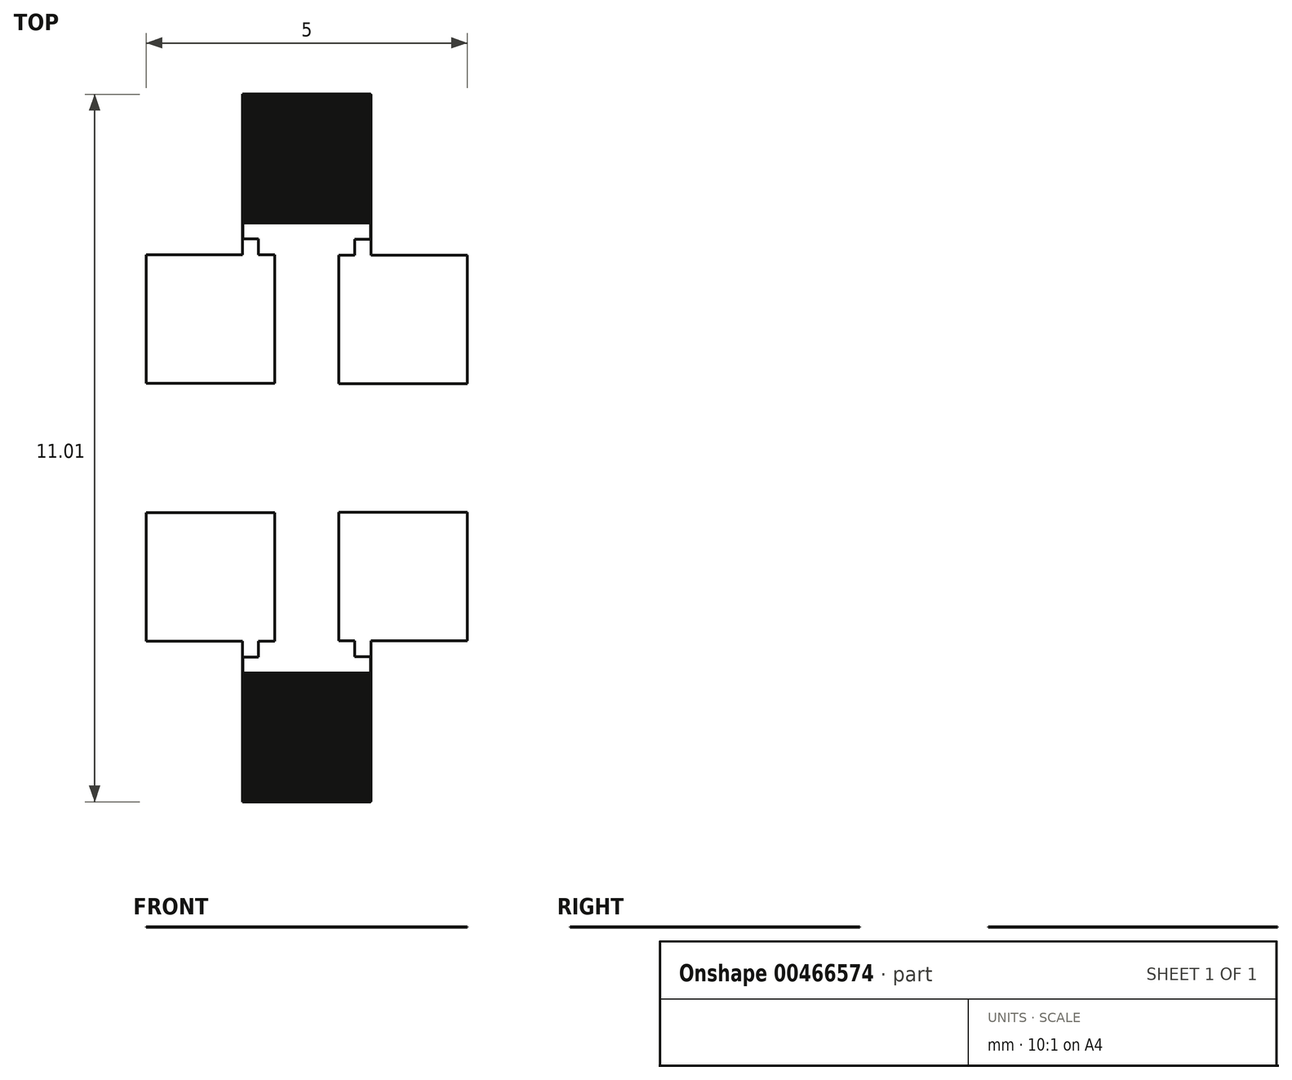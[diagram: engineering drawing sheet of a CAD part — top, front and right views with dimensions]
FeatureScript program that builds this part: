
annotation { "Feature Type Name" : "Feature", "Feature Type Description" : "" }
export const myFeature = defineFeature(function(context is Context, id is Id, definition is map)
    precondition{}
    {
        {
            var Q0;
            Q0=qCreatedBy(makeId("Top.planeOp"),FACE);
            var sketch = newSketch(context, id + "F0", { "sketchPlane" : qUnion([Q0])});
            skLineSegment(sketch, "E0.bottom", {"start": v(-1, 1) * mm, "end": v(1, 1) * mm, "construction": true});
            skLineSegment(sketch, "E0.top", {"start": v(-1, -1) * mm, "end": v(1, -1) * mm, "construction": true});
            skLineSegment(sketch, "E0.left", {"start": v(-1, 1) * mm, "end": v(-1, -1) * mm, "construction": true});
            skLineSegment(sketch, "E0.right", {"start": v(1, 1) * mm, "end": v(1, -1) * mm, "construction": true});
            skSolve(sketch);
        }
        {
            var Q0;
            Q0=qCreatedBy(makeId("Top.planeOp"),FACE);
            var sketch = newSketch(context, id + "F1", { "sketchPlane" : qUnion([Q0])});
            skPoint(sketch, "E1.0", {"position": v(-1, -1) * mm});
            skLineSegment(sketch, "E2", {"start": v(-1, -1) * mm, "end": v(1, -1) * mm});
            skLineSegment(sketch, "E3", {"start": v(1, -1) * mm, "end": v(1, -1) * mm});
            skLineSegment(sketch, "E4", {"start": v(1, -1) * mm, "end": v(-1, -1) * mm});
            skLineSegment(sketch, "E5", {"start": v(-1, -1) * mm, "end": v(-1, 1.5) * mm});
            skPoint(sketch, "E6.0", {"position": v(-1, 1) * mm});
            skLineSegment(sketch, "E7", {"start": v(-1, 1.5) * mm, "end": v(-2.5, 1.5) * mm});
            skLineSegment(sketch, "E8", {"start": v(-2.5, 1.5) * mm, "end": v(-2.5, 3.5) * mm});
            skLineSegment(sketch, "E9", {"start": v(-2.5, 3.5) * mm, "end": v(-0.5, 3.5) * mm});
            skLineSegment(sketch, "E10", {"start": v(-0.5, 3.5) * mm, "end": v(-0.5, 1.5) * mm});
            skLineSegment(sketch, "E11", {"start": v(-0.5, 1.5) * mm, "end": v(-0.75, 1.5) * mm});
            skLineSegment(sketch, "E12", {"start": v(-0.75, 1.5) * mm, "end": v(-0.75, 1.25) * mm});
            skLineSegment(sketch, "E13", {"start": v(-0.75, 1.25) * mm, "end": v(-1, 1.25) * mm});
            skLineSegment(sketch, "E14", {"start": v(-1, -1) * mm, "end": v(-1, -0.99) * mm});
            skLineSegment(sketch, "E15", {"start": v(-1, -0.99) * mm, "end": v(1, -0.99) * mm});
            skLineSegment(sketch, "E16.0", {"start": v(1, 1) * mm, "end": v(1, -1) * mm});
            skLineSegment(sketch, "E17", {"start": v(1, 1) * mm, "end": v(1, 1.5) * mm});
            skLineSegment(sketch, "E18", {"start": v(1, 1.5) * mm, "end": v(2.5, 1.5) * mm});
            skLineSegment(sketch, "E19", {"start": v(2.5, 1.5) * mm, "end": v(2.5, 3.5) * mm});
            skLineSegment(sketch, "E20", {"start": v(2.5, 3.5) * mm, "end": v(0.5, 3.5) * mm});
            skLineSegment(sketch, "E21", {"start": v(0.5, 3.5) * mm, "end": v(0.5, 1.5) * mm});
            skLineSegment(sketch, "E22", {"start": v(0.5, 1.5) * mm, "end": v(0.74, 1.5) * mm});
            skLineSegment(sketch, "E23", {"start": v(0.74, 1.5) * mm, "end": v(0.74, 1.26) * mm});
            skLineSegment(sketch, "E24", {"start": v(0.74, 1.26) * mm, "end": v(1, 1.26) * mm});
            skLineSegment(sketch, "E25", {"start": v(-2.5, 4.5) * mm, "end": v(2.5, 4.5) * mm, "construction": true});
            skLineSegment(sketch, "E26", {"start": v(1, -0.99) * mm, "end": v(1, -0.98) * mm});
            skLineSegment(sketch, "E27", {"start": v(1, -0.98) * mm, "end": v(-1, -0.98) * mm});
            skLineSegment(sketch, "E28.0.1.0", {"start": v(1, -0.97) * mm, "end": v(-1, -0.97) * mm});
            skLineSegment(sketch, "E28.0.1.1", {"start": v(1, -0.98) * mm, "end": v(1, -0.97) * mm});
            skLineSegment(sketch, "E28.0.1.2", {"start": v(-1, -0.98) * mm, "end": v(1, -0.98) * mm});
            skLineSegment(sketch, "E28.0.1.3", {"start": v(-1, -0.98) * mm, "end": v(-1, -0.98) * mm});
            skLineSegment(sketch, "E28.0.2.0", {"start": v(1, -0.96) * mm, "end": v(-1, -0.96) * mm});
            skLineSegment(sketch, "E28.0.2.1", {"start": v(1, -0.96) * mm, "end": v(1, -0.96) * mm});
            skLineSegment(sketch, "E28.0.2.2", {"start": v(-1, -0.96) * mm, "end": v(1, -0.96) * mm});
            skLineSegment(sketch, "E28.0.2.3", {"start": v(-1, -0.97) * mm, "end": v(-1, -0.96) * mm});
            skLineSegment(sketch, "E28.0.3.0", {"start": v(1, -0.95) * mm, "end": v(-1, -0.95) * mm});
            skLineSegment(sketch, "E28.0.3.1", {"start": v(1, -0.95) * mm, "end": v(1, -0.95) * mm});
            skLineSegment(sketch, "E28.0.3.2", {"start": v(-1, -0.95) * mm, "end": v(1, -0.95) * mm});
            skLineSegment(sketch, "E28.0.3.3", {"start": v(-1, -0.96) * mm, "end": v(-1, -0.95) * mm});
            skLineSegment(sketch, "E28.0.4.0", {"start": v(1, -0.94) * mm, "end": v(-1, -0.94) * mm});
            skLineSegment(sketch, "E28.0.4.1", {"start": v(1, -0.94) * mm, "end": v(1, -0.94) * mm});
            skLineSegment(sketch, "E28.0.4.2", {"start": v(-1, -0.94) * mm, "end": v(1, -0.94) * mm});
            skLineSegment(sketch, "E28.0.4.3", {"start": v(-1, -0.95) * mm, "end": v(-1, -0.94) * mm});
            skLineSegment(sketch, "E28.0.5.0", {"start": v(1, -0.92) * mm, "end": v(-1, -0.92) * mm});
            skLineSegment(sketch, "E28.0.5.1", {"start": v(1, -0.93) * mm, "end": v(1, -0.92) * mm});
            skLineSegment(sketch, "E28.0.5.2", {"start": v(-1, -0.93) * mm, "end": v(1, -0.93) * mm});
            skLineSegment(sketch, "E28.0.5.3", {"start": v(-1, -0.94) * mm, "end": v(-1, -0.93) * mm});
            skLineSegment(sketch, "E28.0.6.0", {"start": v(1, -0.91) * mm, "end": v(-1, -0.91) * mm});
            skLineSegment(sketch, "E28.0.6.1", {"start": v(1, -0.92) * mm, "end": v(1, -0.91) * mm});
            skLineSegment(sketch, "E28.0.6.2", {"start": v(-1, -0.92) * mm, "end": v(1, -0.92) * mm});
            skLineSegment(sketch, "E28.0.6.3", {"start": v(-1, -0.92) * mm, "end": v(-1, -0.92) * mm});
            skLineSegment(sketch, "E28.0.7.0", {"start": v(1, -0.9) * mm, "end": v(-1, -0.9) * mm});
            skLineSegment(sketch, "E28.0.7.1", {"start": v(1, -0.9) * mm, "end": v(1, -0.9) * mm});
            skLineSegment(sketch, "E28.0.7.2", {"start": v(-1, -0.9) * mm, "end": v(1, -0.9) * mm});
            skLineSegment(sketch, "E28.0.7.3", {"start": v(-1, -0.91) * mm, "end": v(-1, -0.9) * mm});
            skLineSegment(sketch, "E28.0.8.0", {"start": v(1, -0.89) * mm, "end": v(-1, -0.89) * mm});
            skLineSegment(sketch, "E28.0.8.1", {"start": v(1, -0.9) * mm, "end": v(1, -0.89) * mm});
            skLineSegment(sketch, "E28.0.8.2", {"start": v(-1, -0.9) * mm, "end": v(1, -0.9) * mm});
            skLineSegment(sketch, "E28.0.8.3", {"start": v(-1, -0.9) * mm, "end": v(-1, -0.9) * mm});
            skLineSegment(sketch, "E28.0.9.0", {"start": v(1, -0.88) * mm, "end": v(-1, -0.88) * mm});
            skLineSegment(sketch, "E28.0.9.1", {"start": v(1, -0.88) * mm, "end": v(1, -0.88) * mm});
            skLineSegment(sketch, "E28.0.9.2", {"start": v(-1, -0.88) * mm, "end": v(1, -0.88) * mm});
            skLineSegment(sketch, "E28.0.9.3", {"start": v(-1, -0.89) * mm, "end": v(-1, -0.88) * mm});
            skLineSegment(sketch, "E28.0.10.0", {"start": v(1, -0.86) * mm, "end": v(-1, -0.86) * mm});
            skLineSegment(sketch, "E28.0.10.1", {"start": v(1, -0.87) * mm, "end": v(1, -0.86) * mm});
            skLineSegment(sketch, "E28.0.10.2", {"start": v(-1, -0.87) * mm, "end": v(1, -0.87) * mm});
            skLineSegment(sketch, "E28.0.10.3", {"start": v(-1, -0.88) * mm, "end": v(-1, -0.87) * mm});
            skLineSegment(sketch, "E28.0.11.0", {"start": v(1, -0.85) * mm, "end": v(-1, -0.85) * mm});
            skLineSegment(sketch, "E28.0.11.1", {"start": v(1, -0.86) * mm, "end": v(1, -0.85) * mm});
            skLineSegment(sketch, "E28.0.11.2", {"start": v(-1, -0.86) * mm, "end": v(1, -0.86) * mm});
            skLineSegment(sketch, "E28.0.11.3", {"start": v(-1, -0.86) * mm, "end": v(-1, -0.86) * mm});
            skLineSegment(sketch, "E28.0.12.0", {"start": v(1, -0.84) * mm, "end": v(-1, -0.84) * mm});
            skLineSegment(sketch, "E28.0.12.1", {"start": v(1, -0.84) * mm, "end": v(1, -0.84) * mm});
            skLineSegment(sketch, "E28.0.12.2", {"start": v(-1, -0.84) * mm, "end": v(1, -0.84) * mm});
            skLineSegment(sketch, "E28.0.12.3", {"start": v(-1, -0.85) * mm, "end": v(-1, -0.84) * mm});
            skLineSegment(sketch, "E28.0.13.0", {"start": v(1, -0.83) * mm, "end": v(-1, -0.83) * mm});
            skLineSegment(sketch, "E28.0.13.1", {"start": v(1, -0.83) * mm, "end": v(1, -0.83) * mm});
            skLineSegment(sketch, "E28.0.13.2", {"start": v(-1, -0.83) * mm, "end": v(1, -0.83) * mm});
            skLineSegment(sketch, "E28.0.13.3", {"start": v(-1, -0.84) * mm, "end": v(-1, -0.83) * mm});
            skLineSegment(sketch, "E28.0.14.0", {"start": v(1, -0.82) * mm, "end": v(-1, -0.82) * mm});
            skLineSegment(sketch, "E28.0.14.1", {"start": v(1, -0.82) * mm, "end": v(1, -0.82) * mm});
            skLineSegment(sketch, "E28.0.14.2", {"start": v(-1, -0.82) * mm, "end": v(1, -0.82) * mm});
            skLineSegment(sketch, "E28.0.14.3", {"start": v(-1, -0.83) * mm, "end": v(-1, -0.82) * mm});
            skLineSegment(sketch, "E28.0.15.0", {"start": v(1, -0.8) * mm, "end": v(-1, -0.8) * mm});
            skLineSegment(sketch, "E28.0.15.1", {"start": v(1, -0.8) * mm, "end": v(1, -0.8) * mm});
            skLineSegment(sketch, "E28.0.15.2", {"start": v(-1, -0.8) * mm, "end": v(1, -0.8) * mm});
            skLineSegment(sketch, "E28.0.15.3", {"start": v(-1, -0.82) * mm, "end": v(-1, -0.8) * mm});
            skLineSegment(sketch, "E28.0.16.0", {"start": v(1, -0.8) * mm, "end": v(-1, -0.8) * mm});
            skLineSegment(sketch, "E28.0.16.1", {"start": v(1, -0.8) * mm, "end": v(1, -0.8) * mm});
            skLineSegment(sketch, "E28.0.16.2", {"start": v(-1, -0.8) * mm, "end": v(1, -0.8) * mm});
            skLineSegment(sketch, "E28.0.16.3", {"start": v(-1, -0.8) * mm, "end": v(-1, -0.8) * mm});
            skLineSegment(sketch, "E28.0.17.0", {"start": v(1, -0.78) * mm, "end": v(-1, -0.78) * mm});
            skLineSegment(sketch, "E28.0.17.1", {"start": v(1, -0.78) * mm, "end": v(1, -0.78) * mm});
            skLineSegment(sketch, "E28.0.17.2", {"start": v(-1, -0.78) * mm, "end": v(1, -0.78) * mm});
            skLineSegment(sketch, "E28.0.17.3", {"start": v(-1, -0.8) * mm, "end": v(-1, -0.78) * mm});
            skLineSegment(sketch, "E28.0.18.0", {"start": v(1, -0.77) * mm, "end": v(-1, -0.77) * mm});
            skLineSegment(sketch, "E28.0.18.1", {"start": v(1, -0.77) * mm, "end": v(1, -0.77) * mm});
            skLineSegment(sketch, "E28.0.18.2", {"start": v(-1, -0.77) * mm, "end": v(1, -0.77) * mm});
            skLineSegment(sketch, "E28.0.18.3", {"start": v(-1, -0.78) * mm, "end": v(-1, -0.77) * mm});
            skLineSegment(sketch, "E28.0.19.0", {"start": v(1, -0.76) * mm, "end": v(-1, -0.76) * mm});
            skLineSegment(sketch, "E28.0.19.1", {"start": v(1, -0.76) * mm, "end": v(1, -0.76) * mm});
            skLineSegment(sketch, "E28.0.19.2", {"start": v(-1, -0.76) * mm, "end": v(1, -0.76) * mm});
            skLineSegment(sketch, "E28.0.19.3", {"start": v(-1, -0.77) * mm, "end": v(-1, -0.76) * mm});
            skLineSegment(sketch, "E28.0.20.0", {"start": v(1, -0.74) * mm, "end": v(-1, -0.74) * mm});
            skLineSegment(sketch, "E28.0.20.1", {"start": v(1, -0.75) * mm, "end": v(1, -0.74) * mm});
            skLineSegment(sketch, "E28.0.20.2", {"start": v(-1, -0.75) * mm, "end": v(1, -0.75) * mm});
            skLineSegment(sketch, "E28.0.20.3", {"start": v(-1, -0.76) * mm, "end": v(-1, -0.75) * mm});
            skLineSegment(sketch, "E28.0.21.0", {"start": v(1, -0.73) * mm, "end": v(-1, -0.73) * mm});
            skLineSegment(sketch, "E28.0.21.1", {"start": v(1, -0.74) * mm, "end": v(1, -0.73) * mm});
            skLineSegment(sketch, "E28.0.21.2", {"start": v(-1, -0.74) * mm, "end": v(1, -0.74) * mm});
            skLineSegment(sketch, "E28.0.21.3", {"start": v(-1, -0.74) * mm, "end": v(-1, -0.74) * mm});
            skLineSegment(sketch, "E28.0.22.0", {"start": v(1, -0.72) * mm, "end": v(-1, -0.72) * mm});
            skLineSegment(sketch, "E28.0.22.1", {"start": v(1, -0.72) * mm, "end": v(1, -0.72) * mm});
            skLineSegment(sketch, "E28.0.22.2", {"start": v(-1, -0.72) * mm, "end": v(1, -0.72) * mm});
            skLineSegment(sketch, "E28.0.22.3", {"start": v(-1, -0.73) * mm, "end": v(-1, -0.72) * mm});
            skLineSegment(sketch, "E28.0.23.0", {"start": v(1, -0.7) * mm, "end": v(-1, -0.7) * mm});
            skLineSegment(sketch, "E28.0.23.1", {"start": v(1, -0.71) * mm, "end": v(1, -0.7) * mm});
            skLineSegment(sketch, "E28.0.23.2", {"start": v(-1, -0.71) * mm, "end": v(1, -0.71) * mm});
            skLineSegment(sketch, "E28.0.23.3", {"start": v(-1, -0.72) * mm, "end": v(-1, -0.71) * mm});
            skLineSegment(sketch, "E28.0.24.0", {"start": v(1, -0.7) * mm, "end": v(-1, -0.7) * mm});
            skLineSegment(sketch, "E28.0.24.1", {"start": v(1, -0.7) * mm, "end": v(1, -0.7) * mm});
            skLineSegment(sketch, "E28.0.24.2", {"start": v(-1, -0.7) * mm, "end": v(1, -0.7) * mm});
            skLineSegment(sketch, "E28.0.24.3", {"start": v(-1, -0.7) * mm, "end": v(-1, -0.7) * mm});
            skLineSegment(sketch, "E28.0.25.0", {"start": v(1, -0.68) * mm, "end": v(-1, -0.68) * mm});
            skLineSegment(sketch, "E28.0.25.1", {"start": v(1, -0.69) * mm, "end": v(1, -0.68) * mm});
            skLineSegment(sketch, "E28.0.25.2", {"start": v(-1, -0.69) * mm, "end": v(1, -0.69) * mm});
            skLineSegment(sketch, "E28.0.25.3", {"start": v(-1, -0.7) * mm, "end": v(-1, -0.69) * mm});
            skLineSegment(sketch, "E28.0.26.0", {"start": v(1, -0.67) * mm, "end": v(-1, -0.67) * mm});
            skLineSegment(sketch, "E28.0.26.1", {"start": v(1, -0.68) * mm, "end": v(1, -0.67) * mm});
            skLineSegment(sketch, "E28.0.26.2", {"start": v(-1, -0.68) * mm, "end": v(1, -0.68) * mm});
            skLineSegment(sketch, "E28.0.26.3", {"start": v(-1, -0.68) * mm, "end": v(-1, -0.68) * mm});
            skLineSegment(sketch, "E28.0.27.0", {"start": v(1, -0.66) * mm, "end": v(-1, -0.66) * mm});
            skLineSegment(sketch, "E28.0.27.1", {"start": v(1, -0.66) * mm, "end": v(1, -0.66) * mm});
            skLineSegment(sketch, "E28.0.27.2", {"start": v(-1, -0.66) * mm, "end": v(1, -0.66) * mm});
            skLineSegment(sketch, "E28.0.27.3", {"start": v(-1, -0.67) * mm, "end": v(-1, -0.66) * mm});
            skLineSegment(sketch, "E28.0.28.0", {"start": v(1, -0.65) * mm, "end": v(-1, -0.65) * mm});
            skLineSegment(sketch, "E28.0.28.1", {"start": v(1, -0.65) * mm, "end": v(1, -0.65) * mm});
            skLineSegment(sketch, "E28.0.28.2", {"start": v(-1, -0.65) * mm, "end": v(1, -0.65) * mm});
            skLineSegment(sketch, "E28.0.28.3", {"start": v(-1, -0.66) * mm, "end": v(-1, -0.65) * mm});
            skLineSegment(sketch, "E28.0.29.0", {"start": v(1, -0.64) * mm, "end": v(-1, -0.64) * mm});
            skLineSegment(sketch, "E28.0.29.1", {"start": v(1, -0.64) * mm, "end": v(1, -0.64) * mm});
            skLineSegment(sketch, "E28.0.29.2", {"start": v(-1, -0.64) * mm, "end": v(1, -0.64) * mm});
            skLineSegment(sketch, "E28.0.29.3", {"start": v(-1, -0.65) * mm, "end": v(-1, -0.64) * mm});
            skLineSegment(sketch, "E28.0.30.0", {"start": v(1, -0.62) * mm, "end": v(-1, -0.62) * mm});
            skLineSegment(sketch, "E28.0.30.1", {"start": v(1, -0.63) * mm, "end": v(1, -0.62) * mm});
            skLineSegment(sketch, "E28.0.30.2", {"start": v(-1, -0.63) * mm, "end": v(1, -0.63) * mm});
            skLineSegment(sketch, "E28.0.30.3", {"start": v(-1, -0.64) * mm, "end": v(-1, -0.63) * mm});
            skLineSegment(sketch, "E28.0.31.0", {"start": v(1, -0.61) * mm, "end": v(-1, -0.61) * mm});
            skLineSegment(sketch, "E28.0.31.1", {"start": v(1, -0.62) * mm, "end": v(1, -0.61) * mm});
            skLineSegment(sketch, "E28.0.31.2", {"start": v(-1, -0.62) * mm, "end": v(1, -0.62) * mm});
            skLineSegment(sketch, "E28.0.31.3", {"start": v(-1, -0.62) * mm, "end": v(-1, -0.62) * mm});
            skLineSegment(sketch, "E28.0.32.0", {"start": v(1, -0.6) * mm, "end": v(-1, -0.6) * mm});
            skLineSegment(sketch, "E28.0.32.1", {"start": v(1, -0.6) * mm, "end": v(1, -0.6) * mm});
            skLineSegment(sketch, "E28.0.32.2", {"start": v(-1, -0.6) * mm, "end": v(1, -0.6) * mm});
            skLineSegment(sketch, "E28.0.32.3", {"start": v(-1, -0.61) * mm, "end": v(-1, -0.6) * mm});
            skLineSegment(sketch, "E28.0.33.0", {"start": v(1, -0.59) * mm, "end": v(-1, -0.59) * mm});
            skLineSegment(sketch, "E28.0.33.1", {"start": v(1, -0.6) * mm, "end": v(1, -0.59) * mm});
            skLineSegment(sketch, "E28.0.33.2", {"start": v(-1, -0.6) * mm, "end": v(1, -0.6) * mm});
            skLineSegment(sketch, "E28.0.33.3", {"start": v(-1, -0.6) * mm, "end": v(-1, -0.6) * mm});
            skLineSegment(sketch, "E28.0.34.0", {"start": v(1, -0.58) * mm, "end": v(-1, -0.58) * mm});
            skLineSegment(sketch, "E28.0.34.1", {"start": v(1, -0.58) * mm, "end": v(1, -0.58) * mm});
            skLineSegment(sketch, "E28.0.34.2", {"start": v(-1, -0.58) * mm, "end": v(1, -0.58) * mm});
            skLineSegment(sketch, "E28.0.34.3", {"start": v(-1, -0.59) * mm, "end": v(-1, -0.58) * mm});
            skLineSegment(sketch, "E28.0.35.0", {"start": v(1, -0.56) * mm, "end": v(-1, -0.56) * mm});
            skLineSegment(sketch, "E28.0.35.1", {"start": v(1, -0.57) * mm, "end": v(1, -0.56) * mm});
            skLineSegment(sketch, "E28.0.35.2", {"start": v(-1, -0.57) * mm, "end": v(1, -0.57) * mm});
            skLineSegment(sketch, "E28.0.35.3", {"start": v(-1, -0.58) * mm, "end": v(-1, -0.57) * mm});
            skLineSegment(sketch, "E28.0.36.0", {"start": v(1, -0.55) * mm, "end": v(-1, -0.55) * mm});
            skLineSegment(sketch, "E28.0.36.1", {"start": v(1, -0.56) * mm, "end": v(1, -0.55) * mm});
            skLineSegment(sketch, "E28.0.36.2", {"start": v(-1, -0.56) * mm, "end": v(1, -0.56) * mm});
            skLineSegment(sketch, "E28.0.36.3", {"start": v(-1, -0.56) * mm, "end": v(-1, -0.56) * mm});
            skLineSegment(sketch, "E28.0.37.0", {"start": v(1, -0.54) * mm, "end": v(-1, -0.54) * mm});
            skLineSegment(sketch, "E28.0.37.1", {"start": v(1, -0.54) * mm, "end": v(1, -0.54) * mm});
            skLineSegment(sketch, "E28.0.37.2", {"start": v(-1, -0.54) * mm, "end": v(1, -0.54) * mm});
            skLineSegment(sketch, "E28.0.37.3", {"start": v(-1, -0.55) * mm, "end": v(-1, -0.54) * mm});
            skLineSegment(sketch, "E28.0.38.0", {"start": v(1, -0.53) * mm, "end": v(-1, -0.53) * mm});
            skLineSegment(sketch, "E28.0.38.1", {"start": v(1, -0.53) * mm, "end": v(1, -0.53) * mm});
            skLineSegment(sketch, "E28.0.38.2", {"start": v(-1, -0.53) * mm, "end": v(1, -0.53) * mm});
            skLineSegment(sketch, "E28.0.38.3", {"start": v(-1, -0.54) * mm, "end": v(-1, -0.53) * mm});
            skLineSegment(sketch, "E28.0.39.0", {"start": v(1, -0.52) * mm, "end": v(-1, -0.52) * mm});
            skLineSegment(sketch, "E28.0.39.1", {"start": v(1, -0.52) * mm, "end": v(1, -0.52) * mm});
            skLineSegment(sketch, "E28.0.39.2", {"start": v(-1, -0.52) * mm, "end": v(1, -0.52) * mm});
            skLineSegment(sketch, "E28.0.39.3", {"start": v(-1, -0.53) * mm, "end": v(-1, -0.52) * mm});
            skLineSegment(sketch, "E28.0.40.0", {"start": v(1, -0.5) * mm, "end": v(-1, -0.5) * mm});
            skLineSegment(sketch, "E28.0.40.1", {"start": v(1, -0.5) * mm, "end": v(1, -0.5) * mm});
            skLineSegment(sketch, "E28.0.40.2", {"start": v(-1, -0.5) * mm, "end": v(1, -0.5) * mm});
            skLineSegment(sketch, "E28.0.40.3", {"start": v(-1, -0.52) * mm, "end": v(-1, -0.5) * mm});
            skLineSegment(sketch, "E28.0.41.0", {"start": v(1, -0.5) * mm, "end": v(-1, -0.5) * mm});
            skLineSegment(sketch, "E28.0.41.1", {"start": v(1, -0.5) * mm, "end": v(1, -0.5) * mm});
            skLineSegment(sketch, "E28.0.41.2", {"start": v(-1, -0.5) * mm, "end": v(1, -0.5) * mm});
            skLineSegment(sketch, "E28.0.41.3", {"start": v(-1, -0.5) * mm, "end": v(-1, -0.5) * mm});
            skLineSegment(sketch, "E28.0.42.0", {"start": v(1, -0.48) * mm, "end": v(-1, -0.48) * mm});
            skLineSegment(sketch, "E28.0.42.1", {"start": v(1, -0.48) * mm, "end": v(1, -0.48) * mm});
            skLineSegment(sketch, "E28.0.42.2", {"start": v(-1, -0.48) * mm, "end": v(1, -0.48) * mm});
            skLineSegment(sketch, "E28.0.42.3", {"start": v(-1, -0.5) * mm, "end": v(-1, -0.48) * mm});
            skLineSegment(sketch, "E28.0.43.0", {"start": v(1, -0.47) * mm, "end": v(-1, -0.47) * mm});
            skLineSegment(sketch, "E28.0.43.1", {"start": v(1, -0.47) * mm, "end": v(1, -0.47) * mm});
            skLineSegment(sketch, "E28.0.43.2", {"start": v(-1, -0.47) * mm, "end": v(1, -0.47) * mm});
            skLineSegment(sketch, "E28.0.43.3", {"start": v(-1, -0.48) * mm, "end": v(-1, -0.47) * mm});
            skLineSegment(sketch, "E28.0.44.0", {"start": v(1, -0.46) * mm, "end": v(-1, -0.46) * mm});
            skLineSegment(sketch, "E28.0.44.1", {"start": v(1, -0.46) * mm, "end": v(1, -0.46) * mm});
            skLineSegment(sketch, "E28.0.44.2", {"start": v(-1, -0.46) * mm, "end": v(1, -0.46) * mm});
            skLineSegment(sketch, "E28.0.44.3", {"start": v(-1, -0.47) * mm, "end": v(-1, -0.46) * mm});
            skLineSegment(sketch, "E28.0.45.0", {"start": v(1, -0.44) * mm, "end": v(-1, -0.44) * mm});
            skLineSegment(sketch, "E28.0.45.1", {"start": v(1, -0.45) * mm, "end": v(1, -0.44) * mm});
            skLineSegment(sketch, "E28.0.45.2", {"start": v(-1, -0.45) * mm, "end": v(1, -0.45) * mm});
            skLineSegment(sketch, "E28.0.45.3", {"start": v(-1, -0.46) * mm, "end": v(-1, -0.45) * mm});
            skLineSegment(sketch, "E28.0.46.0", {"start": v(1, -0.43) * mm, "end": v(-1, -0.43) * mm});
            skLineSegment(sketch, "E28.0.46.1", {"start": v(1, -0.44) * mm, "end": v(1, -0.43) * mm});
            skLineSegment(sketch, "E28.0.46.2", {"start": v(-1, -0.44) * mm, "end": v(1, -0.44) * mm});
            skLineSegment(sketch, "E28.0.46.3", {"start": v(-1, -0.44) * mm, "end": v(-1, -0.44) * mm});
            skLineSegment(sketch, "E28.0.47.0", {"start": v(1, -0.42) * mm, "end": v(-1, -0.42) * mm});
            skLineSegment(sketch, "E28.0.47.1", {"start": v(1, -0.42) * mm, "end": v(1, -0.42) * mm});
            skLineSegment(sketch, "E28.0.47.2", {"start": v(-1, -0.42) * mm, "end": v(1, -0.42) * mm});
            skLineSegment(sketch, "E28.0.47.3", {"start": v(-1, -0.43) * mm, "end": v(-1, -0.42) * mm});
            skLineSegment(sketch, "E28.0.48.0", {"start": v(1, -0.4) * mm, "end": v(-1, -0.4) * mm});
            skLineSegment(sketch, "E28.0.48.1", {"start": v(1, -0.41) * mm, "end": v(1, -0.4) * mm});
            skLineSegment(sketch, "E28.0.48.2", {"start": v(-1, -0.41) * mm, "end": v(1, -0.41) * mm});
            skLineSegment(sketch, "E28.0.48.3", {"start": v(-1, -0.42) * mm, "end": v(-1, -0.41) * mm});
            skLineSegment(sketch, "E28.0.49.0", {"start": v(1, -0.4) * mm, "end": v(-1, -0.4) * mm});
            skLineSegment(sketch, "E28.0.49.1", {"start": v(1, -0.4) * mm, "end": v(1, -0.4) * mm});
            skLineSegment(sketch, "E28.0.49.2", {"start": v(-1, -0.4) * mm, "end": v(1, -0.4) * mm});
            skLineSegment(sketch, "E28.0.49.3", {"start": v(-1, -0.4) * mm, "end": v(-1, -0.4) * mm});
            skLineSegment(sketch, "E28.0.50.0", {"start": v(1, -0.38) * mm, "end": v(-1, -0.38) * mm});
            skLineSegment(sketch, "E28.0.50.1", {"start": v(1, -0.39) * mm, "end": v(1, -0.38) * mm});
            skLineSegment(sketch, "E28.0.50.2", {"start": v(-1, -0.39) * mm, "end": v(1, -0.39) * mm});
            skLineSegment(sketch, "E28.0.50.3", {"start": v(-1, -0.4) * mm, "end": v(-1, -0.39) * mm});
            skLineSegment(sketch, "E28.0.51.0", {"start": v(1, -0.37) * mm, "end": v(-1, -0.37) * mm});
            skLineSegment(sketch, "E28.0.51.1", {"start": v(1, -0.38) * mm, "end": v(1, -0.37) * mm});
            skLineSegment(sketch, "E28.0.51.2", {"start": v(-1, -0.38) * mm, "end": v(1, -0.38) * mm});
            skLineSegment(sketch, "E28.0.51.3", {"start": v(-1, -0.38) * mm, "end": v(-1, -0.38) * mm});
            skLineSegment(sketch, "E28.0.52.0", {"start": v(1, -0.36) * mm, "end": v(-1, -0.36) * mm});
            skLineSegment(sketch, "E28.0.52.1", {"start": v(1, -0.36) * mm, "end": v(1, -0.36) * mm});
            skLineSegment(sketch, "E28.0.52.2", {"start": v(-1, -0.36) * mm, "end": v(1, -0.36) * mm});
            skLineSegment(sketch, "E28.0.52.3", {"start": v(-1, -0.37) * mm, "end": v(-1, -0.36) * mm});
            skLineSegment(sketch, "E28.0.53.0", {"start": v(1, -0.35) * mm, "end": v(-1, -0.35) * mm});
            skLineSegment(sketch, "E28.0.53.1", {"start": v(1, -0.35) * mm, "end": v(1, -0.35) * mm});
            skLineSegment(sketch, "E28.0.53.2", {"start": v(-1, -0.35) * mm, "end": v(1, -0.35) * mm});
            skLineSegment(sketch, "E28.0.53.3", {"start": v(-1, -0.36) * mm, "end": v(-1, -0.35) * mm});
            skLineSegment(sketch, "E28.0.54.0", {"start": v(1, -0.34) * mm, "end": v(-1, -0.34) * mm});
            skLineSegment(sketch, "E28.0.54.1", {"start": v(1, -0.34) * mm, "end": v(1, -0.34) * mm});
            skLineSegment(sketch, "E28.0.54.2", {"start": v(-1, -0.34) * mm, "end": v(1, -0.34) * mm});
            skLineSegment(sketch, "E28.0.54.3", {"start": v(-1, -0.35) * mm, "end": v(-1, -0.34) * mm});
            skLineSegment(sketch, "E28.0.55.0", {"start": v(1, -0.32) * mm, "end": v(-1, -0.32) * mm});
            skLineSegment(sketch, "E28.0.55.1", {"start": v(1, -0.33) * mm, "end": v(1, -0.32) * mm});
            skLineSegment(sketch, "E28.0.55.2", {"start": v(-1, -0.33) * mm, "end": v(1, -0.33) * mm});
            skLineSegment(sketch, "E28.0.55.3", {"start": v(-1, -0.34) * mm, "end": v(-1, -0.33) * mm});
            skLineSegment(sketch, "E28.0.56.0", {"start": v(1, -0.31) * mm, "end": v(-1, -0.31) * mm});
            skLineSegment(sketch, "E28.0.56.1", {"start": v(1, -0.32) * mm, "end": v(1, -0.31) * mm});
            skLineSegment(sketch, "E28.0.56.2", {"start": v(-1, -0.32) * mm, "end": v(1, -0.32) * mm});
            skLineSegment(sketch, "E28.0.56.3", {"start": v(-1, -0.32) * mm, "end": v(-1, -0.32) * mm});
            skLineSegment(sketch, "E28.0.57.0", {"start": v(1, -0.3) * mm, "end": v(-1, -0.3) * mm});
            skLineSegment(sketch, "E28.0.57.1", {"start": v(1, -0.3) * mm, "end": v(1, -0.3) * mm});
            skLineSegment(sketch, "E28.0.57.2", {"start": v(-1, -0.3) * mm, "end": v(1, -0.3) * mm});
            skLineSegment(sketch, "E28.0.57.3", {"start": v(-1, -0.31) * mm, "end": v(-1, -0.3) * mm});
            skLineSegment(sketch, "E28.0.58.0", {"start": v(1, -0.29) * mm, "end": v(-1, -0.29) * mm});
            skLineSegment(sketch, "E28.0.58.1", {"start": v(1, -0.3) * mm, "end": v(1, -0.29) * mm});
            skLineSegment(sketch, "E28.0.58.2", {"start": v(-1, -0.3) * mm, "end": v(1, -0.3) * mm});
            skLineSegment(sketch, "E28.0.58.3", {"start": v(-1, -0.3) * mm, "end": v(-1, -0.3) * mm});
            skLineSegment(sketch, "E28.0.59.0", {"start": v(1, -0.28) * mm, "end": v(-1, -0.28) * mm});
            skLineSegment(sketch, "E28.0.59.1", {"start": v(1, -0.28) * mm, "end": v(1, -0.28) * mm});
            skLineSegment(sketch, "E28.0.59.2", {"start": v(-1, -0.28) * mm, "end": v(1, -0.28) * mm});
            skLineSegment(sketch, "E28.0.59.3", {"start": v(-1, -0.29) * mm, "end": v(-1, -0.28) * mm});
            skLineSegment(sketch, "E28.0.60.0", {"start": v(1, -0.26) * mm, "end": v(-1, -0.26) * mm});
            skLineSegment(sketch, "E28.0.60.1", {"start": v(1, -0.27) * mm, "end": v(1, -0.26) * mm});
            skLineSegment(sketch, "E28.0.60.2", {"start": v(-1, -0.27) * mm, "end": v(1, -0.27) * mm});
            skLineSegment(sketch, "E28.0.60.3", {"start": v(-1, -0.28) * mm, "end": v(-1, -0.27) * mm});
            skLineSegment(sketch, "E28.0.61.0", {"start": v(1, -0.25) * mm, "end": v(-1, -0.25) * mm});
            skLineSegment(sketch, "E28.0.61.1", {"start": v(1, -0.26) * mm, "end": v(1, -0.25) * mm});
            skLineSegment(sketch, "E28.0.61.2", {"start": v(-1, -0.26) * mm, "end": v(1, -0.26) * mm});
            skLineSegment(sketch, "E28.0.61.3", {"start": v(-1, -0.26) * mm, "end": v(-1, -0.26) * mm});
            skLineSegment(sketch, "E28.0.62.0", {"start": v(1, -0.24) * mm, "end": v(-1, -0.24) * mm});
            skLineSegment(sketch, "E28.0.62.1", {"start": v(1, -0.24) * mm, "end": v(1, -0.24) * mm});
            skLineSegment(sketch, "E28.0.62.2", {"start": v(-1, -0.24) * mm, "end": v(1, -0.24) * mm});
            skLineSegment(sketch, "E28.0.62.3", {"start": v(-1, -0.25) * mm, "end": v(-1, -0.24) * mm});
            skLineSegment(sketch, "E28.0.63.0", {"start": v(1, -0.23) * mm, "end": v(-1, -0.23) * mm});
            skLineSegment(sketch, "E28.0.63.1", {"start": v(1, -0.23) * mm, "end": v(1, -0.23) * mm});
            skLineSegment(sketch, "E28.0.63.2", {"start": v(-1, -0.23) * mm, "end": v(1, -0.23) * mm});
            skLineSegment(sketch, "E28.0.63.3", {"start": v(-1, -0.24) * mm, "end": v(-1, -0.23) * mm});
            skLineSegment(sketch, "E28.0.64.0", {"start": v(1, -0.22) * mm, "end": v(-1, -0.22) * mm});
            skLineSegment(sketch, "E28.0.64.1", {"start": v(1, -0.22) * mm, "end": v(1, -0.22) * mm});
            skLineSegment(sketch, "E28.0.64.2", {"start": v(-1, -0.22) * mm, "end": v(1, -0.22) * mm});
            skLineSegment(sketch, "E28.0.64.3", {"start": v(-1, -0.23) * mm, "end": v(-1, -0.22) * mm});
            skLineSegment(sketch, "E28.0.65.0", {"start": v(1, -0.2) * mm, "end": v(-1, -0.2) * mm});
            skLineSegment(sketch, "E28.0.65.1", {"start": v(1, -0.2) * mm, "end": v(1, -0.2) * mm});
            skLineSegment(sketch, "E28.0.65.2", {"start": v(-1, -0.2) * mm, "end": v(1, -0.2) * mm});
            skLineSegment(sketch, "E28.0.65.3", {"start": v(-1, -0.22) * mm, "end": v(-1, -0.2) * mm});
            skLineSegment(sketch, "E28.0.66.0", {"start": v(1, -0.2) * mm, "end": v(-1, -0.2) * mm});
            skLineSegment(sketch, "E28.0.66.1", {"start": v(1, -0.2) * mm, "end": v(1, -0.2) * mm});
            skLineSegment(sketch, "E28.0.66.2", {"start": v(-1, -0.2) * mm, "end": v(1, -0.2) * mm});
            skLineSegment(sketch, "E28.0.66.3", {"start": v(-1, -0.2) * mm, "end": v(-1, -0.2) * mm});
            skLineSegment(sketch, "E28.0.67.0", {"start": v(1, -0.18) * mm, "end": v(-1, -0.18) * mm});
            skLineSegment(sketch, "E28.0.67.1", {"start": v(1, -0.18) * mm, "end": v(1, -0.18) * mm});
            skLineSegment(sketch, "E28.0.67.2", {"start": v(-1, -0.18) * mm, "end": v(1, -0.18) * mm});
            skLineSegment(sketch, "E28.0.67.3", {"start": v(-1, -0.2) * mm, "end": v(-1, -0.18) * mm});
            skLineSegment(sketch, "E28.0.68.0", {"start": v(1, -0.17) * mm, "end": v(-1, -0.17) * mm});
            skLineSegment(sketch, "E28.0.68.1", {"start": v(1, -0.17) * mm, "end": v(1, -0.17) * mm});
            skLineSegment(sketch, "E28.0.68.2", {"start": v(-1, -0.17) * mm, "end": v(1, -0.17) * mm});
            skLineSegment(sketch, "E28.0.68.3", {"start": v(-1, -0.18) * mm, "end": v(-1, -0.17) * mm});
            skLineSegment(sketch, "E28.0.69.0", {"start": v(1, -0.16) * mm, "end": v(-1, -0.16) * mm});
            skLineSegment(sketch, "E28.0.69.1", {"start": v(1, -0.16) * mm, "end": v(1, -0.16) * mm});
            skLineSegment(sketch, "E28.0.69.2", {"start": v(-1, -0.16) * mm, "end": v(1, -0.16) * mm});
            skLineSegment(sketch, "E28.0.69.3", {"start": v(-1, -0.17) * mm, "end": v(-1, -0.16) * mm});
            skLineSegment(sketch, "E28.0.70.0", {"start": v(1, -0.14) * mm, "end": v(-1, -0.14) * mm});
            skLineSegment(sketch, "E28.0.70.1", {"start": v(1, -0.15) * mm, "end": v(1, -0.14) * mm});
            skLineSegment(sketch, "E28.0.70.2", {"start": v(-1, -0.15) * mm, "end": v(1, -0.15) * mm});
            skLineSegment(sketch, "E28.0.70.3", {"start": v(-1, -0.16) * mm, "end": v(-1, -0.15) * mm});
            skLineSegment(sketch, "E28.0.71.0", {"start": v(1, -0.13) * mm, "end": v(-1, -0.13) * mm});
            skLineSegment(sketch, "E28.0.71.1", {"start": v(1, -0.14) * mm, "end": v(1, -0.13) * mm});
            skLineSegment(sketch, "E28.0.71.2", {"start": v(-1, -0.14) * mm, "end": v(1, -0.14) * mm});
            skLineSegment(sketch, "E28.0.71.3", {"start": v(-1, -0.14) * mm, "end": v(-1, -0.14) * mm});
            skLineSegment(sketch, "E28.0.72.0", {"start": v(1, -0.12) * mm, "end": v(-1, -0.12) * mm});
            skLineSegment(sketch, "E28.0.72.1", {"start": v(1, -0.12) * mm, "end": v(1, -0.12) * mm});
            skLineSegment(sketch, "E28.0.72.2", {"start": v(-1, -0.12) * mm, "end": v(1, -0.12) * mm});
            skLineSegment(sketch, "E28.0.72.3", {"start": v(-1, -0.13) * mm, "end": v(-1, -0.12) * mm});
            skLineSegment(sketch, "E28.0.73.0", {"start": v(1, -0.1) * mm, "end": v(-1, -0.1) * mm});
            skLineSegment(sketch, "E28.0.73.1", {"start": v(1, -0.11) * mm, "end": v(1, -0.1) * mm});
            skLineSegment(sketch, "E28.0.73.2", {"start": v(-1, -0.11) * mm, "end": v(1, -0.11) * mm});
            skLineSegment(sketch, "E28.0.73.3", {"start": v(-1, -0.12) * mm, "end": v(-1, -0.11) * mm});
            skLineSegment(sketch, "E28.0.74.0", {"start": v(1, -0.1) * mm, "end": v(-1, -0.1) * mm});
            skLineSegment(sketch, "E28.0.74.1", {"start": v(1, -0.1) * mm, "end": v(1, -0.1) * mm});
            skLineSegment(sketch, "E28.0.74.2", {"start": v(-1, -0.1) * mm, "end": v(1, -0.1) * mm});
            skLineSegment(sketch, "E28.0.74.3", {"start": v(-1, -0.1) * mm, "end": v(-1, -0.1) * mm});
            skLineSegment(sketch, "E28.0.75.0", {"start": v(1, -0.08) * mm, "end": v(-1, -0.08) * mm});
            skLineSegment(sketch, "E28.0.75.1", {"start": v(1, -0.09) * mm, "end": v(1, -0.08) * mm});
            skLineSegment(sketch, "E28.0.75.2", {"start": v(-1, -0.09) * mm, "end": v(1, -0.09) * mm});
            skLineSegment(sketch, "E28.0.75.3", {"start": v(-1, -0.1) * mm, "end": v(-1, -0.09) * mm});
            skLineSegment(sketch, "E28.0.76.0", {"start": v(1, -0.07) * mm, "end": v(-1, -0.07) * mm});
            skLineSegment(sketch, "E28.0.76.1", {"start": v(1, -0.08) * mm, "end": v(1, -0.07) * mm});
            skLineSegment(sketch, "E28.0.76.2", {"start": v(-1, -0.08) * mm, "end": v(1, -0.08) * mm});
            skLineSegment(sketch, "E28.0.76.3", {"start": v(-1, -0.08) * mm, "end": v(-1, -0.08) * mm});
            skLineSegment(sketch, "E28.0.77.0", {"start": v(1, -0.06) * mm, "end": v(-1, -0.06) * mm});
            skLineSegment(sketch, "E28.0.77.1", {"start": v(1, -0.06) * mm, "end": v(1, -0.06) * mm});
            skLineSegment(sketch, "E28.0.77.2", {"start": v(-1, -0.06) * mm, "end": v(1, -0.06) * mm});
            skLineSegment(sketch, "E28.0.77.3", {"start": v(-1, -0.07) * mm, "end": v(-1, -0.06) * mm});
            skLineSegment(sketch, "E28.0.78.0", {"start": v(1, -0.05) * mm, "end": v(-1, -0.05) * mm});
            skLineSegment(sketch, "E28.0.78.1", {"start": v(1, -0.05) * mm, "end": v(1, -0.05) * mm});
            skLineSegment(sketch, "E28.0.78.2", {"start": v(-1, -0.05) * mm, "end": v(1, -0.05) * mm});
            skLineSegment(sketch, "E28.0.78.3", {"start": v(-1, -0.06) * mm, "end": v(-1, -0.05) * mm});
            skLineSegment(sketch, "E28.0.79.0", {"start": v(1, -0.04) * mm, "end": v(-1, -0.04) * mm});
            skLineSegment(sketch, "E28.0.79.1", {"start": v(1, -0.04) * mm, "end": v(1, -0.04) * mm});
            skLineSegment(sketch, "E28.0.79.2", {"start": v(-1, -0.04) * mm, "end": v(1, -0.04) * mm});
            skLineSegment(sketch, "E28.0.79.3", {"start": v(-1, -0.05) * mm, "end": v(-1, -0.04) * mm});
            skLineSegment(sketch, "E28.0.80.0", {"start": v(1, -0.02) * mm, "end": v(-1, -0.02) * mm});
            skLineSegment(sketch, "E28.0.80.1", {"start": v(1, -0.03) * mm, "end": v(1, -0.02) * mm});
            skLineSegment(sketch, "E28.0.80.2", {"start": v(-1, -0.03) * mm, "end": v(1, -0.03) * mm});
            skLineSegment(sketch, "E28.0.80.3", {"start": v(-1, -0.04) * mm, "end": v(-1, -0.03) * mm});
            skLineSegment(sketch, "E28.0.81.0", {"start": v(1, -0.01) * mm, "end": v(-1, -0.01) * mm});
            skLineSegment(sketch, "E28.0.81.1", {"start": v(1, -0.02) * mm, "end": v(1, -0.01) * mm});
            skLineSegment(sketch, "E28.0.81.2", {"start": v(-1, -0.02) * mm, "end": v(1, -0.02) * mm});
            skLineSegment(sketch, "E28.0.81.3", {"start": v(-1, -0.02) * mm, "end": v(-1, -0.02) * mm});
            skLineSegment(sketch, "E28.0.82.0", {"start": v(1, 0) * mm, "end": v(-1, 0) * mm});
            skLineSegment(sketch, "E28.0.82.1", {"start": v(1, 0) * mm, "end": v(1, 0) * mm});
            skLineSegment(sketch, "E28.0.82.2", {"start": v(-1, 0) * mm, "end": v(1, 0) * mm});
            skLineSegment(sketch, "E28.0.82.3", {"start": v(-1, -0.01) * mm, "end": v(-1, 0) * mm});
            skLineSegment(sketch, "E28.0.83.0", {"start": v(1, 0.01) * mm, "end": v(-1, 0.01) * mm});
            skLineSegment(sketch, "E28.0.83.1", {"start": v(1, 0) * mm, "end": v(1, 0.01) * mm});
            skLineSegment(sketch, "E28.0.83.2", {"start": v(-1, 0) * mm, "end": v(1, 0) * mm});
            skLineSegment(sketch, "E28.0.83.3", {"start": v(-1, 0) * mm, "end": v(-1, 0) * mm});
            skLineSegment(sketch, "E28.0.84.0", {"start": v(1, 0.02) * mm, "end": v(-1, 0.02) * mm});
            skLineSegment(sketch, "E28.0.84.1", {"start": v(1, 0.02) * mm, "end": v(1, 0.02) * mm});
            skLineSegment(sketch, "E28.0.84.2", {"start": v(-1, 0.02) * mm, "end": v(1, 0.02) * mm});
            skLineSegment(sketch, "E28.0.84.3", {"start": v(-1, 0.01) * mm, "end": v(-1, 0.02) * mm});
            skLineSegment(sketch, "E28.0.85.0", {"start": v(1, 0.04) * mm, "end": v(-1, 0.04) * mm});
            skLineSegment(sketch, "E28.0.85.1", {"start": v(1, 0.03) * mm, "end": v(1, 0.04) * mm});
            skLineSegment(sketch, "E28.0.85.2", {"start": v(-1, 0.03) * mm, "end": v(1, 0.03) * mm});
            skLineSegment(sketch, "E28.0.85.3", {"start": v(-1, 0.02) * mm, "end": v(-1, 0.03) * mm});
            skLineSegment(sketch, "E28.0.86.0", {"start": v(1, 0.05) * mm, "end": v(-1, 0.05) * mm});
            skLineSegment(sketch, "E28.0.86.1", {"start": v(1, 0.04) * mm, "end": v(1, 0.05) * mm});
            skLineSegment(sketch, "E28.0.86.2", {"start": v(-1, 0.04) * mm, "end": v(1, 0.04) * mm});
            skLineSegment(sketch, "E28.0.86.3", {"start": v(-1, 0.04) * mm, "end": v(-1, 0.04) * mm});
            skLineSegment(sketch, "E28.0.87.0", {"start": v(1, 0.06) * mm, "end": v(-1, 0.06) * mm});
            skLineSegment(sketch, "E28.0.87.1", {"start": v(1, 0.06) * mm, "end": v(1, 0.06) * mm});
            skLineSegment(sketch, "E28.0.87.2", {"start": v(-1, 0.06) * mm, "end": v(1, 0.06) * mm});
            skLineSegment(sketch, "E28.0.87.3", {"start": v(-1, 0.05) * mm, "end": v(-1, 0.06) * mm});
            skLineSegment(sketch, "E28.0.88.0", {"start": v(1, 0.07) * mm, "end": v(-1, 0.07) * mm});
            skLineSegment(sketch, "E28.0.88.1", {"start": v(1, 0.07) * mm, "end": v(1, 0.07) * mm});
            skLineSegment(sketch, "E28.0.88.2", {"start": v(-1, 0.07) * mm, "end": v(1, 0.07) * mm});
            skLineSegment(sketch, "E28.0.88.3", {"start": v(-1, 0.06) * mm, "end": v(-1, 0.07) * mm});
            skLineSegment(sketch, "E28.0.89.0", {"start": v(1, 0.08) * mm, "end": v(-1, 0.08) * mm});
            skLineSegment(sketch, "E28.0.89.1", {"start": v(1, 0.08) * mm, "end": v(1, 0.08) * mm});
            skLineSegment(sketch, "E28.0.89.2", {"start": v(-1, 0.08) * mm, "end": v(1, 0.08) * mm});
            skLineSegment(sketch, "E28.0.89.3", {"start": v(-1, 0.07) * mm, "end": v(-1, 0.08) * mm});
            skLineSegment(sketch, "E28.0.90.0", {"start": v(1, 0.1) * mm, "end": v(-1, 0.1) * mm});
            skLineSegment(sketch, "E28.0.90.1", {"start": v(1, 0.1) * mm, "end": v(1, 0.1) * mm});
            skLineSegment(sketch, "E28.0.90.2", {"start": v(-1, 0.1) * mm, "end": v(1, 0.1) * mm});
            skLineSegment(sketch, "E28.0.90.3", {"start": v(-1, 0.08) * mm, "end": v(-1, 0.1) * mm});
            skLineSegment(sketch, "E28.0.91.0", {"start": v(1, 0.1) * mm, "end": v(-1, 0.1) * mm});
            skLineSegment(sketch, "E28.0.91.1", {"start": v(1, 0.1) * mm, "end": v(1, 0.1) * mm});
            skLineSegment(sketch, "E28.0.91.2", {"start": v(-1, 0.1) * mm, "end": v(1, 0.1) * mm});
            skLineSegment(sketch, "E28.0.91.3", {"start": v(-1, 0.1) * mm, "end": v(-1, 0.1) * mm});
            skLineSegment(sketch, "E28.0.92.0", {"start": v(1, 0.12) * mm, "end": v(-1, 0.12) * mm});
            skLineSegment(sketch, "E28.0.92.1", {"start": v(1, 0.12) * mm, "end": v(1, 0.12) * mm});
            skLineSegment(sketch, "E28.0.92.2", {"start": v(-1, 0.12) * mm, "end": v(1, 0.12) * mm});
            skLineSegment(sketch, "E28.0.92.3", {"start": v(-1, 0.1) * mm, "end": v(-1, 0.12) * mm});
            skLineSegment(sketch, "E28.0.93.0", {"start": v(1, 0.13) * mm, "end": v(-1, 0.13) * mm});
            skLineSegment(sketch, "E28.0.93.1", {"start": v(1, 0.13) * mm, "end": v(1, 0.13) * mm});
            skLineSegment(sketch, "E28.0.93.2", {"start": v(-1, 0.13) * mm, "end": v(1, 0.13) * mm});
            skLineSegment(sketch, "E28.0.93.3", {"start": v(-1, 0.12) * mm, "end": v(-1, 0.13) * mm});
            skLineSegment(sketch, "E28.0.94.0", {"start": v(1, 0.14) * mm, "end": v(-1, 0.14) * mm});
            skLineSegment(sketch, "E28.0.94.1", {"start": v(1, 0.14) * mm, "end": v(1, 0.14) * mm});
            skLineSegment(sketch, "E28.0.94.2", {"start": v(-1, 0.14) * mm, "end": v(1, 0.14) * mm});
            skLineSegment(sketch, "E28.0.94.3", {"start": v(-1, 0.13) * mm, "end": v(-1, 0.14) * mm});
            skLineSegment(sketch, "E28.0.95.0", {"start": v(1, 0.16) * mm, "end": v(-1, 0.16) * mm});
            skLineSegment(sketch, "E28.0.95.1", {"start": v(1, 0.15) * mm, "end": v(1, 0.16) * mm});
            skLineSegment(sketch, "E28.0.95.2", {"start": v(-1, 0.15) * mm, "end": v(1, 0.15) * mm});
            skLineSegment(sketch, "E28.0.95.3", {"start": v(-1, 0.14) * mm, "end": v(-1, 0.15) * mm});
            skLineSegment(sketch, "E28.0.96.0", {"start": v(1, 0.17) * mm, "end": v(-1, 0.17) * mm});
            skLineSegment(sketch, "E28.0.96.1", {"start": v(1, 0.16) * mm, "end": v(1, 0.17) * mm});
            skLineSegment(sketch, "E28.0.96.2", {"start": v(-1, 0.16) * mm, "end": v(1, 0.16) * mm});
            skLineSegment(sketch, "E28.0.96.3", {"start": v(-1, 0.16) * mm, "end": v(-1, 0.16) * mm});
            skLineSegment(sketch, "E28.0.97.0", {"start": v(1, 0.18) * mm, "end": v(-1, 0.18) * mm});
            skLineSegment(sketch, "E28.0.97.1", {"start": v(1, 0.18) * mm, "end": v(1, 0.18) * mm});
            skLineSegment(sketch, "E28.0.97.2", {"start": v(-1, 0.18) * mm, "end": v(1, 0.18) * mm});
            skLineSegment(sketch, "E28.0.97.3", {"start": v(-1, 0.17) * mm, "end": v(-1, 0.18) * mm});
            skLineSegment(sketch, "E28.0.98.0", {"start": v(1, 0.2) * mm, "end": v(-1, 0.2) * mm});
            skLineSegment(sketch, "E28.0.98.1", {"start": v(1, 0.19) * mm, "end": v(1, 0.2) * mm});
            skLineSegment(sketch, "E28.0.98.2", {"start": v(-1, 0.19) * mm, "end": v(1, 0.19) * mm});
            skLineSegment(sketch, "E28.0.98.3", {"start": v(-1, 0.18) * mm, "end": v(-1, 0.19) * mm});
            skLineSegment(sketch, "E28.0.99.0", {"start": v(1, 0.2) * mm, "end": v(-1, 0.2) * mm});
            skLineSegment(sketch, "E28.0.99.1", {"start": v(1, 0.2) * mm, "end": v(1, 0.2) * mm});
            skLineSegment(sketch, "E28.0.99.2", {"start": v(-1, 0.2) * mm, "end": v(1, 0.2) * mm});
            skLineSegment(sketch, "E28.0.99.3", {"start": v(-1, 0.2) * mm, "end": v(-1, 0.2) * mm});
            skLineSegment(sketch, "E28.direction1", {"start": v(-1, -0.98) * mm, "end": v(24, -0.98) * mm, "construction": true});
            skLineSegment(sketch, "E28.direction2", {"start": v(-1, -0.98) * mm, "end": v(-1, -0.97) * mm, "construction": true});
            skLineSegment(sketch, "E29.0.1.2", {"start": v(-1, -0.97) * mm, "end": v(1, -0.97) * mm});
            skLineSegment(sketch, "E29.0.1.3", {"start": v(-1, -0.97) * mm, "end": v(-1, -0.97) * mm});
            skLineSegment(sketch, "E29.0.4.0", {"start": v(1, -0.94) * mm, "end": v(1, -0.93) * mm});
            skLineSegment(sketch, "E29.0.4.1", {"start": v(1, -0.93) * mm, "end": v(-1, -0.93) * mm});
            skLineSegment(sketch, "E29.0.4.3", {"start": v(-1, -0.93) * mm, "end": v(-1, -0.93) * mm});
            skLineSegment(sketch, "E29.0.6.0", {"start": v(1, -0.92) * mm, "end": v(1, -0.9) * mm});
            skLineSegment(sketch, "E29.0.9.0", {"start": v(1, -0.88) * mm, "end": v(1, -0.87) * mm});
            skLineSegment(sketch, "E29.0.9.1", {"start": v(1, -0.87) * mm, "end": v(-1, -0.87) * mm});
            skLineSegment(sketch, "E29.0.9.3", {"start": v(-1, -0.87) * mm, "end": v(-1, -0.87) * mm});
            skLineSegment(sketch, "E29.0.14.0", {"start": v(1, -0.82) * mm, "end": v(1, -0.81) * mm});
            skLineSegment(sketch, "E29.0.14.1", {"start": v(1, -0.81) * mm, "end": v(-1, -0.81) * mm});
            skLineSegment(sketch, "E29.0.14.3", {"start": v(-1, -0.81) * mm, "end": v(-1, -0.8) * mm});
            skLineSegment(sketch, "E29.0.16.0", {"start": v(1, -0.8) * mm, "end": v(1, -0.79) * mm});
            skLineSegment(sketch, "E29.0.16.1", {"start": v(1, -0.79) * mm, "end": v(-1, -0.79) * mm});
            skLineSegment(sketch, "E29.0.16.3", {"start": v(-1, -0.79) * mm, "end": v(-1, -0.78) * mm});
            skLineSegment(sketch, "E29.0.19.0", {"start": v(1, -0.76) * mm, "end": v(1, -0.75) * mm});
            skLineSegment(sketch, "E29.0.19.1", {"start": v(1, -0.75) * mm, "end": v(-1, -0.75) * mm});
            skLineSegment(sketch, "E29.0.19.3", {"start": v(-1, -0.75) * mm, "end": v(-1, -0.75) * mm});
            skLineSegment(sketch, "E29.0.29.0", {"start": v(1, -0.64) * mm, "end": v(1, -0.63) * mm});
            skLineSegment(sketch, "E29.0.29.1", {"start": v(1, -0.63) * mm, "end": v(-1, -0.63) * mm});
            skLineSegment(sketch, "E29.0.29.3", {"start": v(-1, -0.63) * mm, "end": v(-1, -0.63) * mm});
            skLineSegment(sketch, "E29.0.31.0", {"start": v(1, -0.62) * mm, "end": v(1, -0.6) * mm});
            skLineSegment(sketch, "E29.0.34.0", {"start": v(1, -0.58) * mm, "end": v(1, -0.57) * mm});
            skLineSegment(sketch, "E29.0.34.1", {"start": v(1, -0.57) * mm, "end": v(-1, -0.57) * mm});
            skLineSegment(sketch, "E29.0.34.3", {"start": v(-1, -0.57) * mm, "end": v(-1, -0.57) * mm});
            skLineSegment(sketch, "E29.0.39.0", {"start": v(1, -0.52) * mm, "end": v(1, -0.51) * mm});
            skLineSegment(sketch, "E29.0.39.1", {"start": v(1, -0.51) * mm, "end": v(-1, -0.51) * mm});
            skLineSegment(sketch, "E29.0.39.3", {"start": v(-1, -0.51) * mm, "end": v(-1, -0.5) * mm});
            skLineSegment(sketch, "E29.0.41.0", {"start": v(1, -0.5) * mm, "end": v(1, -0.49) * mm});
            skLineSegment(sketch, "E29.0.41.1", {"start": v(1, -0.49) * mm, "end": v(-1, -0.49) * mm});
            skLineSegment(sketch, "E29.0.41.3", {"start": v(-1, -0.49) * mm, "end": v(-1, -0.48) * mm});
            skLineSegment(sketch, "E29.0.44.0", {"start": v(1, -0.46) * mm, "end": v(1, -0.45) * mm});
            skLineSegment(sketch, "E29.0.44.1", {"start": v(1, -0.45) * mm, "end": v(-1, -0.45) * mm});
            skLineSegment(sketch, "E29.0.44.3", {"start": v(-1, -0.45) * mm, "end": v(-1, -0.45) * mm});
            skLineSegment(sketch, "E29.0.54.0", {"start": v(1, -0.34) * mm, "end": v(1, -0.33) * mm});
            skLineSegment(sketch, "E29.0.54.1", {"start": v(1, -0.33) * mm, "end": v(-1, -0.33) * mm});
            skLineSegment(sketch, "E29.0.54.3", {"start": v(-1, -0.33) * mm, "end": v(-1, -0.33) * mm});
            skLineSegment(sketch, "E29.0.56.0", {"start": v(1, -0.32) * mm, "end": v(1, -0.3) * mm});
            skLineSegment(sketch, "E29.0.59.0", {"start": v(1, -0.28) * mm, "end": v(1, -0.27) * mm});
            skLineSegment(sketch, "E29.0.59.1", {"start": v(1, -0.27) * mm, "end": v(-1, -0.27) * mm});
            skLineSegment(sketch, "E29.0.59.3", {"start": v(-1, -0.27) * mm, "end": v(-1, -0.27) * mm});
            skLineSegment(sketch, "E29.0.64.0", {"start": v(1, -0.22) * mm, "end": v(1, -0.21) * mm});
            skLineSegment(sketch, "E29.0.64.1", {"start": v(1, -0.21) * mm, "end": v(-1, -0.21) * mm});
            skLineSegment(sketch, "E29.0.64.3", {"start": v(-1, -0.21) * mm, "end": v(-1, -0.2) * mm});
            skLineSegment(sketch, "E29.0.66.0", {"start": v(1, -0.2) * mm, "end": v(1, -0.19) * mm});
            skLineSegment(sketch, "E29.0.66.1", {"start": v(1, -0.19) * mm, "end": v(-1, -0.19) * mm});
            skLineSegment(sketch, "E29.0.66.3", {"start": v(-1, -0.19) * mm, "end": v(-1, -0.18) * mm});
            skLineSegment(sketch, "E29.0.69.0", {"start": v(1, -0.16) * mm, "end": v(1, -0.15) * mm});
            skLineSegment(sketch, "E29.0.69.1", {"start": v(1, -0.15) * mm, "end": v(-1, -0.15) * mm});
            skLineSegment(sketch, "E29.0.69.3", {"start": v(-1, -0.15) * mm, "end": v(-1, -0.15) * mm});
            skLineSegment(sketch, "E29.0.79.0", {"start": v(1, -0.04) * mm, "end": v(1, -0.03) * mm});
            skLineSegment(sketch, "E29.0.79.1", {"start": v(1, -0.03) * mm, "end": v(-1, -0.03) * mm});
            skLineSegment(sketch, "E29.0.79.3", {"start": v(-1, -0.03) * mm, "end": v(-1, -0.03) * mm});
            skLineSegment(sketch, "E29.0.81.0", {"start": v(1, -0.02) * mm, "end": v(1, 0) * mm});
            skLineSegment(sketch, "E29.0.84.0", {"start": v(1, 0.02) * mm, "end": v(1, 0.03) * mm});
            skLineSegment(sketch, "E29.0.84.1", {"start": v(1, 0.03) * mm, "end": v(-1, 0.03) * mm});
            skLineSegment(sketch, "E29.0.84.3", {"start": v(-1, 0.03) * mm, "end": v(-1, 0.03) * mm});
            skLineSegment(sketch, "E29.0.89.0", {"start": v(1, 0.08) * mm, "end": v(1, 0.09) * mm});
            skLineSegment(sketch, "E29.0.89.1", {"start": v(1, 0.09) * mm, "end": v(-1, 0.09) * mm});
            skLineSegment(sketch, "E29.0.89.3", {"start": v(-1, 0.09) * mm, "end": v(-1, 0.1) * mm});
            skLineSegment(sketch, "E29.0.91.0", {"start": v(1, 0.1) * mm, "end": v(1, 0.11) * mm});
            skLineSegment(sketch, "E29.0.91.1", {"start": v(1, 0.11) * mm, "end": v(-1, 0.11) * mm});
            skLineSegment(sketch, "E29.0.91.3", {"start": v(-1, 0.11) * mm, "end": v(-1, 0.12) * mm});
            skLineSegment(sketch, "E29.0.94.0", {"start": v(1, 0.14) * mm, "end": v(1, 0.15) * mm});
            skLineSegment(sketch, "E29.0.94.1", {"start": v(1, 0.15) * mm, "end": v(-1, 0.15) * mm});
            skLineSegment(sketch, "E29.0.94.3", {"start": v(-1, 0.15) * mm, "end": v(-1, 0.15) * mm});
            skLineSegment(sketch, "E29.0.99.2", {"start": v(-1, 0.21) * mm, "end": v(1, 0.21) * mm});
            skLineSegment(sketch, "E29.0.99.3", {"start": v(-1, 0.2) * mm, "end": v(-1, 0.21) * mm});
            skLineSegment(sketch, "E29.direction1", {"start": v(1, -0.99) * mm, "end": v(26, -0.99) * mm, "construction": true});
            skLineSegment(sketch, "E29.direction2", {"start": v(1, -0.99) * mm, "end": v(1, -0.98) * mm, "construction": true});
            skLineSegment(sketch, "E30.0.1.0", {"start": v(-1, 0.22) * mm, "end": v(1, 0.22) * mm});
            skLineSegment(sketch, "E30.0.1.1", {"start": v(1, 0.22) * mm, "end": v(-1, 0.22) * mm});
            skLineSegment(sketch, "E30.0.1.2", {"start": v(1, 0.21) * mm, "end": v(1, 0.22) * mm});
            skLineSegment(sketch, "E30.0.1.3", {"start": v(-1, 0.22) * mm, "end": v(-1, 0.22) * mm});
            skLineSegment(sketch, "E30.0.2.0", {"start": v(-1, 0.24) * mm, "end": v(1, 0.24) * mm});
            skLineSegment(sketch, "E30.0.2.1", {"start": v(1, 0.23) * mm, "end": v(-1, 0.23) * mm});
            skLineSegment(sketch, "E30.0.2.2", {"start": v(1, 0.22) * mm, "end": v(1, 0.23) * mm});
            skLineSegment(sketch, "E30.0.2.3", {"start": v(-1, 0.23) * mm, "end": v(-1, 0.24) * mm});
            skLineSegment(sketch, "E30.0.3.0", {"start": v(-1, 0.25) * mm, "end": v(1, 0.25) * mm});
            skLineSegment(sketch, "E30.0.3.1", {"start": v(1, 0.24) * mm, "end": v(-1, 0.24) * mm});
            skLineSegment(sketch, "E30.0.3.2", {"start": v(1, 0.24) * mm, "end": v(1, 0.24) * mm});
            skLineSegment(sketch, "E30.0.3.3", {"start": v(-1, 0.24) * mm, "end": v(-1, 0.25) * mm});
            skLineSegment(sketch, "E30.0.4.0", {"start": v(-1, 0.26) * mm, "end": v(1, 0.26) * mm});
            skLineSegment(sketch, "E30.0.4.1", {"start": v(1, 0.25) * mm, "end": v(-1, 0.25) * mm});
            skLineSegment(sketch, "E30.0.4.2", {"start": v(1, 0.25) * mm, "end": v(1, 0.25) * mm});
            skLineSegment(sketch, "E30.0.4.3", {"start": v(-1, 0.25) * mm, "end": v(-1, 0.26) * mm});
            skLineSegment(sketch, "E30.0.5.0", {"start": v(-1, 0.27) * mm, "end": v(1, 0.27) * mm});
            skLineSegment(sketch, "E30.0.5.1", {"start": v(1, 0.27) * mm, "end": v(-1, 0.27) * mm});
            skLineSegment(sketch, "E30.0.5.2", {"start": v(1, 0.26) * mm, "end": v(1, 0.27) * mm});
            skLineSegment(sketch, "E30.0.5.3", {"start": v(-1, 0.27) * mm, "end": v(-1, 0.27) * mm});
            skLineSegment(sketch, "E30.0.6.0", {"start": v(-1, 0.28) * mm, "end": v(1, 0.28) * mm});
            skLineSegment(sketch, "E30.0.6.1", {"start": v(1, 0.28) * mm, "end": v(-1, 0.28) * mm});
            skLineSegment(sketch, "E30.0.6.2", {"start": v(1, 0.27) * mm, "end": v(1, 0.28) * mm});
            skLineSegment(sketch, "E30.0.6.3", {"start": v(-1, 0.28) * mm, "end": v(-1, 0.28) * mm});
            skLineSegment(sketch, "E30.0.7.0", {"start": v(-1, 0.3) * mm, "end": v(1, 0.3) * mm});
            skLineSegment(sketch, "E30.0.7.1", {"start": v(1, 0.3) * mm, "end": v(-1, 0.3) * mm});
            skLineSegment(sketch, "E30.0.7.2", {"start": v(1, 0.28) * mm, "end": v(1, 0.3) * mm});
            skLineSegment(sketch, "E30.0.7.3", {"start": v(-1, 0.3) * mm, "end": v(-1, 0.3) * mm});
            skLineSegment(sketch, "E30.0.8.0", {"start": v(-1, 0.3) * mm, "end": v(1, 0.3) * mm});
            skLineSegment(sketch, "E30.0.8.1", {"start": v(1, 0.3) * mm, "end": v(-1, 0.3) * mm});
            skLineSegment(sketch, "E30.0.8.2", {"start": v(1, 0.3) * mm, "end": v(1, 0.3) * mm});
            skLineSegment(sketch, "E30.0.8.3", {"start": v(-1, 0.3) * mm, "end": v(-1, 0.3) * mm});
            skLineSegment(sketch, "E30.0.9.0", {"start": v(-1, 0.32) * mm, "end": v(1, 0.32) * mm});
            skLineSegment(sketch, "E30.0.9.1", {"start": v(1, 0.31) * mm, "end": v(-1, 0.31) * mm});
            skLineSegment(sketch, "E30.0.9.2", {"start": v(1, 0.3) * mm, "end": v(1, 0.31) * mm});
            skLineSegment(sketch, "E30.0.9.3", {"start": v(-1, 0.31) * mm, "end": v(-1, 0.32) * mm});
            skLineSegment(sketch, "E30.0.10.0", {"start": v(-1, 0.33) * mm, "end": v(1, 0.33) * mm});
            skLineSegment(sketch, "E30.0.10.1", {"start": v(1, 0.33) * mm, "end": v(-1, 0.33) * mm});
            skLineSegment(sketch, "E30.0.10.2", {"start": v(1, 0.32) * mm, "end": v(1, 0.33) * mm});
            skLineSegment(sketch, "E30.0.10.3", {"start": v(-1, 0.33) * mm, "end": v(-1, 0.33) * mm});
            skLineSegment(sketch, "E30.0.11.0", {"start": v(-1, 0.34) * mm, "end": v(1, 0.34) * mm});
            skLineSegment(sketch, "E30.0.11.1", {"start": v(1, 0.34) * mm, "end": v(-1, 0.34) * mm});
            skLineSegment(sketch, "E30.0.11.2", {"start": v(1, 0.33) * mm, "end": v(1, 0.34) * mm});
            skLineSegment(sketch, "E30.0.11.3", {"start": v(-1, 0.34) * mm, "end": v(-1, 0.34) * mm});
            skLineSegment(sketch, "E30.0.12.0", {"start": v(-1, 0.36) * mm, "end": v(1, 0.36) * mm});
            skLineSegment(sketch, "E30.0.12.1", {"start": v(1, 0.35) * mm, "end": v(-1, 0.35) * mm});
            skLineSegment(sketch, "E30.0.12.2", {"start": v(1, 0.34) * mm, "end": v(1, 0.35) * mm});
            skLineSegment(sketch, "E30.0.12.3", {"start": v(-1, 0.35) * mm, "end": v(-1, 0.36) * mm});
            skLineSegment(sketch, "E30.0.13.0", {"start": v(-1, 0.37) * mm, "end": v(1, 0.37) * mm});
            skLineSegment(sketch, "E30.0.13.1", {"start": v(1, 0.36) * mm, "end": v(-1, 0.36) * mm});
            skLineSegment(sketch, "E30.0.13.2", {"start": v(1, 0.36) * mm, "end": v(1, 0.36) * mm});
            skLineSegment(sketch, "E30.0.13.3", {"start": v(-1, 0.36) * mm, "end": v(-1, 0.37) * mm});
            skLineSegment(sketch, "E30.0.14.0", {"start": v(-1, 0.38) * mm, "end": v(1, 0.38) * mm});
            skLineSegment(sketch, "E30.0.14.1", {"start": v(1, 0.37) * mm, "end": v(-1, 0.37) * mm});
            skLineSegment(sketch, "E30.0.14.2", {"start": v(1, 0.37) * mm, "end": v(1, 0.37) * mm});
            skLineSegment(sketch, "E30.0.14.3", {"start": v(-1, 0.37) * mm, "end": v(-1, 0.38) * mm});
            skLineSegment(sketch, "E30.0.15.0", {"start": v(-1, 0.4) * mm, "end": v(1, 0.4) * mm});
            skLineSegment(sketch, "E30.0.15.1", {"start": v(1, 0.39) * mm, "end": v(-1, 0.39) * mm});
            skLineSegment(sketch, "E30.0.15.2", {"start": v(1, 0.38) * mm, "end": v(1, 0.39) * mm});
            skLineSegment(sketch, "E30.0.15.3", {"start": v(-1, 0.39) * mm, "end": v(-1, 0.4) * mm});
            skLineSegment(sketch, "E30.0.16.0", {"start": v(-1, 0.4) * mm, "end": v(1, 0.4) * mm});
            skLineSegment(sketch, "E30.0.16.1", {"start": v(1, 0.4) * mm, "end": v(-1, 0.4) * mm});
            skLineSegment(sketch, "E30.0.16.2", {"start": v(1, 0.4) * mm, "end": v(1, 0.4) * mm});
            skLineSegment(sketch, "E30.0.16.3", {"start": v(-1, 0.4) * mm, "end": v(-1, 0.4) * mm});
            skLineSegment(sketch, "E30.0.17.0", {"start": v(-1, 0.42) * mm, "end": v(1, 0.42) * mm});
            skLineSegment(sketch, "E30.0.17.1", {"start": v(1, 0.41) * mm, "end": v(-1, 0.41) * mm});
            skLineSegment(sketch, "E30.0.17.2", {"start": v(1, 0.4) * mm, "end": v(1, 0.41) * mm});
            skLineSegment(sketch, "E30.0.17.3", {"start": v(-1, 0.41) * mm, "end": v(-1, 0.42) * mm});
            skLineSegment(sketch, "E30.0.18.0", {"start": v(-1, 0.43) * mm, "end": v(1, 0.43) * mm});
            skLineSegment(sketch, "E30.0.18.1", {"start": v(1, 0.42) * mm, "end": v(-1, 0.42) * mm});
            skLineSegment(sketch, "E30.0.18.2", {"start": v(1, 0.42) * mm, "end": v(1, 0.42) * mm});
            skLineSegment(sketch, "E30.0.18.3", {"start": v(-1, 0.42) * mm, "end": v(-1, 0.43) * mm});
            skLineSegment(sketch, "E30.0.19.0", {"start": v(-1, 0.44) * mm, "end": v(1, 0.44) * mm});
            skLineSegment(sketch, "E30.0.19.1", {"start": v(1, 0.43) * mm, "end": v(-1, 0.43) * mm});
            skLineSegment(sketch, "E30.0.19.2", {"start": v(1, 0.43) * mm, "end": v(1, 0.43) * mm});
            skLineSegment(sketch, "E30.0.19.3", {"start": v(-1, 0.43) * mm, "end": v(-1, 0.44) * mm});
            skLineSegment(sketch, "E30.0.20.0", {"start": v(-1, 0.45) * mm, "end": v(1, 0.45) * mm});
            skLineSegment(sketch, "E30.0.20.1", {"start": v(1, 0.45) * mm, "end": v(-1, 0.45) * mm});
            skLineSegment(sketch, "E30.0.20.2", {"start": v(1, 0.44) * mm, "end": v(1, 0.45) * mm});
            skLineSegment(sketch, "E30.0.20.3", {"start": v(-1, 0.45) * mm, "end": v(-1, 0.45) * mm});
            skLineSegment(sketch, "E30.0.21.0", {"start": v(-1, 0.46) * mm, "end": v(1, 0.46) * mm});
            skLineSegment(sketch, "E30.0.21.1", {"start": v(1, 0.46) * mm, "end": v(-1, 0.46) * mm});
            skLineSegment(sketch, "E30.0.21.2", {"start": v(1, 0.45) * mm, "end": v(1, 0.46) * mm});
            skLineSegment(sketch, "E30.0.21.3", {"start": v(-1, 0.46) * mm, "end": v(-1, 0.46) * mm});
            skLineSegment(sketch, "E30.0.22.0", {"start": v(-1, 0.48) * mm, "end": v(1, 0.48) * mm});
            skLineSegment(sketch, "E30.0.22.1", {"start": v(1, 0.47) * mm, "end": v(-1, 0.47) * mm});
            skLineSegment(sketch, "E30.0.22.2", {"start": v(1, 0.46) * mm, "end": v(1, 0.47) * mm});
            skLineSegment(sketch, "E30.0.22.3", {"start": v(-1, 0.47) * mm, "end": v(-1, 0.48) * mm});
            skLineSegment(sketch, "E30.0.23.0", {"start": v(-1, 0.49) * mm, "end": v(1, 0.49) * mm});
            skLineSegment(sketch, "E30.0.23.1", {"start": v(1, 0.48) * mm, "end": v(-1, 0.48) * mm});
            skLineSegment(sketch, "E30.0.23.2", {"start": v(1, 0.48) * mm, "end": v(1, 0.48) * mm});
            skLineSegment(sketch, "E30.0.23.3", {"start": v(-1, 0.48) * mm, "end": v(-1, 0.49) * mm});
            skLineSegment(sketch, "E30.0.24.0", {"start": v(-1, 0.5) * mm, "end": v(1, 0.5) * mm});
            skLineSegment(sketch, "E30.0.24.1", {"start": v(1, 0.5) * mm, "end": v(-1, 0.5) * mm});
            skLineSegment(sketch, "E30.0.24.2", {"start": v(1, 0.49) * mm, "end": v(1, 0.5) * mm});
            skLineSegment(sketch, "E30.0.24.3", {"start": v(-1, 0.5) * mm, "end": v(-1, 0.5) * mm});
            skLineSegment(sketch, "E30.0.25.0", {"start": v(-1, 0.51) * mm, "end": v(1, 0.51) * mm});
            skLineSegment(sketch, "E30.0.25.1", {"start": v(1, 0.5) * mm, "end": v(-1, 0.5) * mm});
            skLineSegment(sketch, "E30.0.25.2", {"start": v(1, 0.5) * mm, "end": v(1, 0.5) * mm});
            skLineSegment(sketch, "E30.0.25.3", {"start": v(-1, 0.5) * mm, "end": v(-1, 0.51) * mm});
            skLineSegment(sketch, "E30.0.26.0", {"start": v(-1, 0.52) * mm, "end": v(1, 0.52) * mm});
            skLineSegment(sketch, "E30.0.26.1", {"start": v(1, 0.52) * mm, "end": v(-1, 0.52) * mm});
            skLineSegment(sketch, "E30.0.26.2", {"start": v(1, 0.51) * mm, "end": v(1, 0.52) * mm});
            skLineSegment(sketch, "E30.0.26.3", {"start": v(-1, 0.52) * mm, "end": v(-1, 0.52) * mm});
            skLineSegment(sketch, "E30.0.27.0", {"start": v(-1, 0.54) * mm, "end": v(1, 0.54) * mm});
            skLineSegment(sketch, "E30.0.27.1", {"start": v(1, 0.53) * mm, "end": v(-1, 0.53) * mm});
            skLineSegment(sketch, "E30.0.27.2", {"start": v(1, 0.52) * mm, "end": v(1, 0.53) * mm});
            skLineSegment(sketch, "E30.0.27.3", {"start": v(-1, 0.53) * mm, "end": v(-1, 0.54) * mm});
            skLineSegment(sketch, "E30.0.28.0", {"start": v(-1, 0.55) * mm, "end": v(1, 0.55) * mm});
            skLineSegment(sketch, "E30.0.28.1", {"start": v(1, 0.54) * mm, "end": v(-1, 0.54) * mm});
            skLineSegment(sketch, "E30.0.28.2", {"start": v(1, 0.54) * mm, "end": v(1, 0.54) * mm});
            skLineSegment(sketch, "E30.0.28.3", {"start": v(-1, 0.54) * mm, "end": v(-1, 0.55) * mm});
            skLineSegment(sketch, "E30.0.29.0", {"start": v(-1, 0.56) * mm, "end": v(1, 0.56) * mm});
            skLineSegment(sketch, "E30.0.29.1", {"start": v(1, 0.55) * mm, "end": v(-1, 0.55) * mm});
            skLineSegment(sketch, "E30.0.29.2", {"start": v(1, 0.55) * mm, "end": v(1, 0.55) * mm});
            skLineSegment(sketch, "E30.0.29.3", {"start": v(-1, 0.55) * mm, "end": v(-1, 0.56) * mm});
            skLineSegment(sketch, "E30.0.30.0", {"start": v(-1, 0.57) * mm, "end": v(1, 0.57) * mm});
            skLineSegment(sketch, "E30.0.30.1", {"start": v(1, 0.57) * mm, "end": v(-1, 0.57) * mm});
            skLineSegment(sketch, "E30.0.30.2", {"start": v(1, 0.56) * mm, "end": v(1, 0.57) * mm});
            skLineSegment(sketch, "E30.0.30.3", {"start": v(-1, 0.57) * mm, "end": v(-1, 0.57) * mm});
            skLineSegment(sketch, "E30.0.31.0", {"start": v(-1, 0.58) * mm, "end": v(1, 0.58) * mm});
            skLineSegment(sketch, "E30.0.31.1", {"start": v(1, 0.58) * mm, "end": v(-1, 0.58) * mm});
            skLineSegment(sketch, "E30.0.31.2", {"start": v(1, 0.57) * mm, "end": v(1, 0.58) * mm});
            skLineSegment(sketch, "E30.0.31.3", {"start": v(-1, 0.58) * mm, "end": v(-1, 0.58) * mm});
            skLineSegment(sketch, "E30.0.32.0", {"start": v(-1, 0.6) * mm, "end": v(1, 0.6) * mm});
            skLineSegment(sketch, "E30.0.32.1", {"start": v(1, 0.6) * mm, "end": v(-1, 0.6) * mm});
            skLineSegment(sketch, "E30.0.32.2", {"start": v(1, 0.58) * mm, "end": v(1, 0.6) * mm});
            skLineSegment(sketch, "E30.0.32.3", {"start": v(-1, 0.6) * mm, "end": v(-1, 0.6) * mm});
            skLineSegment(sketch, "E30.0.33.0", {"start": v(-1, 0.6) * mm, "end": v(1, 0.6) * mm});
            skLineSegment(sketch, "E30.0.33.1", {"start": v(1, 0.6) * mm, "end": v(-1, 0.6) * mm});
            skLineSegment(sketch, "E30.0.33.2", {"start": v(1, 0.6) * mm, "end": v(1, 0.6) * mm});
            skLineSegment(sketch, "E30.0.33.3", {"start": v(-1, 0.6) * mm, "end": v(-1, 0.6) * mm});
            skLineSegment(sketch, "E30.0.34.0", {"start": v(-1, 0.62) * mm, "end": v(1, 0.62) * mm});
            skLineSegment(sketch, "E30.0.34.1", {"start": v(1, 0.61) * mm, "end": v(-1, 0.61) * mm});
            skLineSegment(sketch, "E30.0.34.2", {"start": v(1, 0.6) * mm, "end": v(1, 0.61) * mm});
            skLineSegment(sketch, "E30.0.34.3", {"start": v(-1, 0.61) * mm, "end": v(-1, 0.62) * mm});
            skLineSegment(sketch, "E30.0.35.0", {"start": v(-1, 0.63) * mm, "end": v(1, 0.63) * mm});
            skLineSegment(sketch, "E30.0.35.1", {"start": v(1, 0.63) * mm, "end": v(-1, 0.63) * mm});
            skLineSegment(sketch, "E30.0.35.2", {"start": v(1, 0.62) * mm, "end": v(1, 0.63) * mm});
            skLineSegment(sketch, "E30.0.35.3", {"start": v(-1, 0.63) * mm, "end": v(-1, 0.63) * mm});
            skLineSegment(sketch, "E30.0.36.0", {"start": v(-1, 0.64) * mm, "end": v(1, 0.64) * mm});
            skLineSegment(sketch, "E30.0.36.1", {"start": v(1, 0.64) * mm, "end": v(-1, 0.64) * mm});
            skLineSegment(sketch, "E30.0.36.2", {"start": v(1, 0.63) * mm, "end": v(1, 0.64) * mm});
            skLineSegment(sketch, "E30.0.36.3", {"start": v(-1, 0.64) * mm, "end": v(-1, 0.64) * mm});
            skLineSegment(sketch, "E30.0.37.0", {"start": v(-1, 0.66) * mm, "end": v(1, 0.66) * mm});
            skLineSegment(sketch, "E30.0.37.1", {"start": v(1, 0.65) * mm, "end": v(-1, 0.65) * mm});
            skLineSegment(sketch, "E30.0.37.2", {"start": v(1, 0.64) * mm, "end": v(1, 0.65) * mm});
            skLineSegment(sketch, "E30.0.37.3", {"start": v(-1, 0.65) * mm, "end": v(-1, 0.66) * mm});
            skLineSegment(sketch, "E30.0.38.0", {"start": v(-1, 0.67) * mm, "end": v(1, 0.67) * mm});
            skLineSegment(sketch, "E30.0.38.1", {"start": v(1, 0.66) * mm, "end": v(-1, 0.66) * mm});
            skLineSegment(sketch, "E30.0.38.2", {"start": v(1, 0.66) * mm, "end": v(1, 0.66) * mm});
            skLineSegment(sketch, "E30.0.38.3", {"start": v(-1, 0.66) * mm, "end": v(-1, 0.67) * mm});
            skLineSegment(sketch, "E30.0.39.0", {"start": v(-1, 0.68) * mm, "end": v(1, 0.68) * mm});
            skLineSegment(sketch, "E30.0.39.1", {"start": v(1, 0.67) * mm, "end": v(-1, 0.67) * mm});
            skLineSegment(sketch, "E30.0.39.2", {"start": v(1, 0.67) * mm, "end": v(1, 0.67) * mm});
            skLineSegment(sketch, "E30.0.39.3", {"start": v(-1, 0.67) * mm, "end": v(-1, 0.68) * mm});
            skLineSegment(sketch, "E30.0.40.0", {"start": v(-1, 0.7) * mm, "end": v(1, 0.7) * mm});
            skLineSegment(sketch, "E30.0.40.1", {"start": v(1, 0.69) * mm, "end": v(-1, 0.69) * mm});
            skLineSegment(sketch, "E30.0.40.2", {"start": v(1, 0.68) * mm, "end": v(1, 0.69) * mm});
            skLineSegment(sketch, "E30.0.40.3", {"start": v(-1, 0.69) * mm, "end": v(-1, 0.7) * mm});
            skLineSegment(sketch, "E30.0.41.0", {"start": v(-1, 0.7) * mm, "end": v(1, 0.7) * mm});
            skLineSegment(sketch, "E30.0.41.1", {"start": v(1, 0.7) * mm, "end": v(-1, 0.7) * mm});
            skLineSegment(sketch, "E30.0.41.2", {"start": v(1, 0.7) * mm, "end": v(1, 0.7) * mm});
            skLineSegment(sketch, "E30.0.41.3", {"start": v(-1, 0.7) * mm, "end": v(-1, 0.7) * mm});
            skLineSegment(sketch, "E30.0.42.0", {"start": v(-1, 0.72) * mm, "end": v(1, 0.72) * mm});
            skLineSegment(sketch, "E30.0.42.1", {"start": v(1, 0.71) * mm, "end": v(-1, 0.71) * mm});
            skLineSegment(sketch, "E30.0.42.2", {"start": v(1, 0.7) * mm, "end": v(1, 0.71) * mm});
            skLineSegment(sketch, "E30.0.42.3", {"start": v(-1, 0.71) * mm, "end": v(-1, 0.72) * mm});
            skLineSegment(sketch, "E30.0.43.0", {"start": v(-1, 0.73) * mm, "end": v(1, 0.73) * mm});
            skLineSegment(sketch, "E30.0.43.1", {"start": v(1, 0.72) * mm, "end": v(-1, 0.72) * mm});
            skLineSegment(sketch, "E30.0.43.2", {"start": v(1, 0.72) * mm, "end": v(1, 0.72) * mm});
            skLineSegment(sketch, "E30.0.43.3", {"start": v(-1, 0.72) * mm, "end": v(-1, 0.73) * mm});
            skLineSegment(sketch, "E30.0.44.0", {"start": v(-1, 0.74) * mm, "end": v(1, 0.74) * mm});
            skLineSegment(sketch, "E30.0.44.1", {"start": v(1, 0.73) * mm, "end": v(-1, 0.73) * mm});
            skLineSegment(sketch, "E30.0.44.2", {"start": v(1, 0.73) * mm, "end": v(1, 0.73) * mm});
            skLineSegment(sketch, "E30.0.44.3", {"start": v(-1, 0.73) * mm, "end": v(-1, 0.74) * mm});
            skLineSegment(sketch, "E30.0.45.0", {"start": v(-1, 0.75) * mm, "end": v(1, 0.75) * mm});
            skLineSegment(sketch, "E30.0.45.1", {"start": v(1, 0.75) * mm, "end": v(-1, 0.75) * mm});
            skLineSegment(sketch, "E30.0.45.2", {"start": v(1, 0.74) * mm, "end": v(1, 0.75) * mm});
            skLineSegment(sketch, "E30.0.45.3", {"start": v(-1, 0.75) * mm, "end": v(-1, 0.75) * mm});
            skLineSegment(sketch, "E30.0.46.0", {"start": v(-1, 0.76) * mm, "end": v(1, 0.76) * mm});
            skLineSegment(sketch, "E30.0.46.1", {"start": v(1, 0.76) * mm, "end": v(-1, 0.76) * mm});
            skLineSegment(sketch, "E30.0.46.2", {"start": v(1, 0.75) * mm, "end": v(1, 0.76) * mm});
            skLineSegment(sketch, "E30.0.46.3", {"start": v(-1, 0.76) * mm, "end": v(-1, 0.76) * mm});
            skLineSegment(sketch, "E30.0.47.0", {"start": v(-1, 0.78) * mm, "end": v(1, 0.78) * mm});
            skLineSegment(sketch, "E30.0.47.1", {"start": v(1, 0.77) * mm, "end": v(-1, 0.77) * mm});
            skLineSegment(sketch, "E30.0.47.2", {"start": v(1, 0.76) * mm, "end": v(1, 0.77) * mm});
            skLineSegment(sketch, "E30.0.47.3", {"start": v(-1, 0.77) * mm, "end": v(-1, 0.78) * mm});
            skLineSegment(sketch, "E30.0.48.0", {"start": v(-1, 0.79) * mm, "end": v(1, 0.79) * mm});
            skLineSegment(sketch, "E30.0.48.1", {"start": v(1, 0.78) * mm, "end": v(-1, 0.78) * mm});
            skLineSegment(sketch, "E30.0.48.2", {"start": v(1, 0.78) * mm, "end": v(1, 0.78) * mm});
            skLineSegment(sketch, "E30.0.48.3", {"start": v(-1, 0.78) * mm, "end": v(-1, 0.79) * mm});
            skLineSegment(sketch, "E30.0.49.0", {"start": v(-1, 0.8) * mm, "end": v(1, 0.8) * mm});
            skLineSegment(sketch, "E30.0.49.1", {"start": v(1, 0.8) * mm, "end": v(-1, 0.8) * mm});
            skLineSegment(sketch, "E30.0.49.2", {"start": v(1, 0.79) * mm, "end": v(1, 0.8) * mm});
            skLineSegment(sketch, "E30.0.49.3", {"start": v(-1, 0.8) * mm, "end": v(-1, 0.8) * mm});
            skLineSegment(sketch, "E30.0.50.0", {"start": v(-1, 0.81) * mm, "end": v(1, 0.81) * mm});
            skLineSegment(sketch, "E30.0.50.1", {"start": v(1, 0.8) * mm, "end": v(-1, 0.8) * mm});
            skLineSegment(sketch, "E30.0.50.2", {"start": v(1, 0.8) * mm, "end": v(1, 0.8) * mm});
            skLineSegment(sketch, "E30.0.50.3", {"start": v(-1, 0.8) * mm, "end": v(-1, 0.81) * mm});
            skLineSegment(sketch, "E30.0.51.0", {"start": v(-1, 0.82) * mm, "end": v(1, 0.82) * mm});
            skLineSegment(sketch, "E30.0.51.1", {"start": v(1, 0.82) * mm, "end": v(-1, 0.82) * mm});
            skLineSegment(sketch, "E30.0.51.2", {"start": v(1, 0.81) * mm, "end": v(1, 0.82) * mm});
            skLineSegment(sketch, "E30.0.51.3", {"start": v(-1, 0.82) * mm, "end": v(-1, 0.82) * mm});
            skLineSegment(sketch, "E30.0.52.0", {"start": v(-1, 0.84) * mm, "end": v(1, 0.84) * mm});
            skLineSegment(sketch, "E30.0.52.1", {"start": v(1, 0.83) * mm, "end": v(-1, 0.83) * mm});
            skLineSegment(sketch, "E30.0.52.2", {"start": v(1, 0.82) * mm, "end": v(1, 0.83) * mm});
            skLineSegment(sketch, "E30.0.52.3", {"start": v(-1, 0.83) * mm, "end": v(-1, 0.84) * mm});
            skLineSegment(sketch, "E30.0.53.0", {"start": v(-1, 0.85) * mm, "end": v(1, 0.85) * mm});
            skLineSegment(sketch, "E30.0.53.1", {"start": v(1, 0.84) * mm, "end": v(-1, 0.84) * mm});
            skLineSegment(sketch, "E30.0.53.2", {"start": v(1, 0.84) * mm, "end": v(1, 0.84) * mm});
            skLineSegment(sketch, "E30.0.53.3", {"start": v(-1, 0.84) * mm, "end": v(-1, 0.85) * mm});
            skLineSegment(sketch, "E30.0.54.0", {"start": v(-1, 0.86) * mm, "end": v(1, 0.86) * mm});
            skLineSegment(sketch, "E30.0.54.1", {"start": v(1, 0.85) * mm, "end": v(-1, 0.85) * mm});
            skLineSegment(sketch, "E30.0.54.2", {"start": v(1, 0.85) * mm, "end": v(1, 0.85) * mm});
            skLineSegment(sketch, "E30.0.54.3", {"start": v(-1, 0.85) * mm, "end": v(-1, 0.86) * mm});
            skLineSegment(sketch, "E30.0.55.0", {"start": v(-1, 0.87) * mm, "end": v(1, 0.87) * mm});
            skLineSegment(sketch, "E30.0.55.1", {"start": v(1, 0.87) * mm, "end": v(-1, 0.87) * mm});
            skLineSegment(sketch, "E30.0.55.2", {"start": v(1, 0.86) * mm, "end": v(1, 0.87) * mm});
            skLineSegment(sketch, "E30.0.55.3", {"start": v(-1, 0.87) * mm, "end": v(-1, 0.87) * mm});
            skLineSegment(sketch, "E30.0.56.0", {"start": v(-1, 0.88) * mm, "end": v(1, 0.88) * mm});
            skLineSegment(sketch, "E30.0.56.1", {"start": v(1, 0.88) * mm, "end": v(-1, 0.88) * mm});
            skLineSegment(sketch, "E30.0.56.2", {"start": v(1, 0.87) * mm, "end": v(1, 0.88) * mm});
            skLineSegment(sketch, "E30.0.56.3", {"start": v(-1, 0.88) * mm, "end": v(-1, 0.88) * mm});
            skLineSegment(sketch, "E30.0.57.0", {"start": v(-1, 0.9) * mm, "end": v(1, 0.9) * mm});
            skLineSegment(sketch, "E30.0.57.1", {"start": v(1, 0.9) * mm, "end": v(-1, 0.9) * mm});
            skLineSegment(sketch, "E30.0.57.2", {"start": v(1, 0.88) * mm, "end": v(1, 0.9) * mm});
            skLineSegment(sketch, "E30.0.57.3", {"start": v(-1, 0.9) * mm, "end": v(-1, 0.9) * mm});
            skLineSegment(sketch, "E30.0.58.0", {"start": v(-1, 0.9) * mm, "end": v(1, 0.9) * mm});
            skLineSegment(sketch, "E30.0.58.1", {"start": v(1, 0.9) * mm, "end": v(-1, 0.9) * mm});
            skLineSegment(sketch, "E30.0.58.2", {"start": v(1, 0.9) * mm, "end": v(1, 0.9) * mm});
            skLineSegment(sketch, "E30.0.58.3", {"start": v(-1, 0.9) * mm, "end": v(-1, 0.9) * mm});
            skLineSegment(sketch, "E30.0.59.0", {"start": v(-1, 0.92) * mm, "end": v(1, 0.92) * mm});
            skLineSegment(sketch, "E30.0.59.1", {"start": v(1, 0.91) * mm, "end": v(-1, 0.91) * mm});
            skLineSegment(sketch, "E30.0.59.2", {"start": v(1, 0.9) * mm, "end": v(1, 0.91) * mm});
            skLineSegment(sketch, "E30.0.59.3", {"start": v(-1, 0.91) * mm, "end": v(-1, 0.92) * mm});
            skLineSegment(sketch, "E30.0.60.0", {"start": v(-1, 0.93) * mm, "end": v(1, 0.93) * mm});
            skLineSegment(sketch, "E30.0.60.1", {"start": v(1, 0.93) * mm, "end": v(-1, 0.93) * mm});
            skLineSegment(sketch, "E30.0.60.2", {"start": v(1, 0.92) * mm, "end": v(1, 0.93) * mm});
            skLineSegment(sketch, "E30.0.60.3", {"start": v(-1, 0.93) * mm, "end": v(-1, 0.93) * mm});
            skLineSegment(sketch, "E30.0.61.0", {"start": v(-1, 0.94) * mm, "end": v(1, 0.94) * mm});
            skLineSegment(sketch, "E30.0.61.1", {"start": v(1, 0.94) * mm, "end": v(-1, 0.94) * mm});
            skLineSegment(sketch, "E30.0.61.2", {"start": v(1, 0.93) * mm, "end": v(1, 0.94) * mm});
            skLineSegment(sketch, "E30.0.61.3", {"start": v(-1, 0.94) * mm, "end": v(-1, 0.94) * mm});
            skLineSegment(sketch, "E30.0.62.0", {"start": v(-1, 0.96) * mm, "end": v(1, 0.96) * mm});
            skLineSegment(sketch, "E30.0.62.1", {"start": v(1, 0.95) * mm, "end": v(-1, 0.95) * mm});
            skLineSegment(sketch, "E30.0.62.2", {"start": v(1, 0.94) * mm, "end": v(1, 0.95) * mm});
            skLineSegment(sketch, "E30.0.62.3", {"start": v(-1, 0.95) * mm, "end": v(-1, 0.96) * mm});
            skLineSegment(sketch, "E30.0.63.0", {"start": v(-1, 0.97) * mm, "end": v(1, 0.97) * mm});
            skLineSegment(sketch, "E30.0.63.1", {"start": v(1, 0.96) * mm, "end": v(-1, 0.96) * mm});
            skLineSegment(sketch, "E30.0.63.2", {"start": v(1, 0.96) * mm, "end": v(1, 0.96) * mm});
            skLineSegment(sketch, "E30.0.63.3", {"start": v(-1, 0.96) * mm, "end": v(-1, 0.97) * mm});
            skLineSegment(sketch, "E30.0.64.0", {"start": v(-1, 0.98) * mm, "end": v(1, 0.98) * mm});
            skLineSegment(sketch, "E30.0.64.1", {"start": v(1, 0.97) * mm, "end": v(-1, 0.97) * mm});
            skLineSegment(sketch, "E30.0.64.2", {"start": v(1, 0.97) * mm, "end": v(1, 0.97) * mm});
            skLineSegment(sketch, "E30.0.64.3", {"start": v(-1, 0.97) * mm, "end": v(-1, 0.98) * mm});
            skLineSegment(sketch, "E30.0.65.0", {"start": v(-1, 1) * mm, "end": v(1, 1) * mm});
            skLineSegment(sketch, "E30.0.65.1", {"start": v(1, 0.99) * mm, "end": v(-1, 0.99) * mm});
            skLineSegment(sketch, "E30.0.65.2", {"start": v(1, 0.98) * mm, "end": v(1, 0.99) * mm});
            skLineSegment(sketch, "E30.0.65.3", {"start": v(-1, 0.99) * mm, "end": v(-1, 1) * mm});
            skLineSegment(sketch, "E30.direction1", {"start": v(-1, 0.21) * mm, "end": v(24, 0.21) * mm, "construction": true});
            skLineSegment(sketch, "E30.direction2", {"start": v(-1, 0.21) * mm, "end": v(-1, 0.22) * mm, "construction": true});
            skLineSegment(sketch, "E31.0.5.1", {"start": v(1, 0.26) * mm, "end": v(-1, 0.26) * mm});
            skLineSegment(sketch, "E31.0.5.2", {"start": v(1, 0.26) * mm, "end": v(1, 0.26) * mm});
            skLineSegment(sketch, "E31.0.6.3", {"start": v(-1, 0.26) * mm, "end": v(-1, 0.27) * mm});
            skLineSegment(sketch, "E31.0.7.1", {"start": v(1, 0.29) * mm, "end": v(-1, 0.29) * mm});
            skLineSegment(sketch, "E31.0.7.2", {"start": v(1, 0.28) * mm, "end": v(1, 0.29) * mm});
            skLineSegment(sketch, "E31.0.8.3", {"start": v(-1, 0.29) * mm, "end": v(-1, 0.3) * mm});
            skLineSegment(sketch, "E31.0.10.1", {"start": v(1, 0.32) * mm, "end": v(-1, 0.32) * mm});
            skLineSegment(sketch, "E31.0.10.2", {"start": v(1, 0.32) * mm, "end": v(1, 0.32) * mm});
            skLineSegment(sketch, "E31.0.11.3", {"start": v(-1, 0.32) * mm, "end": v(-1, 0.33) * mm});
            skLineSegment(sketch, "E31.0.15.1", {"start": v(1, 0.38) * mm, "end": v(-1, 0.38) * mm});
            skLineSegment(sketch, "E31.0.15.2", {"start": v(1, 0.38) * mm, "end": v(1, 0.38) * mm});
            skLineSegment(sketch, "E31.0.16.3", {"start": v(-1, 0.38) * mm, "end": v(-1, 0.4) * mm});
            skLineSegment(sketch, "E31.0.18.3", {"start": v(-1, 0.4) * mm, "end": v(-1, 0.42) * mm});
            skLineSegment(sketch, "E31.0.20.1", {"start": v(1, 0.44) * mm, "end": v(-1, 0.44) * mm});
            skLineSegment(sketch, "E31.0.20.2", {"start": v(1, 0.44) * mm, "end": v(1, 0.44) * mm});
            skLineSegment(sketch, "E31.0.21.3", {"start": v(-1, 0.44) * mm, "end": v(-1, 0.45) * mm});
            skLineSegment(sketch, "E31.0.30.1", {"start": v(1, 0.56) * mm, "end": v(-1, 0.56) * mm});
            skLineSegment(sketch, "E31.0.30.2", {"start": v(1, 0.56) * mm, "end": v(1, 0.56) * mm});
            skLineSegment(sketch, "E31.0.31.3", {"start": v(-1, 0.56) * mm, "end": v(-1, 0.57) * mm});
            skLineSegment(sketch, "E31.0.32.1", {"start": v(1, 0.59) * mm, "end": v(-1, 0.59) * mm});
            skLineSegment(sketch, "E31.0.32.2", {"start": v(1, 0.58) * mm, "end": v(1, 0.59) * mm});
            skLineSegment(sketch, "E31.0.33.3", {"start": v(-1, 0.59) * mm, "end": v(-1, 0.6) * mm});
            skLineSegment(sketch, "E31.0.35.1", {"start": v(1, 0.62) * mm, "end": v(-1, 0.62) * mm});
            skLineSegment(sketch, "E31.0.35.2", {"start": v(1, 0.62) * mm, "end": v(1, 0.62) * mm});
            skLineSegment(sketch, "E31.0.36.3", {"start": v(-1, 0.62) * mm, "end": v(-1, 0.63) * mm});
            skLineSegment(sketch, "E31.0.40.1", {"start": v(1, 0.68) * mm, "end": v(-1, 0.68) * mm});
            skLineSegment(sketch, "E31.0.40.2", {"start": v(1, 0.68) * mm, "end": v(1, 0.68) * mm});
            skLineSegment(sketch, "E31.0.41.3", {"start": v(-1, 0.68) * mm, "end": v(-1, 0.7) * mm});
            skLineSegment(sketch, "E31.0.43.3", {"start": v(-1, 0.7) * mm, "end": v(-1, 0.72) * mm});
            skLineSegment(sketch, "E31.0.45.1", {"start": v(1, 0.74) * mm, "end": v(-1, 0.74) * mm});
            skLineSegment(sketch, "E31.0.45.2", {"start": v(1, 0.74) * mm, "end": v(1, 0.74) * mm});
            skLineSegment(sketch, "E31.0.46.3", {"start": v(-1, 0.74) * mm, "end": v(-1, 0.75) * mm});
            skLineSegment(sketch, "E31.0.55.1", {"start": v(1, 0.86) * mm, "end": v(-1, 0.86) * mm});
            skLineSegment(sketch, "E31.0.55.2", {"start": v(1, 0.86) * mm, "end": v(1, 0.86) * mm});
            skLineSegment(sketch, "E31.0.56.3", {"start": v(-1, 0.86) * mm, "end": v(-1, 0.87) * mm});
            skLineSegment(sketch, "E31.0.57.1", {"start": v(1, 0.89) * mm, "end": v(-1, 0.89) * mm});
            skLineSegment(sketch, "E31.0.57.2", {"start": v(1, 0.88) * mm, "end": v(1, 0.89) * mm});
            skLineSegment(sketch, "E31.0.58.3", {"start": v(-1, 0.89) * mm, "end": v(-1, 0.9) * mm});
            skLineSegment(sketch, "E31.0.60.1", {"start": v(1, 0.92) * mm, "end": v(-1, 0.92) * mm});
            skLineSegment(sketch, "E31.0.60.2", {"start": v(1, 0.92) * mm, "end": v(1, 0.92) * mm});
            skLineSegment(sketch, "E31.0.61.3", {"start": v(-1, 0.92) * mm, "end": v(-1, 0.93) * mm});
            skLineSegment(sketch, "E31.0.65.1", {"start": v(1, 0.98) * mm, "end": v(-1, 0.98) * mm});
            skLineSegment(sketch, "E31.0.65.2", {"start": v(1, 0.98) * mm, "end": v(1, 0.98) * mm});
            skLineSegment(sketch, "E31.direction1", {"start": v(-1, 0.2) * mm, "end": v(24, 0.2) * mm, "construction": true});
            skLineSegment(sketch, "E31.direction2", {"start": v(-1, 0.2) * mm, "end": v(-1, 0.21) * mm, "construction": true});
            skLineSegment(sketch, "E32.3.0.66", {"start": v(1, 1) * mm, "end": v(-1, 1) * mm});
            skLineSegment(sketch, "E32.6.0.66", {"start": v(1, 1) * mm, "end": v(1, 1) * mm});
            skLineSegment(sketch, "E32.9.0.66", {"start": v(-1, 0.98) * mm, "end": v(-1, 1) * mm});
            skLineSegment(sketch, "E33.9.0.66", {"start": v(-1, 1) * mm, "end": v(-1, 1) * mm});
            skLineSegment(sketch, "E34", {"start": v(-1, 1) * mm, "end": v(-1, 1.25) * mm});
            skLineSegment(sketch, "E35", {"start": v(1, 1) * mm, "end": v(1, 1.26) * mm});
            skSolve(sketch);
        }
        {
            var Q0;
            Q0 = qSketchRegion(id + "F1", true);
            extrude(context, id + "F2", {"entities" : qUnion([Q0]), "depth" : 0 * mm});
        }
        {
            var Q0;
            Q0=qCreatedBy(makeId("Front.planeOp"),FACE);
            var Q1;
            Q1=sQuery(id+"F1.wireOp",EDGE,"E25");
            cPlane(context, id + "F3", {"entities" : qUnion([Q0, Q1]), "cplaneType" : CPlaneType.LINE_ANGLE, "offset" : 25 * mm, "angle" : 0 * degree, "width" : 150 * mm, "height" : 150 * mm});
        }
        {
            var Q0;
            Q0=makeQuery(id+"F2.opExtrude","SWEPT_BODY",BODY,{"disambiguationData":[OSD([sQuery(id+"F1.wireOp",EDGE,"E2"),sQuery(id+"F1.wireOp",EDGE,"E3"),sQuery(id+"F1.wireOp",EDGE,"E4"),sQuery(id+"F1.wireOp",EDGE,"E5"),sQuery(id+"F1.wireOp",EDGE,"E7"),sQuery(id+"F1.wireOp",EDGE,"E8"),sQuery(id+"F1.wireOp",EDGE,"E9"),sQuery(id+"F1.wireOp",EDGE,"E10"),sQuery(id+"F1.wireOp",EDGE,"E11"),sQuery(id+"F1.wireOp",EDGE,"E12"),sQuery(id+"F1.wireOp",EDGE,"E13"),sQuery(id+"F1.wireOp",EDGE,"E14"),sQuery(id+"F1.wireOp",EDGE,"E15"),sQuery(id+"F1.wireOp",EDGE,"E26"),sQuery(id+"F1.wireOp",EDGE,"E27"),sQuery(id+"F1.wireOp",EDGE,"E28.0.1.0"),sQuery(id+"F1.wireOp",EDGE,"E28.0.1.1"),sQuery(id+"F1.wireOp",EDGE,"E28.0.1.2"),sQuery(id+"F1.wireOp",EDGE,"E28.0.1.3"),sQuery(id+"F1.wireOp",EDGE,"E28.0.2.0"),sQuery(id+"F1.wireOp",EDGE,"E28.0.2.1"),sQuery(id+"F1.wireOp",EDGE,"E28.0.2.2"),sQuery(id+"F1.wireOp",EDGE,"E28.0.2.3"),sQuery(id+"F1.wireOp",EDGE,"E28.0.3.0"),sQuery(id+"F1.wireOp",EDGE,"E28.0.3.1"),sQuery(id+"F1.wireOp",EDGE,"E28.0.3.2"),sQuery(id+"F1.wireOp",EDGE,"E28.0.3.3"),sQuery(id+"F1.wireOp",EDGE,"E28.0.4.0"),sQuery(id+"F1.wireOp",EDGE,"E28.0.4.1"),sQuery(id+"F1.wireOp",EDGE,"E28.0.4.2"),sQuery(id+"F1.wireOp",EDGE,"E28.0.4.3"),sQuery(id+"F1.wireOp",EDGE,"E28.0.5.0"),sQuery(id+"F1.wireOp",EDGE,"E28.0.5.1"),sQuery(id+"F1.wireOp",EDGE,"E28.0.5.2"),sQuery(id+"F1.wireOp",EDGE,"E28.0.5.3"),sQuery(id+"F1.wireOp",EDGE,"E28.0.6.0"),sQuery(id+"F1.wireOp",EDGE,"E28.0.6.1"),sQuery(id+"F1.wireOp",EDGE,"E28.0.6.2"),sQuery(id+"F1.wireOp",EDGE,"E28.0.6.3"),sQuery(id+"F1.wireOp",EDGE,"E28.0.7.0"),sQuery(id+"F1.wireOp",EDGE,"E28.0.7.1"),sQuery(id+"F1.wireOp",EDGE,"E28.0.7.2"),sQuery(id+"F1.wireOp",EDGE,"E28.0.7.3"),sQuery(id+"F1.wireOp",EDGE,"E28.0.8.0"),sQuery(id+"F1.wireOp",EDGE,"E28.0.8.1"),sQuery(id+"F1.wireOp",EDGE,"E28.0.8.2"),sQuery(id+"F1.wireOp",EDGE,"E28.0.8.3"),sQuery(id+"F1.wireOp",EDGE,"E28.0.9.0"),sQuery(id+"F1.wireOp",EDGE,"E28.0.9.1"),sQuery(id+"F1.wireOp",EDGE,"E28.0.9.2"),sQuery(id+"F1.wireOp",EDGE,"E28.0.9.3"),sQuery(id+"F1.wireOp",EDGE,"E28.0.10.0"),sQuery(id+"F1.wireOp",EDGE,"E28.0.10.1"),sQuery(id+"F1.wireOp",EDGE,"E28.0.10.2"),sQuery(id+"F1.wireOp",EDGE,"E28.0.10.3"),sQuery(id+"F1.wireOp",EDGE,"E28.0.11.0"),sQuery(id+"F1.wireOp",EDGE,"E28.0.11.1"),sQuery(id+"F1.wireOp",EDGE,"E28.0.11.2"),sQuery(id+"F1.wireOp",EDGE,"E28.0.11.3"),sQuery(id+"F1.wireOp",EDGE,"E28.0.12.0"),sQuery(id+"F1.wireOp",EDGE,"E28.0.12.1"),sQuery(id+"F1.wireOp",EDGE,"E28.0.12.2"),sQuery(id+"F1.wireOp",EDGE,"E28.0.12.3"),sQuery(id+"F1.wireOp",EDGE,"E28.0.13.0"),sQuery(id+"F1.wireOp",EDGE,"E28.0.13.1"),sQuery(id+"F1.wireOp",EDGE,"E28.0.13.2"),sQuery(id+"F1.wireOp",EDGE,"E28.0.13.3"),sQuery(id+"F1.wireOp",EDGE,"E28.0.14.0"),sQuery(id+"F1.wireOp",EDGE,"E28.0.14.1"),sQuery(id+"F1.wireOp",EDGE,"E28.0.14.2"),sQuery(id+"F1.wireOp",EDGE,"E28.0.14.3"),sQuery(id+"F1.wireOp",EDGE,"E28.0.15.0"),sQuery(id+"F1.wireOp",EDGE,"E28.0.15.1"),sQuery(id+"F1.wireOp",EDGE,"E28.0.15.2"),sQuery(id+"F1.wireOp",EDGE,"E28.0.15.3"),sQuery(id+"F1.wireOp",EDGE,"E28.0.16.0"),sQuery(id+"F1.wireOp",EDGE,"E28.0.16.1"),sQuery(id+"F1.wireOp",EDGE,"E28.0.16.2"),sQuery(id+"F1.wireOp",EDGE,"E28.0.16.3"),sQuery(id+"F1.wireOp",EDGE,"E28.0.17.0"),sQuery(id+"F1.wireOp",EDGE,"E28.0.17.1"),sQuery(id+"F1.wireOp",EDGE,"E28.0.17.2"),sQuery(id+"F1.wireOp",EDGE,"E28.0.17.3"),sQuery(id+"F1.wireOp",EDGE,"E28.0.18.0"),sQuery(id+"F1.wireOp",EDGE,"E28.0.18.1"),sQuery(id+"F1.wireOp",EDGE,"E28.0.18.2"),sQuery(id+"F1.wireOp",EDGE,"E28.0.18.3"),sQuery(id+"F1.wireOp",EDGE,"E28.0.19.0"),sQuery(id+"F1.wireOp",EDGE,"E28.0.19.1"),sQuery(id+"F1.wireOp",EDGE,"E28.0.19.2"),sQuery(id+"F1.wireOp",EDGE,"E28.0.19.3"),sQuery(id+"F1.wireOp",EDGE,"E28.0.20.0"),sQuery(id+"F1.wireOp",EDGE,"E28.0.20.1"),sQuery(id+"F1.wireOp",EDGE,"E28.0.20.2"),sQuery(id+"F1.wireOp",EDGE,"E28.0.20.3"),sQuery(id+"F1.wireOp",EDGE,"E28.0.21.0"),sQuery(id+"F1.wireOp",EDGE,"E28.0.21.1"),sQuery(id+"F1.wireOp",EDGE,"E28.0.21.2"),sQuery(id+"F1.wireOp",EDGE,"E28.0.21.3"),sQuery(id+"F1.wireOp",EDGE,"E28.0.22.0"),sQuery(id+"F1.wireOp",EDGE,"E28.0.22.1"),sQuery(id+"F1.wireOp",EDGE,"E28.0.22.2"),sQuery(id+"F1.wireOp",EDGE,"E28.0.22.3"),sQuery(id+"F1.wireOp",EDGE,"E28.0.23.0"),sQuery(id+"F1.wireOp",EDGE,"E28.0.23.1"),sQuery(id+"F1.wireOp",EDGE,"E28.0.23.2"),sQuery(id+"F1.wireOp",EDGE,"E28.0.23.3"),sQuery(id+"F1.wireOp",EDGE,"E28.0.24.0"),sQuery(id+"F1.wireOp",EDGE,"E28.0.24.1"),sQuery(id+"F1.wireOp",EDGE,"E28.0.24.2"),sQuery(id+"F1.wireOp",EDGE,"E28.0.24.3"),sQuery(id+"F1.wireOp",EDGE,"E28.0.25.0"),sQuery(id+"F1.wireOp",EDGE,"E28.0.25.1"),sQuery(id+"F1.wireOp",EDGE,"E28.0.25.2"),sQuery(id+"F1.wireOp",EDGE,"E28.0.25.3"),sQuery(id+"F1.wireOp",EDGE,"E28.0.26.0"),sQuery(id+"F1.wireOp",EDGE,"E28.0.26.1"),sQuery(id+"F1.wireOp",EDGE,"E28.0.26.2"),sQuery(id+"F1.wireOp",EDGE,"E28.0.26.3"),sQuery(id+"F1.wireOp",EDGE,"E28.0.27.0"),sQuery(id+"F1.wireOp",EDGE,"E28.0.27.1"),sQuery(id+"F1.wireOp",EDGE,"E28.0.27.2"),sQuery(id+"F1.wireOp",EDGE,"E28.0.27.3"),sQuery(id+"F1.wireOp",EDGE,"E28.0.28.0"),sQuery(id+"F1.wireOp",EDGE,"E28.0.28.1"),sQuery(id+"F1.wireOp",EDGE,"E28.0.28.2"),sQuery(id+"F1.wireOp",EDGE,"E28.0.28.3"),sQuery(id+"F1.wireOp",EDGE,"E28.0.29.0"),sQuery(id+"F1.wireOp",EDGE,"E28.0.29.1"),sQuery(id+"F1.wireOp",EDGE,"E28.0.29.2"),sQuery(id+"F1.wireOp",EDGE,"E28.0.29.3"),sQuery(id+"F1.wireOp",EDGE,"E28.0.30.0"),sQuery(id+"F1.wireOp",EDGE,"E28.0.30.1"),sQuery(id+"F1.wireOp",EDGE,"E28.0.30.2"),sQuery(id+"F1.wireOp",EDGE,"E28.0.30.3"),sQuery(id+"F1.wireOp",EDGE,"E28.0.31.0"),sQuery(id+"F1.wireOp",EDGE,"E28.0.31.1"),sQuery(id+"F1.wireOp",EDGE,"E28.0.31.2"),sQuery(id+"F1.wireOp",EDGE,"E28.0.31.3"),sQuery(id+"F1.wireOp",EDGE,"E28.0.32.0"),sQuery(id+"F1.wireOp",EDGE,"E28.0.32.1"),sQuery(id+"F1.wireOp",EDGE,"E28.0.32.2"),sQuery(id+"F1.wireOp",EDGE,"E28.0.32.3"),sQuery(id+"F1.wireOp",EDGE,"E28.0.33.0"),sQuery(id+"F1.wireOp",EDGE,"E28.0.33.1"),sQuery(id+"F1.wireOp",EDGE,"E28.0.33.2"),sQuery(id+"F1.wireOp",EDGE,"E28.0.33.3"),sQuery(id+"F1.wireOp",EDGE,"E28.0.34.0"),sQuery(id+"F1.wireOp",EDGE,"E28.0.34.1"),sQuery(id+"F1.wireOp",EDGE,"E28.0.34.2"),sQuery(id+"F1.wireOp",EDGE,"E28.0.34.3"),sQuery(id+"F1.wireOp",EDGE,"E28.0.35.0"),sQuery(id+"F1.wireOp",EDGE,"E28.0.35.1"),sQuery(id+"F1.wireOp",EDGE,"E28.0.35.2"),sQuery(id+"F1.wireOp",EDGE,"E28.0.35.3"),sQuery(id+"F1.wireOp",EDGE,"E28.0.36.0"),sQuery(id+"F1.wireOp",EDGE,"E28.0.36.1"),sQuery(id+"F1.wireOp",EDGE,"E28.0.36.2"),sQuery(id+"F1.wireOp",EDGE,"E28.0.36.3"),sQuery(id+"F1.wireOp",EDGE,"E28.0.37.0"),sQuery(id+"F1.wireOp",EDGE,"E28.0.37.1"),sQuery(id+"F1.wireOp",EDGE,"E28.0.37.2"),sQuery(id+"F1.wireOp",EDGE,"E28.0.37.3"),sQuery(id+"F1.wireOp",EDGE,"E28.0.38.0"),sQuery(id+"F1.wireOp",EDGE,"E28.0.38.1"),sQuery(id+"F1.wireOp",EDGE,"E28.0.38.2"),sQuery(id+"F1.wireOp",EDGE,"E28.0.38.3"),sQuery(id+"F1.wireOp",EDGE,"E28.0.39.0"),sQuery(id+"F1.wireOp",EDGE,"E28.0.39.1"),sQuery(id+"F1.wireOp",EDGE,"E28.0.39.2"),sQuery(id+"F1.wireOp",EDGE,"E28.0.39.3"),sQuery(id+"F1.wireOp",EDGE,"E28.0.40.0"),sQuery(id+"F1.wireOp",EDGE,"E28.0.40.1"),sQuery(id+"F1.wireOp",EDGE,"E28.0.40.2"),sQuery(id+"F1.wireOp",EDGE,"E28.0.40.3"),sQuery(id+"F1.wireOp",EDGE,"E28.0.41.0"),sQuery(id+"F1.wireOp",EDGE,"E28.0.41.1"),sQuery(id+"F1.wireOp",EDGE,"E28.0.41.2"),sQuery(id+"F1.wireOp",EDGE,"E28.0.41.3"),sQuery(id+"F1.wireOp",EDGE,"E28.0.42.0"),sQuery(id+"F1.wireOp",EDGE,"E28.0.42.1"),sQuery(id+"F1.wireOp",EDGE,"E28.0.42.2"),sQuery(id+"F1.wireOp",EDGE,"E28.0.42.3"),sQuery(id+"F1.wireOp",EDGE,"E28.0.43.0"),sQuery(id+"F1.wireOp",EDGE,"E28.0.43.1"),sQuery(id+"F1.wireOp",EDGE,"E28.0.43.2"),sQuery(id+"F1.wireOp",EDGE,"E28.0.43.3"),sQuery(id+"F1.wireOp",EDGE,"E28.0.44.0"),sQuery(id+"F1.wireOp",EDGE,"E28.0.44.1"),sQuery(id+"F1.wireOp",EDGE,"E28.0.44.2"),sQuery(id+"F1.wireOp",EDGE,"E28.0.44.3"),sQuery(id+"F1.wireOp",EDGE,"E28.0.45.0"),sQuery(id+"F1.wireOp",EDGE,"E28.0.45.1"),sQuery(id+"F1.wireOp",EDGE,"E28.0.45.2"),sQuery(id+"F1.wireOp",EDGE,"E28.0.45.3"),sQuery(id+"F1.wireOp",EDGE,"E28.0.46.0"),sQuery(id+"F1.wireOp",EDGE,"E28.0.46.1"),sQuery(id+"F1.wireOp",EDGE,"E28.0.46.2"),sQuery(id+"F1.wireOp",EDGE,"E28.0.46.3"),sQuery(id+"F1.wireOp",EDGE,"E28.0.47.0"),sQuery(id+"F1.wireOp",EDGE,"E28.0.47.1"),sQuery(id+"F1.wireOp",EDGE,"E28.0.47.2"),sQuery(id+"F1.wireOp",EDGE,"E28.0.47.3"),sQuery(id+"F1.wireOp",EDGE,"E28.0.48.0"),sQuery(id+"F1.wireOp",EDGE,"E28.0.48.1"),sQuery(id+"F1.wireOp",EDGE,"E28.0.48.2"),sQuery(id+"F1.wireOp",EDGE,"E28.0.48.3"),sQuery(id+"F1.wireOp",EDGE,"E28.0.49.0"),sQuery(id+"F1.wireOp",EDGE,"E28.0.49.1"),sQuery(id+"F1.wireOp",EDGE,"E28.0.49.2"),sQuery(id+"F1.wireOp",EDGE,"E28.0.49.3"),sQuery(id+"F1.wireOp",EDGE,"E28.0.50.0"),sQuery(id+"F1.wireOp",EDGE,"E28.0.50.1"),sQuery(id+"F1.wireOp",EDGE,"E28.0.50.2"),sQuery(id+"F1.wireOp",EDGE,"E28.0.50.3"),sQuery(id+"F1.wireOp",EDGE,"E28.0.51.0"),sQuery(id+"F1.wireOp",EDGE,"E28.0.51.1"),sQuery(id+"F1.wireOp",EDGE,"E28.0.51.2"),sQuery(id+"F1.wireOp",EDGE,"E28.0.51.3"),sQuery(id+"F1.wireOp",EDGE,"E28.0.52.0"),sQuery(id+"F1.wireOp",EDGE,"E28.0.52.1"),sQuery(id+"F1.wireOp",EDGE,"E28.0.52.2"),sQuery(id+"F1.wireOp",EDGE,"E28.0.52.3"),sQuery(id+"F1.wireOp",EDGE,"E28.0.53.0"),sQuery(id+"F1.wireOp",EDGE,"E28.0.53.1"),sQuery(id+"F1.wireOp",EDGE,"E28.0.53.2"),sQuery(id+"F1.wireOp",EDGE,"E28.0.53.3"),sQuery(id+"F1.wireOp",EDGE,"E28.0.54.0"),sQuery(id+"F1.wireOp",EDGE,"E28.0.54.1"),sQuery(id+"F1.wireOp",EDGE,"E28.0.54.2"),sQuery(id+"F1.wireOp",EDGE,"E28.0.54.3"),sQuery(id+"F1.wireOp",EDGE,"E28.0.55.0"),sQuery(id+"F1.wireOp",EDGE,"E28.0.55.1"),sQuery(id+"F1.wireOp",EDGE,"E28.0.55.2"),sQuery(id+"F1.wireOp",EDGE,"E28.0.55.3"),sQuery(id+"F1.wireOp",EDGE,"E28.0.56.0"),sQuery(id+"F1.wireOp",EDGE,"E28.0.56.1"),sQuery(id+"F1.wireOp",EDGE,"E28.0.56.2"),sQuery(id+"F1.wireOp",EDGE,"E28.0.56.3"),sQuery(id+"F1.wireOp",EDGE,"E28.0.57.0"),sQuery(id+"F1.wireOp",EDGE,"E28.0.57.1"),sQuery(id+"F1.wireOp",EDGE,"E28.0.57.2"),sQuery(id+"F1.wireOp",EDGE,"E28.0.57.3"),sQuery(id+"F1.wireOp",EDGE,"E28.0.58.0"),sQuery(id+"F1.wireOp",EDGE,"E28.0.58.1"),sQuery(id+"F1.wireOp",EDGE,"E28.0.58.2"),sQuery(id+"F1.wireOp",EDGE,"E28.0.58.3"),sQuery(id+"F1.wireOp",EDGE,"E28.0.59.0"),sQuery(id+"F1.wireOp",EDGE,"E28.0.59.1"),sQuery(id+"F1.wireOp",EDGE,"E28.0.59.2"),sQuery(id+"F1.wireOp",EDGE,"E28.0.59.3"),sQuery(id+"F1.wireOp",EDGE,"E28.0.60.0"),sQuery(id+"F1.wireOp",EDGE,"E28.0.60.1"),sQuery(id+"F1.wireOp",EDGE,"E28.0.60.2"),sQuery(id+"F1.wireOp",EDGE,"E28.0.60.3"),sQuery(id+"F1.wireOp",EDGE,"E28.0.61.0"),sQuery(id+"F1.wireOp",EDGE,"E28.0.61.1"),sQuery(id+"F1.wireOp",EDGE,"E28.0.61.2"),sQuery(id+"F1.wireOp",EDGE,"E28.0.61.3"),sQuery(id+"F1.wireOp",EDGE,"E28.0.62.0"),sQuery(id+"F1.wireOp",EDGE,"E28.0.62.1"),sQuery(id+"F1.wireOp",EDGE,"E28.0.62.2"),sQuery(id+"F1.wireOp",EDGE,"E28.0.62.3"),sQuery(id+"F1.wireOp",EDGE,"E28.0.63.0"),sQuery(id+"F1.wireOp",EDGE,"E28.0.63.1"),sQuery(id+"F1.wireOp",EDGE,"E28.0.63.2"),sQuery(id+"F1.wireOp",EDGE,"E28.0.63.3"),sQuery(id+"F1.wireOp",EDGE,"E28.0.64.0"),sQuery(id+"F1.wireOp",EDGE,"E28.0.64.1"),sQuery(id+"F1.wireOp",EDGE,"E28.0.64.2"),sQuery(id+"F1.wireOp",EDGE,"E28.0.64.3"),sQuery(id+"F1.wireOp",EDGE,"E28.0.65.0"),sQuery(id+"F1.wireOp",EDGE,"E28.0.65.1"),sQuery(id+"F1.wireOp",EDGE,"E28.0.65.2"),sQuery(id+"F1.wireOp",EDGE,"E28.0.65.3"),sQuery(id+"F1.wireOp",EDGE,"E28.0.66.0"),sQuery(id+"F1.wireOp",EDGE,"E28.0.66.1"),sQuery(id+"F1.wireOp",EDGE,"E28.0.66.2"),sQuery(id+"F1.wireOp",EDGE,"E28.0.66.3"),sQuery(id+"F1.wireOp",EDGE,"E28.0.67.0"),sQuery(id+"F1.wireOp",EDGE,"E28.0.67.1"),sQuery(id+"F1.wireOp",EDGE,"E28.0.67.2"),sQuery(id+"F1.wireOp",EDGE,"E28.0.67.3"),sQuery(id+"F1.wireOp",EDGE,"E28.0.68.0"),sQuery(id+"F1.wireOp",EDGE,"E28.0.68.1"),sQuery(id+"F1.wireOp",EDGE,"E28.0.68.2"),sQuery(id+"F1.wireOp",EDGE,"E28.0.68.3"),sQuery(id+"F1.wireOp",EDGE,"E28.0.69.0"),sQuery(id+"F1.wireOp",EDGE,"E28.0.69.1"),sQuery(id+"F1.wireOp",EDGE,"E28.0.69.2"),sQuery(id+"F1.wireOp",EDGE,"E28.0.69.3"),sQuery(id+"F1.wireOp",EDGE,"E28.0.70.0"),sQuery(id+"F1.wireOp",EDGE,"E28.0.70.1"),sQuery(id+"F1.wireOp",EDGE,"E28.0.70.2"),sQuery(id+"F1.wireOp",EDGE,"E28.0.70.3"),sQuery(id+"F1.wireOp",EDGE,"E28.0.71.0"),sQuery(id+"F1.wireOp",EDGE,"E28.0.71.1"),sQuery(id+"F1.wireOp",EDGE,"E28.0.71.2"),sQuery(id+"F1.wireOp",EDGE,"E28.0.71.3"),sQuery(id+"F1.wireOp",EDGE,"E28.0.72.0"),sQuery(id+"F1.wireOp",EDGE,"E28.0.72.1"),sQuery(id+"F1.wireOp",EDGE,"E28.0.72.2"),sQuery(id+"F1.wireOp",EDGE,"E28.0.72.3"),sQuery(id+"F1.wireOp",EDGE,"E28.0.73.0"),sQuery(id+"F1.wireOp",EDGE,"E28.0.73.1"),sQuery(id+"F1.wireOp",EDGE,"E28.0.73.2"),sQuery(id+"F1.wireOp",EDGE,"E28.0.73.3"),sQuery(id+"F1.wireOp",EDGE,"E28.0.74.0"),sQuery(id+"F1.wireOp",EDGE,"E28.0.74.1"),sQuery(id+"F1.wireOp",EDGE,"E28.0.74.2"),sQuery(id+"F1.wireOp",EDGE,"E28.0.74.3"),sQuery(id+"F1.wireOp",EDGE,"E28.0.75.0"),sQuery(id+"F1.wireOp",EDGE,"E28.0.75.1"),sQuery(id+"F1.wireOp",EDGE,"E28.0.75.2"),sQuery(id+"F1.wireOp",EDGE,"E28.0.75.3"),sQuery(id+"F1.wireOp",EDGE,"E28.0.76.0"),sQuery(id+"F1.wireOp",EDGE,"E28.0.76.1"),sQuery(id+"F1.wireOp",EDGE,"E28.0.76.2"),sQuery(id+"F1.wireOp",EDGE,"E28.0.76.3"),sQuery(id+"F1.wireOp",EDGE,"E28.0.77.0"),sQuery(id+"F1.wireOp",EDGE,"E28.0.77.1"),sQuery(id+"F1.wireOp",EDGE,"E28.0.77.2"),sQuery(id+"F1.wireOp",EDGE,"E28.0.77.3"),sQuery(id+"F1.wireOp",EDGE,"E28.0.78.0"),sQuery(id+"F1.wireOp",EDGE,"E28.0.78.1"),sQuery(id+"F1.wireOp",EDGE,"E28.0.78.2"),sQuery(id+"F1.wireOp",EDGE,"E28.0.78.3"),sQuery(id+"F1.wireOp",EDGE,"E28.0.79.0"),sQuery(id+"F1.wireOp",EDGE,"E28.0.79.1"),sQuery(id+"F1.wireOp",EDGE,"E28.0.79.2"),sQuery(id+"F1.wireOp",EDGE,"E28.0.79.3"),sQuery(id+"F1.wireOp",EDGE,"E28.0.80.0"),sQuery(id+"F1.wireOp",EDGE,"E28.0.80.1"),sQuery(id+"F1.wireOp",EDGE,"E28.0.80.2"),sQuery(id+"F1.wireOp",EDGE,"E28.0.80.3"),sQuery(id+"F1.wireOp",EDGE,"E28.0.81.0"),sQuery(id+"F1.wireOp",EDGE,"E28.0.81.1"),sQuery(id+"F1.wireOp",EDGE,"E28.0.81.2"),sQuery(id+"F1.wireOp",EDGE,"E28.0.81.3"),sQuery(id+"F1.wireOp",EDGE,"E28.0.82.0"),sQuery(id+"F1.wireOp",EDGE,"E28.0.82.1"),sQuery(id+"F1.wireOp",EDGE,"E28.0.82.2"),sQuery(id+"F1.wireOp",EDGE,"E28.0.82.3"),sQuery(id+"F1.wireOp",EDGE,"E28.0.83.0"),sQuery(id+"F1.wireOp",EDGE,"E28.0.83.1"),sQuery(id+"F1.wireOp",EDGE,"E28.0.83.2"),sQuery(id+"F1.wireOp",EDGE,"E28.0.83.3"),sQuery(id+"F1.wireOp",EDGE,"E28.0.84.0"),sQuery(id+"F1.wireOp",EDGE,"E28.0.84.1"),sQuery(id+"F1.wireOp",EDGE,"E28.0.84.2"),sQuery(id+"F1.wireOp",EDGE,"E28.0.84.3"),sQuery(id+"F1.wireOp",EDGE,"E28.0.85.0"),sQuery(id+"F1.wireOp",EDGE,"E28.0.85.1"),sQuery(id+"F1.wireOp",EDGE,"E28.0.85.2"),sQuery(id+"F1.wireOp",EDGE,"E28.0.85.3"),sQuery(id+"F1.wireOp",EDGE,"E28.0.86.0"),sQuery(id+"F1.wireOp",EDGE,"E28.0.86.1"),sQuery(id+"F1.wireOp",EDGE,"E28.0.86.2"),sQuery(id+"F1.wireOp",EDGE,"E28.0.86.3"),sQuery(id+"F1.wireOp",EDGE,"E28.0.87.0"),sQuery(id+"F1.wireOp",EDGE,"E28.0.87.1"),sQuery(id+"F1.wireOp",EDGE,"E28.0.87.2"),sQuery(id+"F1.wireOp",EDGE,"E28.0.87.3"),sQuery(id+"F1.wireOp",EDGE,"E28.0.88.0"),sQuery(id+"F1.wireOp",EDGE,"E28.0.88.1"),sQuery(id+"F1.wireOp",EDGE,"E28.0.88.2"),sQuery(id+"F1.wireOp",EDGE,"E28.0.88.3"),sQuery(id+"F1.wireOp",EDGE,"E28.0.89.0"),sQuery(id+"F1.wireOp",EDGE,"E28.0.89.1"),sQuery(id+"F1.wireOp",EDGE,"E28.0.89.2"),sQuery(id+"F1.wireOp",EDGE,"E28.0.89.3"),sQuery(id+"F1.wireOp",EDGE,"E28.0.90.0"),sQuery(id+"F1.wireOp",EDGE,"E28.0.90.1"),sQuery(id+"F1.wireOp",EDGE,"E28.0.90.2"),sQuery(id+"F1.wireOp",EDGE,"E28.0.90.3"),sQuery(id+"F1.wireOp",EDGE,"E28.0.91.0"),sQuery(id+"F1.wireOp",EDGE,"E28.0.91.1"),sQuery(id+"F1.wireOp",EDGE,"E28.0.91.2"),sQuery(id+"F1.wireOp",EDGE,"E28.0.91.3"),sQuery(id+"F1.wireOp",EDGE,"E28.0.92.0"),sQuery(id+"F1.wireOp",EDGE,"E28.0.92.1"),sQuery(id+"F1.wireOp",EDGE,"E28.0.92.2"),sQuery(id+"F1.wireOp",EDGE,"E28.0.92.3"),sQuery(id+"F1.wireOp",EDGE,"E28.0.93.0"),sQuery(id+"F1.wireOp",EDGE,"E28.0.93.1"),sQuery(id+"F1.wireOp",EDGE,"E28.0.93.2"),sQuery(id+"F1.wireOp",EDGE,"E28.0.93.3"),sQuery(id+"F1.wireOp",EDGE,"E28.0.94.0"),sQuery(id+"F1.wireOp",EDGE,"E28.0.94.1"),sQuery(id+"F1.wireOp",EDGE,"E28.0.94.2"),sQuery(id+"F1.wireOp",EDGE,"E28.0.94.3"),sQuery(id+"F1.wireOp",EDGE,"E28.0.95.0"),sQuery(id+"F1.wireOp",EDGE,"E28.0.95.1"),sQuery(id+"F1.wireOp",EDGE,"E28.0.95.2"),sQuery(id+"F1.wireOp",EDGE,"E28.0.95.3"),sQuery(id+"F1.wireOp",EDGE,"E28.0.96.0"),sQuery(id+"F1.wireOp",EDGE,"E28.0.96.1"),sQuery(id+"F1.wireOp",EDGE,"E28.0.96.2"),sQuery(id+"F1.wireOp",EDGE,"E28.0.96.3"),sQuery(id+"F1.wireOp",EDGE,"E28.0.97.0"),sQuery(id+"F1.wireOp",EDGE,"E28.0.97.1"),sQuery(id+"F1.wireOp",EDGE,"E28.0.97.2"),sQuery(id+"F1.wireOp",EDGE,"E28.0.97.3"),sQuery(id+"F1.wireOp",EDGE,"E28.0.98.0"),sQuery(id+"F1.wireOp",EDGE,"E28.0.98.1"),sQuery(id+"F1.wireOp",EDGE,"E28.0.98.2"),sQuery(id+"F1.wireOp",EDGE,"E28.0.98.3"),sQuery(id+"F1.wireOp",EDGE,"E28.0.99.0"),sQuery(id+"F1.wireOp",EDGE,"E28.0.99.1"),sQuery(id+"F1.wireOp",EDGE,"E28.0.99.2"),sQuery(id+"F1.wireOp",EDGE,"E28.0.99.3"),sQuery(id+"F1.wireOp",EDGE,"E29.0.99.2"),sQuery(id+"F1.wireOp",EDGE,"E30.0.1.1"),sQuery(id+"F1.wireOp",EDGE,"E30.0.1.2"),sQuery(id+"F1.wireOp",EDGE,"E29.0.99.3"),sQuery(id+"F1.wireOp",EDGE,"E30.0.1.0"),sQuery(id+"F1.wireOp",EDGE,"E30.0.2.1"),sQuery(id+"F1.wireOp",EDGE,"E30.0.2.2"),sQuery(id+"F1.wireOp",EDGE,"E30.0.1.3"),sQuery(id+"F1.wireOp",EDGE,"E30.0.2.0"),sQuery(id+"F1.wireOp",EDGE,"E30.0.3.1"),sQuery(id+"F1.wireOp",EDGE,"E30.0.3.2"),sQuery(id+"F1.wireOp",EDGE,"E30.0.2.3"),sQuery(id+"F1.wireOp",EDGE,"E30.0.3.0"),sQuery(id+"F1.wireOp",EDGE,"E30.0.4.1"),sQuery(id+"F1.wireOp",EDGE,"E30.0.4.2"),sQuery(id+"F1.wireOp",EDGE,"E30.0.3.3"),sQuery(id+"F1.wireOp",EDGE,"E30.0.4.0"),sQuery(id+"F1.wireOp",EDGE,"E31.0.5.1"),sQuery(id+"F1.wireOp",EDGE,"E31.0.5.2"),sQuery(id+"F1.wireOp",EDGE,"E30.0.4.3"),sQuery(id+"F1.wireOp",EDGE,"E30.0.5.0"),sQuery(id+"F1.wireOp",EDGE,"E30.0.6.1"),sQuery(id+"F1.wireOp",EDGE,"E30.0.6.2"),sQuery(id+"F1.wireOp",EDGE,"E31.0.6.3"),sQuery(id+"F1.wireOp",EDGE,"E30.0.6.0"),sQuery(id+"F1.wireOp",EDGE,"E31.0.7.1"),sQuery(id+"F1.wireOp",EDGE,"E31.0.7.2"),sQuery(id+"F1.wireOp",EDGE,"E30.0.6.3"),sQuery(id+"F1.wireOp",EDGE,"E30.0.7.0"),sQuery(id+"F1.wireOp",EDGE,"E30.0.7.1"),sQuery(id+"F1.wireOp",EDGE,"E30.0.8.2"),sQuery(id+"F1.wireOp",EDGE,"E31.0.8.3"),sQuery(id+"F1.wireOp",EDGE,"E30.0.7.0"),sQuery(id+"F1.wireOp",EDGE,"E30.0.9.1"),sQuery(id+"F1.wireOp",EDGE,"E30.0.9.2"),sQuery(id+"F1.wireOp",EDGE,"E30.0.7.3"),sQuery(id+"F1.wireOp",EDGE,"E30.0.9.0"),sQuery(id+"F1.wireOp",EDGE,"E31.0.10.1"),sQuery(id+"F1.wireOp",EDGE,"E31.0.10.2"),sQuery(id+"F1.wireOp",EDGE,"E30.0.9.3"),sQuery(id+"F1.wireOp",EDGE,"E30.0.10.0"),sQuery(id+"F1.wireOp",EDGE,"E30.0.11.1"),sQuery(id+"F1.wireOp",EDGE,"E30.0.11.2"),sQuery(id+"F1.wireOp",EDGE,"E31.0.11.3"),sQuery(id+"F1.wireOp",EDGE,"E30.0.11.0"),sQuery(id+"F1.wireOp",EDGE,"E30.0.12.1"),sQuery(id+"F1.wireOp",EDGE,"E30.0.12.2"),sQuery(id+"F1.wireOp",EDGE,"E30.0.11.3"),sQuery(id+"F1.wireOp",EDGE,"E30.0.12.0"),sQuery(id+"F1.wireOp",EDGE,"E30.0.13.1"),sQuery(id+"F1.wireOp",EDGE,"E30.0.13.2"),sQuery(id+"F1.wireOp",EDGE,"E30.0.12.3"),sQuery(id+"F1.wireOp",EDGE,"E30.0.13.0"),sQuery(id+"F1.wireOp",EDGE,"E30.0.14.1"),sQuery(id+"F1.wireOp",EDGE,"E30.0.14.2"),sQuery(id+"F1.wireOp",EDGE,"E30.0.13.3"),sQuery(id+"F1.wireOp",EDGE,"E30.0.14.0"),sQuery(id+"F1.wireOp",EDGE,"E31.0.15.1"),sQuery(id+"F1.wireOp",EDGE,"E31.0.15.2"),sQuery(id+"F1.wireOp",EDGE,"E30.0.14.3"),sQuery(id+"F1.wireOp",EDGE,"E30.0.15.0"),sQuery(id+"F1.wireOp",EDGE,"E30.0.16.1"),sQuery(id+"F1.wireOp",EDGE,"E30.0.16.2"),sQuery(id+"F1.wireOp",EDGE,"E31.0.16.3"),sQuery(id+"F1.wireOp",EDGE,"E30.0.15.0"),sQuery(id+"F1.wireOp",EDGE,"E30.0.16.1"),sQuery(id+"F1.wireOp",EDGE,"E30.0.16.2"),sQuery(id+"F1.wireOp",EDGE,"E30.0.16.3"),sQuery(id+"F1.wireOp",EDGE,"E30.0.17.0"),sQuery(id+"F1.wireOp",EDGE,"E30.0.18.1"),sQuery(id+"F1.wireOp",EDGE,"E30.0.18.2"),sQuery(id+"F1.wireOp",EDGE,"E31.0.18.3"),sQuery(id+"F1.wireOp",EDGE,"E30.0.18.0"),sQuery(id+"F1.wireOp",EDGE,"E30.0.19.1"),sQuery(id+"F1.wireOp",EDGE,"E30.0.19.2"),sQuery(id+"F1.wireOp",EDGE,"E30.0.18.3"),sQuery(id+"F1.wireOp",EDGE,"E30.0.19.0"),sQuery(id+"F1.wireOp",EDGE,"E31.0.20.1"),sQuery(id+"F1.wireOp",EDGE,"E31.0.20.2"),sQuery(id+"F1.wireOp",EDGE,"E30.0.19.3"),sQuery(id+"F1.wireOp",EDGE,"E30.0.20.0"),sQuery(id+"F1.wireOp",EDGE,"E30.0.21.1"),sQuery(id+"F1.wireOp",EDGE,"E30.0.21.2"),sQuery(id+"F1.wireOp",EDGE,"E31.0.21.3"),sQuery(id+"F1.wireOp",EDGE,"E30.0.21.0"),sQuery(id+"F1.wireOp",EDGE,"E30.0.22.1"),sQuery(id+"F1.wireOp",EDGE,"E30.0.22.2"),sQuery(id+"F1.wireOp",EDGE,"E30.0.21.3"),sQuery(id+"F1.wireOp",EDGE,"E30.0.22.0"),sQuery(id+"F1.wireOp",EDGE,"E30.0.23.1"),sQuery(id+"F1.wireOp",EDGE,"E30.0.23.2"),sQuery(id+"F1.wireOp",EDGE,"E30.0.22.3"),sQuery(id+"F1.wireOp",EDGE,"E30.0.23.0"),sQuery(id+"F1.wireOp",EDGE,"E30.0.24.1"),sQuery(id+"F1.wireOp",EDGE,"E30.0.24.2"),sQuery(id+"F1.wireOp",EDGE,"E30.0.23.3"),sQuery(id+"F1.wireOp",EDGE,"E30.0.24.0"),sQuery(id+"F1.wireOp",EDGE,"E30.0.24.1"),sQuery(id+"F1.wireOp",EDGE,"E30.0.25.2"),sQuery(id+"F1.wireOp",EDGE,"E30.0.24.3"),sQuery(id+"F1.wireOp",EDGE,"E30.0.25.0"),sQuery(id+"F1.wireOp",EDGE,"E30.0.26.1"),sQuery(id+"F1.wireOp",EDGE,"E30.0.26.2"),sQuery(id+"F1.wireOp",EDGE,"E30.0.25.3"),sQuery(id+"F1.wireOp",EDGE,"E30.0.26.0"),sQuery(id+"F1.wireOp",EDGE,"E30.0.27.1"),sQuery(id+"F1.wireOp",EDGE,"E30.0.27.2"),sQuery(id+"F1.wireOp",EDGE,"E30.0.26.3"),sQuery(id+"F1.wireOp",EDGE,"E30.0.27.0"),sQuery(id+"F1.wireOp",EDGE,"E30.0.28.1"),sQuery(id+"F1.wireOp",EDGE,"E30.0.28.2"),sQuery(id+"F1.wireOp",EDGE,"E30.0.27.3"),sQuery(id+"F1.wireOp",EDGE,"E30.0.28.0"),sQuery(id+"F1.wireOp",EDGE,"E30.0.29.1"),sQuery(id+"F1.wireOp",EDGE,"E30.0.29.2"),sQuery(id+"F1.wireOp",EDGE,"E30.0.28.3"),sQuery(id+"F1.wireOp",EDGE,"E30.0.29.0"),sQuery(id+"F1.wireOp",EDGE,"E31.0.30.1"),sQuery(id+"F1.wireOp",EDGE,"E31.0.30.2"),sQuery(id+"F1.wireOp",EDGE,"E30.0.29.3"),sQuery(id+"F1.wireOp",EDGE,"E30.0.30.0"),sQuery(id+"F1.wireOp",EDGE,"E30.0.31.1"),sQuery(id+"F1.wireOp",EDGE,"E30.0.31.2"),sQuery(id+"F1.wireOp",EDGE,"E31.0.31.3"),sQuery(id+"F1.wireOp",EDGE,"E30.0.31.0"),sQuery(id+"F1.wireOp",EDGE,"E31.0.32.1"),sQuery(id+"F1.wireOp",EDGE,"E31.0.32.2"),sQuery(id+"F1.wireOp",EDGE,"E30.0.31.3"),sQuery(id+"F1.wireOp",EDGE,"E30.0.32.0"),sQuery(id+"F1.wireOp",EDGE,"E30.0.32.1"),sQuery(id+"F1.wireOp",EDGE,"E30.0.33.2"),sQuery(id+"F1.wireOp",EDGE,"E31.0.33.3"),sQuery(id+"F1.wireOp",EDGE,"E30.0.32.0"),sQuery(id+"F1.wireOp",EDGE,"E30.0.34.1"),sQuery(id+"F1.wireOp",EDGE,"E30.0.34.2"),sQuery(id+"F1.wireOp",EDGE,"E30.0.32.3"),sQuery(id+"F1.wireOp",EDGE,"E30.0.34.0"),sQuery(id+"F1.wireOp",EDGE,"E31.0.35.1"),sQuery(id+"F1.wireOp",EDGE,"E31.0.35.2"),sQuery(id+"F1.wireOp",EDGE,"E30.0.34.3"),sQuery(id+"F1.wireOp",EDGE,"E30.0.35.0"),sQuery(id+"F1.wireOp",EDGE,"E30.0.36.1"),sQuery(id+"F1.wireOp",EDGE,"E30.0.36.2"),sQuery(id+"F1.wireOp",EDGE,"E31.0.36.3"),sQuery(id+"F1.wireOp",EDGE,"E30.0.36.0"),sQuery(id+"F1.wireOp",EDGE,"E30.0.37.1"),sQuery(id+"F1.wireOp",EDGE,"E30.0.37.2"),sQuery(id+"F1.wireOp",EDGE,"E30.0.36.3"),sQuery(id+"F1.wireOp",EDGE,"E30.0.37.0"),sQuery(id+"F1.wireOp",EDGE,"E30.0.38.1"),sQuery(id+"F1.wireOp",EDGE,"E30.0.38.2"),sQuery(id+"F1.wireOp",EDGE,"E30.0.37.3"),sQuery(id+"F1.wireOp",EDGE,"E30.0.38.0"),sQuery(id+"F1.wireOp",EDGE,"E30.0.39.1"),sQuery(id+"F1.wireOp",EDGE,"E30.0.39.2"),sQuery(id+"F1.wireOp",EDGE,"E30.0.38.3"),sQuery(id+"F1.wireOp",EDGE,"E30.0.39.0"),sQuery(id+"F1.wireOp",EDGE,"E31.0.40.1"),sQuery(id+"F1.wireOp",EDGE,"E31.0.40.2"),sQuery(id+"F1.wireOp",EDGE,"E30.0.39.3"),sQuery(id+"F1.wireOp",EDGE,"E30.0.40.0"),sQuery(id+"F1.wireOp",EDGE,"E30.0.41.1"),sQuery(id+"F1.wireOp",EDGE,"E30.0.41.2"),sQuery(id+"F1.wireOp",EDGE,"E31.0.41.3"),sQuery(id+"F1.wireOp",EDGE,"E30.0.40.0"),sQuery(id+"F1.wireOp",EDGE,"E30.0.41.1"),sQuery(id+"F1.wireOp",EDGE,"E30.0.41.2"),sQuery(id+"F1.wireOp",EDGE,"E30.0.41.3"),sQuery(id+"F1.wireOp",EDGE,"E30.0.42.0"),sQuery(id+"F1.wireOp",EDGE,"E30.0.43.1"),sQuery(id+"F1.wireOp",EDGE,"E30.0.43.2"),sQuery(id+"F1.wireOp",EDGE,"E31.0.43.3"),sQuery(id+"F1.wireOp",EDGE,"E30.0.43.0"),sQuery(id+"F1.wireOp",EDGE,"E30.0.44.1"),sQuery(id+"F1.wireOp",EDGE,"E30.0.44.2"),sQuery(id+"F1.wireOp",EDGE,"E30.0.43.3"),sQuery(id+"F1.wireOp",EDGE,"E30.0.44.0"),sQuery(id+"F1.wireOp",EDGE,"E31.0.45.1"),sQuery(id+"F1.wireOp",EDGE,"E31.0.45.2"),sQuery(id+"F1.wireOp",EDGE,"E30.0.44.3"),sQuery(id+"F1.wireOp",EDGE,"E30.0.45.0"),sQuery(id+"F1.wireOp",EDGE,"E30.0.46.1"),sQuery(id+"F1.wireOp",EDGE,"E30.0.46.2"),sQuery(id+"F1.wireOp",EDGE,"E31.0.46.3"),sQuery(id+"F1.wireOp",EDGE,"E30.0.46.0"),sQuery(id+"F1.wireOp",EDGE,"E30.0.47.1"),sQuery(id+"F1.wireOp",EDGE,"E30.0.47.2"),sQuery(id+"F1.wireOp",EDGE,"E30.0.46.3"),sQuery(id+"F1.wireOp",EDGE,"E30.0.47.0"),sQuery(id+"F1.wireOp",EDGE,"E30.0.48.1"),sQuery(id+"F1.wireOp",EDGE,"E30.0.48.2"),sQuery(id+"F1.wireOp",EDGE,"E30.0.47.3"),sQuery(id+"F1.wireOp",EDGE,"E30.0.48.0"),sQuery(id+"F1.wireOp",EDGE,"E30.0.49.1"),sQuery(id+"F1.wireOp",EDGE,"E30.0.49.2"),sQuery(id+"F1.wireOp",EDGE,"E30.0.48.3"),sQuery(id+"F1.wireOp",EDGE,"E30.0.49.0"),sQuery(id+"F1.wireOp",EDGE,"E30.0.49.1"),sQuery(id+"F1.wireOp",EDGE,"E30.0.50.2"),sQuery(id+"F1.wireOp",EDGE,"E30.0.49.3"),sQuery(id+"F1.wireOp",EDGE,"E30.0.50.0"),sQuery(id+"F1.wireOp",EDGE,"E30.0.51.1"),sQuery(id+"F1.wireOp",EDGE,"E30.0.51.2"),sQuery(id+"F1.wireOp",EDGE,"E30.0.50.3"),sQuery(id+"F1.wireOp",EDGE,"E30.0.51.0"),sQuery(id+"F1.wireOp",EDGE,"E30.0.52.1"),sQuery(id+"F1.wireOp",EDGE,"E30.0.52.2"),sQuery(id+"F1.wireOp",EDGE,"E30.0.51.3"),sQuery(id+"F1.wireOp",EDGE,"E30.0.52.0"),sQuery(id+"F1.wireOp",EDGE,"E30.0.53.1"),sQuery(id+"F1.wireOp",EDGE,"E30.0.53.2"),sQuery(id+"F1.wireOp",EDGE,"E30.0.52.3"),sQuery(id+"F1.wireOp",EDGE,"E30.0.53.0"),sQuery(id+"F1.wireOp",EDGE,"E30.0.54.1"),sQuery(id+"F1.wireOp",EDGE,"E30.0.54.2"),sQuery(id+"F1.wireOp",EDGE,"E30.0.53.3"),sQuery(id+"F1.wireOp",EDGE,"E30.0.54.0"),sQuery(id+"F1.wireOp",EDGE,"E31.0.55.1"),sQuery(id+"F1.wireOp",EDGE,"E31.0.55.2"),sQuery(id+"F1.wireOp",EDGE,"E30.0.54.3"),sQuery(id+"F1.wireOp",EDGE,"E30.0.55.0"),sQuery(id+"F1.wireOp",EDGE,"E30.0.56.1"),sQuery(id+"F1.wireOp",EDGE,"E30.0.56.2"),sQuery(id+"F1.wireOp",EDGE,"E31.0.56.3"),sQuery(id+"F1.wireOp",EDGE,"E30.0.56.0"),sQuery(id+"F1.wireOp",EDGE,"E31.0.57.1"),sQuery(id+"F1.wireOp",EDGE,"E31.0.57.2"),sQuery(id+"F1.wireOp",EDGE,"E30.0.56.3"),sQuery(id+"F1.wireOp",EDGE,"E30.0.57.0"),sQuery(id+"F1.wireOp",EDGE,"E30.0.57.1"),sQuery(id+"F1.wireOp",EDGE,"E30.0.58.2"),sQuery(id+"F1.wireOp",EDGE,"E31.0.58.3"),sQuery(id+"F1.wireOp",EDGE,"E30.0.57.0"),sQuery(id+"F1.wireOp",EDGE,"E30.0.59.1"),sQuery(id+"F1.wireOp",EDGE,"E30.0.59.2"),sQuery(id+"F1.wireOp",EDGE,"E30.0.57.3"),sQuery(id+"F1.wireOp",EDGE,"E30.0.59.0"),sQuery(id+"F1.wireOp",EDGE,"E31.0.60.1"),sQuery(id+"F1.wireOp",EDGE,"E31.0.60.2"),sQuery(id+"F1.wireOp",EDGE,"E30.0.59.3"),sQuery(id+"F1.wireOp",EDGE,"E30.0.60.0"),sQuery(id+"F1.wireOp",EDGE,"E30.0.61.1"),sQuery(id+"F1.wireOp",EDGE,"E30.0.61.2"),sQuery(id+"F1.wireOp",EDGE,"E31.0.61.3"),sQuery(id+"F1.wireOp",EDGE,"E30.0.61.0"),sQuery(id+"F1.wireOp",EDGE,"E30.0.62.1"),sQuery(id+"F1.wireOp",EDGE,"E30.0.62.2"),sQuery(id+"F1.wireOp",EDGE,"E30.0.61.3"),sQuery(id+"F1.wireOp",EDGE,"E30.0.62.0"),sQuery(id+"F1.wireOp",EDGE,"E30.0.63.1"),sQuery(id+"F1.wireOp",EDGE,"E30.0.63.2"),sQuery(id+"F1.wireOp",EDGE,"E30.0.62.3"),sQuery(id+"F1.wireOp",EDGE,"E30.0.63.0"),sQuery(id+"F1.wireOp",EDGE,"E30.0.64.1"),sQuery(id+"F1.wireOp",EDGE,"E30.0.64.2"),sQuery(id+"F1.wireOp",EDGE,"E30.0.63.3"),sQuery(id+"F1.wireOp",EDGE,"E30.0.64.0"),sQuery(id+"F1.wireOp",EDGE,"E31.0.65.1"),sQuery(id+"F1.wireOp",EDGE,"E31.0.65.2"),sQuery(id+"F1.wireOp",EDGE,"E30.0.64.3"),sQuery(id+"F1.wireOp",EDGE,"E30.0.65.0"),sQuery(id+"F1.wireOp",EDGE,"E32.3.0.66"),sQuery(id+"F1.wireOp",EDGE,"E32.6.0.66"),sQuery(id+"F1.wireOp",EDGE,"E32.9.0.66"),sQuery(id+"F1.wireOp",EDGE,"E34")])]});
            var Q1;
            Q1=makeQuery(id+"F2.opExtrude","SWEPT_BODY",BODY,{"disambiguationData":[OSD([sQuery(id+"F1.wireOp",EDGE,"E4"),sQuery(id+"F1.wireOp",EDGE,"E14"),sQuery(id+"F1.wireOp",EDGE,"E15"),sQuery(id+"F1.wireOp",EDGE,"E16.0"),sQuery(id+"F1.wireOp",EDGE,"E17"),sQuery(id+"F1.wireOp",EDGE,"E18"),sQuery(id+"F1.wireOp",EDGE,"E19"),sQuery(id+"F1.wireOp",EDGE,"E20"),sQuery(id+"F1.wireOp",EDGE,"E21"),sQuery(id+"F1.wireOp",EDGE,"E22"),sQuery(id+"F1.wireOp",EDGE,"E23"),sQuery(id+"F1.wireOp",EDGE,"E24"),sQuery(id+"F1.wireOp",EDGE,"E26"),sQuery(id+"F1.wireOp",EDGE,"E27"),sQuery(id+"F1.wireOp",EDGE,"E28.0.1.3"),sQuery(id+"F1.wireOp",EDGE,"E28.0.1.2"),sQuery(id+"F1.wireOp",EDGE,"E28.0.1.1"),sQuery(id+"F1.wireOp",EDGE,"E28.0.1.0"),sQuery(id+"F1.wireOp",EDGE,"E29.0.1.2"),sQuery(id+"F1.wireOp",EDGE,"E29.0.1.3"),sQuery(id+"F1.wireOp",EDGE,"E28.0.2.1"),sQuery(id+"F1.wireOp",EDGE,"E28.0.2.0"),sQuery(id+"F1.wireOp",EDGE,"E28.0.3.2"),sQuery(id+"F1.wireOp",EDGE,"E28.0.3.3"),sQuery(id+"F1.wireOp",EDGE,"E28.0.3.1"),sQuery(id+"F1.wireOp",EDGE,"E28.0.3.0"),sQuery(id+"F1.wireOp",EDGE,"E28.0.4.2"),sQuery(id+"F1.wireOp",EDGE,"E28.0.4.3"),sQuery(id+"F1.wireOp",EDGE,"E29.0.4.0"),sQuery(id+"F1.wireOp",EDGE,"E29.0.4.1"),sQuery(id+"F1.wireOp",EDGE,"E28.0.5.2"),sQuery(id+"F1.wireOp",EDGE,"E29.0.4.3"),sQuery(id+"F1.wireOp",EDGE,"E28.0.5.1"),sQuery(id+"F1.wireOp",EDGE,"E28.0.5.0"),sQuery(id+"F1.wireOp",EDGE,"E28.0.6.2"),sQuery(id+"F1.wireOp",EDGE,"E28.0.6.3"),sQuery(id+"F1.wireOp",EDGE,"E29.0.6.0"),sQuery(id+"F1.wireOp",EDGE,"E28.0.7.0"),sQuery(id+"F1.wireOp",EDGE,"E28.0.7.2"),sQuery(id+"F1.wireOp",EDGE,"E28.0.7.3"),sQuery(id+"F1.wireOp",EDGE,"E28.0.7.1"),sQuery(id+"F1.wireOp",EDGE,"E28.0.7.0"),sQuery(id+"F1.wireOp",EDGE,"E28.0.7.2"),sQuery(id+"F1.wireOp",EDGE,"E28.0.8.3"),sQuery(id+"F1.wireOp",EDGE,"E28.0.8.1"),sQuery(id+"F1.wireOp",EDGE,"E28.0.8.0"),sQuery(id+"F1.wireOp",EDGE,"E28.0.9.2"),sQuery(id+"F1.wireOp",EDGE,"E28.0.9.3"),sQuery(id+"F1.wireOp",EDGE,"E29.0.9.0"),sQuery(id+"F1.wireOp",EDGE,"E29.0.9.1"),sQuery(id+"F1.wireOp",EDGE,"E28.0.10.2"),sQuery(id+"F1.wireOp",EDGE,"E29.0.9.3"),sQuery(id+"F1.wireOp",EDGE,"E28.0.10.1"),sQuery(id+"F1.wireOp",EDGE,"E28.0.10.0"),sQuery(id+"F1.wireOp",EDGE,"E28.0.11.2"),sQuery(id+"F1.wireOp",EDGE,"E28.0.11.3"),sQuery(id+"F1.wireOp",EDGE,"E28.0.11.1"),sQuery(id+"F1.wireOp",EDGE,"E28.0.11.0"),sQuery(id+"F1.wireOp",EDGE,"E28.0.12.2"),sQuery(id+"F1.wireOp",EDGE,"E28.0.12.3"),sQuery(id+"F1.wireOp",EDGE,"E28.0.12.1"),sQuery(id+"F1.wireOp",EDGE,"E28.0.12.0"),sQuery(id+"F1.wireOp",EDGE,"E28.0.13.2"),sQuery(id+"F1.wireOp",EDGE,"E28.0.13.3"),sQuery(id+"F1.wireOp",EDGE,"E28.0.13.1"),sQuery(id+"F1.wireOp",EDGE,"E28.0.13.0"),sQuery(id+"F1.wireOp",EDGE,"E28.0.14.2"),sQuery(id+"F1.wireOp",EDGE,"E28.0.14.3"),sQuery(id+"F1.wireOp",EDGE,"E29.0.14.0"),sQuery(id+"F1.wireOp",EDGE,"E29.0.14.1"),sQuery(id+"F1.wireOp",EDGE,"E28.0.15.2"),sQuery(id+"F1.wireOp",EDGE,"E29.0.14.3"),sQuery(id+"F1.wireOp",EDGE,"E28.0.15.1"),sQuery(id+"F1.wireOp",EDGE,"E28.0.15.0"),sQuery(id+"F1.wireOp",EDGE,"E28.0.15.2"),sQuery(id+"F1.wireOp",EDGE,"E28.0.16.3"),sQuery(id+"F1.wireOp",EDGE,"E29.0.16.0"),sQuery(id+"F1.wireOp",EDGE,"E29.0.16.1"),sQuery(id+"F1.wireOp",EDGE,"E28.0.17.2"),sQuery(id+"F1.wireOp",EDGE,"E29.0.16.3"),sQuery(id+"F1.wireOp",EDGE,"E28.0.17.1"),sQuery(id+"F1.wireOp",EDGE,"E28.0.17.0"),sQuery(id+"F1.wireOp",EDGE,"E28.0.18.2"),sQuery(id+"F1.wireOp",EDGE,"E28.0.18.3"),sQuery(id+"F1.wireOp",EDGE,"E28.0.18.1"),sQuery(id+"F1.wireOp",EDGE,"E28.0.18.0"),sQuery(id+"F1.wireOp",EDGE,"E28.0.19.2"),sQuery(id+"F1.wireOp",EDGE,"E28.0.19.3"),sQuery(id+"F1.wireOp",EDGE,"E29.0.19.0"),sQuery(id+"F1.wireOp",EDGE,"E29.0.19.1"),sQuery(id+"F1.wireOp",EDGE,"E28.0.20.2"),sQuery(id+"F1.wireOp",EDGE,"E29.0.19.3"),sQuery(id+"F1.wireOp",EDGE,"E28.0.20.1"),sQuery(id+"F1.wireOp",EDGE,"E28.0.20.0"),sQuery(id+"F1.wireOp",EDGE,"E28.0.21.2"),sQuery(id+"F1.wireOp",EDGE,"E28.0.21.3"),sQuery(id+"F1.wireOp",EDGE,"E28.0.21.1"),sQuery(id+"F1.wireOp",EDGE,"E28.0.21.0"),sQuery(id+"F1.wireOp",EDGE,"E28.0.22.2"),sQuery(id+"F1.wireOp",EDGE,"E28.0.22.3"),sQuery(id+"F1.wireOp",EDGE,"E28.0.22.1"),sQuery(id+"F1.wireOp",EDGE,"E28.0.22.0"),sQuery(id+"F1.wireOp",EDGE,"E28.0.23.2"),sQuery(id+"F1.wireOp",EDGE,"E28.0.23.3"),sQuery(id+"F1.wireOp",EDGE,"E28.0.23.1"),sQuery(id+"F1.wireOp",EDGE,"E28.0.23.0"),sQuery(id+"F1.wireOp",EDGE,"E28.0.24.2"),sQuery(id+"F1.wireOp",EDGE,"E28.0.24.3"),sQuery(id+"F1.wireOp",EDGE,"E28.0.24.1"),sQuery(id+"F1.wireOp",EDGE,"E28.0.23.0"),sQuery(id+"F1.wireOp",EDGE,"E28.0.25.2"),sQuery(id+"F1.wireOp",EDGE,"E28.0.25.3"),sQuery(id+"F1.wireOp",EDGE,"E28.0.25.1"),sQuery(id+"F1.wireOp",EDGE,"E28.0.25.0"),sQuery(id+"F1.wireOp",EDGE,"E28.0.26.2"),sQuery(id+"F1.wireOp",EDGE,"E28.0.26.3"),sQuery(id+"F1.wireOp",EDGE,"E28.0.26.1"),sQuery(id+"F1.wireOp",EDGE,"E28.0.26.0"),sQuery(id+"F1.wireOp",EDGE,"E28.0.27.2"),sQuery(id+"F1.wireOp",EDGE,"E28.0.27.3"),sQuery(id+"F1.wireOp",EDGE,"E28.0.27.1"),sQuery(id+"F1.wireOp",EDGE,"E28.0.27.0"),sQuery(id+"F1.wireOp",EDGE,"E28.0.28.2"),sQuery(id+"F1.wireOp",EDGE,"E28.0.28.3"),sQuery(id+"F1.wireOp",EDGE,"E28.0.28.1"),sQuery(id+"F1.wireOp",EDGE,"E28.0.28.0"),sQuery(id+"F1.wireOp",EDGE,"E28.0.29.2"),sQuery(id+"F1.wireOp",EDGE,"E28.0.29.3"),sQuery(id+"F1.wireOp",EDGE,"E29.0.29.0"),sQuery(id+"F1.wireOp",EDGE,"E29.0.29.1"),sQuery(id+"F1.wireOp",EDGE,"E28.0.30.2"),sQuery(id+"F1.wireOp",EDGE,"E29.0.29.3"),sQuery(id+"F1.wireOp",EDGE,"E28.0.30.1"),sQuery(id+"F1.wireOp",EDGE,"E28.0.30.0"),sQuery(id+"F1.wireOp",EDGE,"E28.0.31.2"),sQuery(id+"F1.wireOp",EDGE,"E28.0.31.3"),sQuery(id+"F1.wireOp",EDGE,"E29.0.31.0"),sQuery(id+"F1.wireOp",EDGE,"E28.0.32.0"),sQuery(id+"F1.wireOp",EDGE,"E28.0.32.2"),sQuery(id+"F1.wireOp",EDGE,"E28.0.33.3"),sQuery(id+"F1.wireOp",EDGE,"E28.0.32.1"),sQuery(id+"F1.wireOp",EDGE,"E28.0.32.0"),sQuery(id+"F1.wireOp",EDGE,"E28.0.32.2"),sQuery(id+"F1.wireOp",EDGE,"E28.0.33.3"),sQuery(id+"F1.wireOp",EDGE,"E28.0.33.1"),sQuery(id+"F1.wireOp",EDGE,"E28.0.33.0"),sQuery(id+"F1.wireOp",EDGE,"E28.0.34.2"),sQuery(id+"F1.wireOp",EDGE,"E28.0.34.3"),sQuery(id+"F1.wireOp",EDGE,"E29.0.34.0"),sQuery(id+"F1.wireOp",EDGE,"E29.0.34.1"),sQuery(id+"F1.wireOp",EDGE,"E28.0.35.2"),sQuery(id+"F1.wireOp",EDGE,"E29.0.34.3"),sQuery(id+"F1.wireOp",EDGE,"E28.0.35.1"),sQuery(id+"F1.wireOp",EDGE,"E28.0.35.0"),sQuery(id+"F1.wireOp",EDGE,"E28.0.36.2"),sQuery(id+"F1.wireOp",EDGE,"E28.0.36.3"),sQuery(id+"F1.wireOp",EDGE,"E28.0.36.1"),sQuery(id+"F1.wireOp",EDGE,"E28.0.36.0"),sQuery(id+"F1.wireOp",EDGE,"E28.0.37.2"),sQuery(id+"F1.wireOp",EDGE,"E28.0.37.3"),sQuery(id+"F1.wireOp",EDGE,"E28.0.37.1"),sQuery(id+"F1.wireOp",EDGE,"E28.0.37.0"),sQuery(id+"F1.wireOp",EDGE,"E28.0.38.2"),sQuery(id+"F1.wireOp",EDGE,"E28.0.38.3"),sQuery(id+"F1.wireOp",EDGE,"E28.0.38.1"),sQuery(id+"F1.wireOp",EDGE,"E28.0.38.0"),sQuery(id+"F1.wireOp",EDGE,"E28.0.39.2"),sQuery(id+"F1.wireOp",EDGE,"E28.0.39.3"),sQuery(id+"F1.wireOp",EDGE,"E29.0.39.0"),sQuery(id+"F1.wireOp",EDGE,"E29.0.39.1"),sQuery(id+"F1.wireOp",EDGE,"E28.0.40.2"),sQuery(id+"F1.wireOp",EDGE,"E29.0.39.3"),sQuery(id+"F1.wireOp",EDGE,"E28.0.40.1"),sQuery(id+"F1.wireOp",EDGE,"E28.0.40.0"),sQuery(id+"F1.wireOp",EDGE,"E28.0.40.2"),sQuery(id+"F1.wireOp",EDGE,"E28.0.41.3"),sQuery(id+"F1.wireOp",EDGE,"E29.0.41.0"),sQuery(id+"F1.wireOp",EDGE,"E29.0.41.1"),sQuery(id+"F1.wireOp",EDGE,"E28.0.42.2"),sQuery(id+"F1.wireOp",EDGE,"E29.0.41.3"),sQuery(id+"F1.wireOp",EDGE,"E28.0.42.1"),sQuery(id+"F1.wireOp",EDGE,"E28.0.42.0"),sQuery(id+"F1.wireOp",EDGE,"E28.0.43.2"),sQuery(id+"F1.wireOp",EDGE,"E28.0.43.3"),sQuery(id+"F1.wireOp",EDGE,"E28.0.43.1"),sQuery(id+"F1.wireOp",EDGE,"E28.0.43.0"),sQuery(id+"F1.wireOp",EDGE,"E28.0.44.2"),sQuery(id+"F1.wireOp",EDGE,"E28.0.44.3"),sQuery(id+"F1.wireOp",EDGE,"E29.0.44.0"),sQuery(id+"F1.wireOp",EDGE,"E29.0.44.1"),sQuery(id+"F1.wireOp",EDGE,"E28.0.45.2"),sQuery(id+"F1.wireOp",EDGE,"E29.0.44.3"),sQuery(id+"F1.wireOp",EDGE,"E28.0.45.1"),sQuery(id+"F1.wireOp",EDGE,"E28.0.45.0"),sQuery(id+"F1.wireOp",EDGE,"E28.0.46.2"),sQuery(id+"F1.wireOp",EDGE,"E28.0.46.3"),sQuery(id+"F1.wireOp",EDGE,"E28.0.46.1"),sQuery(id+"F1.wireOp",EDGE,"E28.0.46.0"),sQuery(id+"F1.wireOp",EDGE,"E28.0.47.2"),sQuery(id+"F1.wireOp",EDGE,"E28.0.47.3"),sQuery(id+"F1.wireOp",EDGE,"E28.0.47.1"),sQuery(id+"F1.wireOp",EDGE,"E28.0.47.0"),sQuery(id+"F1.wireOp",EDGE,"E28.0.48.2"),sQuery(id+"F1.wireOp",EDGE,"E28.0.48.3"),sQuery(id+"F1.wireOp",EDGE,"E28.0.48.1"),sQuery(id+"F1.wireOp",EDGE,"E28.0.48.0"),sQuery(id+"F1.wireOp",EDGE,"E28.0.49.2"),sQuery(id+"F1.wireOp",EDGE,"E28.0.49.3"),sQuery(id+"F1.wireOp",EDGE,"E28.0.49.1"),sQuery(id+"F1.wireOp",EDGE,"E28.0.48.0"),sQuery(id+"F1.wireOp",EDGE,"E28.0.50.2"),sQuery(id+"F1.wireOp",EDGE,"E28.0.50.3"),sQuery(id+"F1.wireOp",EDGE,"E28.0.50.1"),sQuery(id+"F1.wireOp",EDGE,"E28.0.50.0"),sQuery(id+"F1.wireOp",EDGE,"E28.0.51.2"),sQuery(id+"F1.wireOp",EDGE,"E28.0.51.3"),sQuery(id+"F1.wireOp",EDGE,"E28.0.51.1"),sQuery(id+"F1.wireOp",EDGE,"E28.0.51.0"),sQuery(id+"F1.wireOp",EDGE,"E28.0.52.2"),sQuery(id+"F1.wireOp",EDGE,"E28.0.52.3"),sQuery(id+"F1.wireOp",EDGE,"E28.0.52.1"),sQuery(id+"F1.wireOp",EDGE,"E28.0.52.0"),sQuery(id+"F1.wireOp",EDGE,"E28.0.53.2"),sQuery(id+"F1.wireOp",EDGE,"E28.0.53.3"),sQuery(id+"F1.wireOp",EDGE,"E28.0.53.1"),sQuery(id+"F1.wireOp",EDGE,"E28.0.53.0"),sQuery(id+"F1.wireOp",EDGE,"E28.0.54.2"),sQuery(id+"F1.wireOp",EDGE,"E28.0.54.3"),sQuery(id+"F1.wireOp",EDGE,"E29.0.54.0"),sQuery(id+"F1.wireOp",EDGE,"E29.0.54.1"),sQuery(id+"F1.wireOp",EDGE,"E28.0.55.2"),sQuery(id+"F1.wireOp",EDGE,"E29.0.54.3"),sQuery(id+"F1.wireOp",EDGE,"E28.0.55.1"),sQuery(id+"F1.wireOp",EDGE,"E28.0.55.0"),sQuery(id+"F1.wireOp",EDGE,"E28.0.56.2"),sQuery(id+"F1.wireOp",EDGE,"E28.0.56.3"),sQuery(id+"F1.wireOp",EDGE,"E29.0.56.0"),sQuery(id+"F1.wireOp",EDGE,"E28.0.57.0"),sQuery(id+"F1.wireOp",EDGE,"E28.0.57.2"),sQuery(id+"F1.wireOp",EDGE,"E28.0.58.3"),sQuery(id+"F1.wireOp",EDGE,"E28.0.57.1"),sQuery(id+"F1.wireOp",EDGE,"E28.0.57.0"),sQuery(id+"F1.wireOp",EDGE,"E28.0.57.2"),sQuery(id+"F1.wireOp",EDGE,"E28.0.58.3"),sQuery(id+"F1.wireOp",EDGE,"E28.0.58.1"),sQuery(id+"F1.wireOp",EDGE,"E28.0.58.0"),sQuery(id+"F1.wireOp",EDGE,"E28.0.59.2"),sQuery(id+"F1.wireOp",EDGE,"E28.0.59.3"),sQuery(id+"F1.wireOp",EDGE,"E29.0.59.0"),sQuery(id+"F1.wireOp",EDGE,"E29.0.59.1"),sQuery(id+"F1.wireOp",EDGE,"E28.0.60.2"),sQuery(id+"F1.wireOp",EDGE,"E29.0.59.3"),sQuery(id+"F1.wireOp",EDGE,"E28.0.60.1"),sQuery(id+"F1.wireOp",EDGE,"E28.0.60.0"),sQuery(id+"F1.wireOp",EDGE,"E28.0.61.2"),sQuery(id+"F1.wireOp",EDGE,"E28.0.61.3"),sQuery(id+"F1.wireOp",EDGE,"E28.0.61.1"),sQuery(id+"F1.wireOp",EDGE,"E28.0.61.0"),sQuery(id+"F1.wireOp",EDGE,"E28.0.62.2"),sQuery(id+"F1.wireOp",EDGE,"E28.0.62.3"),sQuery(id+"F1.wireOp",EDGE,"E28.0.62.1"),sQuery(id+"F1.wireOp",EDGE,"E28.0.62.0"),sQuery(id+"F1.wireOp",EDGE,"E28.0.63.2"),sQuery(id+"F1.wireOp",EDGE,"E28.0.63.3"),sQuery(id+"F1.wireOp",EDGE,"E28.0.63.1"),sQuery(id+"F1.wireOp",EDGE,"E28.0.63.0"),sQuery(id+"F1.wireOp",EDGE,"E28.0.64.2"),sQuery(id+"F1.wireOp",EDGE,"E28.0.64.3"),sQuery(id+"F1.wireOp",EDGE,"E29.0.64.0"),sQuery(id+"F1.wireOp",EDGE,"E29.0.64.1"),sQuery(id+"F1.wireOp",EDGE,"E28.0.65.2"),sQuery(id+"F1.wireOp",EDGE,"E29.0.64.3"),sQuery(id+"F1.wireOp",EDGE,"E28.0.65.1"),sQuery(id+"F1.wireOp",EDGE,"E28.0.65.0"),sQuery(id+"F1.wireOp",EDGE,"E28.0.65.2"),sQuery(id+"F1.wireOp",EDGE,"E28.0.66.3"),sQuery(id+"F1.wireOp",EDGE,"E29.0.66.0"),sQuery(id+"F1.wireOp",EDGE,"E29.0.66.1"),sQuery(id+"F1.wireOp",EDGE,"E28.0.67.2"),sQuery(id+"F1.wireOp",EDGE,"E29.0.66.3"),sQuery(id+"F1.wireOp",EDGE,"E28.0.67.1"),sQuery(id+"F1.wireOp",EDGE,"E28.0.67.0"),sQuery(id+"F1.wireOp",EDGE,"E28.0.68.2"),sQuery(id+"F1.wireOp",EDGE,"E28.0.68.3"),sQuery(id+"F1.wireOp",EDGE,"E28.0.68.1"),sQuery(id+"F1.wireOp",EDGE,"E28.0.68.0"),sQuery(id+"F1.wireOp",EDGE,"E28.0.69.2"),sQuery(id+"F1.wireOp",EDGE,"E28.0.69.3"),sQuery(id+"F1.wireOp",EDGE,"E29.0.69.0"),sQuery(id+"F1.wireOp",EDGE,"E29.0.69.1"),sQuery(id+"F1.wireOp",EDGE,"E28.0.70.2"),sQuery(id+"F1.wireOp",EDGE,"E29.0.69.3"),sQuery(id+"F1.wireOp",EDGE,"E28.0.70.1"),sQuery(id+"F1.wireOp",EDGE,"E28.0.70.0"),sQuery(id+"F1.wireOp",EDGE,"E28.0.71.2"),sQuery(id+"F1.wireOp",EDGE,"E28.0.71.3"),sQuery(id+"F1.wireOp",EDGE,"E28.0.71.1"),sQuery(id+"F1.wireOp",EDGE,"E28.0.71.0"),sQuery(id+"F1.wireOp",EDGE,"E28.0.72.2"),sQuery(id+"F1.wireOp",EDGE,"E28.0.72.3"),sQuery(id+"F1.wireOp",EDGE,"E28.0.72.1"),sQuery(id+"F1.wireOp",EDGE,"E28.0.72.0"),sQuery(id+"F1.wireOp",EDGE,"E28.0.73.2"),sQuery(id+"F1.wireOp",EDGE,"E28.0.73.3"),sQuery(id+"F1.wireOp",EDGE,"E28.0.73.1"),sQuery(id+"F1.wireOp",EDGE,"E28.0.73.0"),sQuery(id+"F1.wireOp",EDGE,"E28.0.74.2"),sQuery(id+"F1.wireOp",EDGE,"E28.0.74.3"),sQuery(id+"F1.wireOp",EDGE,"E28.0.74.1"),sQuery(id+"F1.wireOp",EDGE,"E28.0.73.0"),sQuery(id+"F1.wireOp",EDGE,"E28.0.75.2"),sQuery(id+"F1.wireOp",EDGE,"E28.0.75.3"),sQuery(id+"F1.wireOp",EDGE,"E28.0.75.1"),sQuery(id+"F1.wireOp",EDGE,"E28.0.75.0"),sQuery(id+"F1.wireOp",EDGE,"E28.0.76.2"),sQuery(id+"F1.wireOp",EDGE,"E28.0.76.3"),sQuery(id+"F1.wireOp",EDGE,"E28.0.76.1"),sQuery(id+"F1.wireOp",EDGE,"E28.0.76.0"),sQuery(id+"F1.wireOp",EDGE,"E28.0.77.2"),sQuery(id+"F1.wireOp",EDGE,"E28.0.77.3"),sQuery(id+"F1.wireOp",EDGE,"E28.0.77.1"),sQuery(id+"F1.wireOp",EDGE,"E28.0.77.0"),sQuery(id+"F1.wireOp",EDGE,"E28.0.78.2"),sQuery(id+"F1.wireOp",EDGE,"E28.0.78.3"),sQuery(id+"F1.wireOp",EDGE,"E28.0.78.1"),sQuery(id+"F1.wireOp",EDGE,"E28.0.78.0"),sQuery(id+"F1.wireOp",EDGE,"E28.0.79.2"),sQuery(id+"F1.wireOp",EDGE,"E28.0.79.3"),sQuery(id+"F1.wireOp",EDGE,"E29.0.79.0"),sQuery(id+"F1.wireOp",EDGE,"E29.0.79.1"),sQuery(id+"F1.wireOp",EDGE,"E28.0.80.2"),sQuery(id+"F1.wireOp",EDGE,"E29.0.79.3"),sQuery(id+"F1.wireOp",EDGE,"E28.0.80.1"),sQuery(id+"F1.wireOp",EDGE,"E28.0.80.0"),sQuery(id+"F1.wireOp",EDGE,"E28.0.81.2"),sQuery(id+"F1.wireOp",EDGE,"E28.0.81.3"),sQuery(id+"F1.wireOp",EDGE,"E29.0.81.0"),sQuery(id+"F1.wireOp",EDGE,"E28.0.82.0"),sQuery(id+"F1.wireOp",EDGE,"E28.0.82.2"),sQuery(id+"F1.wireOp",EDGE,"E28.0.83.3"),sQuery(id+"F1.wireOp",EDGE,"E28.0.82.1"),sQuery(id+"F1.wireOp",EDGE,"E28.0.82.0"),sQuery(id+"F1.wireOp",EDGE,"E28.0.82.2"),sQuery(id+"F1.wireOp",EDGE,"E28.0.83.3"),sQuery(id+"F1.wireOp",EDGE,"E28.0.83.1"),sQuery(id+"F1.wireOp",EDGE,"E28.0.83.0"),sQuery(id+"F1.wireOp",EDGE,"E28.0.84.2"),sQuery(id+"F1.wireOp",EDGE,"E28.0.84.3"),sQuery(id+"F1.wireOp",EDGE,"E29.0.84.0"),sQuery(id+"F1.wireOp",EDGE,"E29.0.84.1"),sQuery(id+"F1.wireOp",EDGE,"E28.0.85.2"),sQuery(id+"F1.wireOp",EDGE,"E29.0.84.3"),sQuery(id+"F1.wireOp",EDGE,"E28.0.85.1"),sQuery(id+"F1.wireOp",EDGE,"E28.0.85.0"),sQuery(id+"F1.wireOp",EDGE,"E28.0.86.2"),sQuery(id+"F1.wireOp",EDGE,"E28.0.86.3"),sQuery(id+"F1.wireOp",EDGE,"E28.0.86.1"),sQuery(id+"F1.wireOp",EDGE,"E28.0.86.0"),sQuery(id+"F1.wireOp",EDGE,"E28.0.87.2"),sQuery(id+"F1.wireOp",EDGE,"E28.0.87.3"),sQuery(id+"F1.wireOp",EDGE,"E28.0.87.1"),sQuery(id+"F1.wireOp",EDGE,"E28.0.87.0"),sQuery(id+"F1.wireOp",EDGE,"E28.0.88.2"),sQuery(id+"F1.wireOp",EDGE,"E28.0.88.3"),sQuery(id+"F1.wireOp",EDGE,"E28.0.88.1"),sQuery(id+"F1.wireOp",EDGE,"E28.0.88.0"),sQuery(id+"F1.wireOp",EDGE,"E28.0.89.2"),sQuery(id+"F1.wireOp",EDGE,"E28.0.89.3"),sQuery(id+"F1.wireOp",EDGE,"E29.0.89.0"),sQuery(id+"F1.wireOp",EDGE,"E29.0.89.1"),sQuery(id+"F1.wireOp",EDGE,"E28.0.90.2"),sQuery(id+"F1.wireOp",EDGE,"E29.0.89.3"),sQuery(id+"F1.wireOp",EDGE,"E28.0.90.1"),sQuery(id+"F1.wireOp",EDGE,"E28.0.90.0"),sQuery(id+"F1.wireOp",EDGE,"E28.0.90.2"),sQuery(id+"F1.wireOp",EDGE,"E28.0.91.3"),sQuery(id+"F1.wireOp",EDGE,"E29.0.91.0"),sQuery(id+"F1.wireOp",EDGE,"E29.0.91.1"),sQuery(id+"F1.wireOp",EDGE,"E28.0.92.2"),sQuery(id+"F1.wireOp",EDGE,"E29.0.91.3"),sQuery(id+"F1.wireOp",EDGE,"E28.0.92.1"),sQuery(id+"F1.wireOp",EDGE,"E28.0.92.0"),sQuery(id+"F1.wireOp",EDGE,"E28.0.93.2"),sQuery(id+"F1.wireOp",EDGE,"E28.0.93.3"),sQuery(id+"F1.wireOp",EDGE,"E28.0.93.1"),sQuery(id+"F1.wireOp",EDGE,"E28.0.93.0"),sQuery(id+"F1.wireOp",EDGE,"E28.0.94.2"),sQuery(id+"F1.wireOp",EDGE,"E28.0.94.3"),sQuery(id+"F1.wireOp",EDGE,"E29.0.94.0"),sQuery(id+"F1.wireOp",EDGE,"E29.0.94.1"),sQuery(id+"F1.wireOp",EDGE,"E28.0.95.2"),sQuery(id+"F1.wireOp",EDGE,"E29.0.94.3"),sQuery(id+"F1.wireOp",EDGE,"E28.0.95.1"),sQuery(id+"F1.wireOp",EDGE,"E28.0.95.0"),sQuery(id+"F1.wireOp",EDGE,"E28.0.96.2"),sQuery(id+"F1.wireOp",EDGE,"E28.0.96.3"),sQuery(id+"F1.wireOp",EDGE,"E28.0.96.1"),sQuery(id+"F1.wireOp",EDGE,"E28.0.96.0"),sQuery(id+"F1.wireOp",EDGE,"E28.0.97.2"),sQuery(id+"F1.wireOp",EDGE,"E28.0.97.3"),sQuery(id+"F1.wireOp",EDGE,"E28.0.97.1"),sQuery(id+"F1.wireOp",EDGE,"E28.0.97.0"),sQuery(id+"F1.wireOp",EDGE,"E28.0.98.2"),sQuery(id+"F1.wireOp",EDGE,"E28.0.98.3"),sQuery(id+"F1.wireOp",EDGE,"E28.0.98.1"),sQuery(id+"F1.wireOp",EDGE,"E28.0.98.0"),sQuery(id+"F1.wireOp",EDGE,"E28.0.99.2"),sQuery(id+"F1.wireOp",EDGE,"E28.0.99.3"),sQuery(id+"F1.wireOp",EDGE,"E28.0.99.1"),sQuery(id+"F1.wireOp",EDGE,"E28.0.98.0"),sQuery(id+"F1.wireOp",EDGE,"E29.0.99.2"),sQuery(id+"F1.wireOp",EDGE,"E29.0.99.3"),sQuery(id+"F1.wireOp",EDGE,"E30.0.1.0"),sQuery(id+"F1.wireOp",EDGE,"E30.0.1.1"),sQuery(id+"F1.wireOp",EDGE,"E30.0.1.2"),sQuery(id+"F1.wireOp",EDGE,"E30.0.1.3"),sQuery(id+"F1.wireOp",EDGE,"E30.0.2.0"),sQuery(id+"F1.wireOp",EDGE,"E30.0.2.1"),sQuery(id+"F1.wireOp",EDGE,"E30.0.2.2"),sQuery(id+"F1.wireOp",EDGE,"E30.0.2.3"),sQuery(id+"F1.wireOp",EDGE,"E30.0.3.0"),sQuery(id+"F1.wireOp",EDGE,"E30.0.3.1"),sQuery(id+"F1.wireOp",EDGE,"E30.0.3.2"),sQuery(id+"F1.wireOp",EDGE,"E30.0.3.3"),sQuery(id+"F1.wireOp",EDGE,"E30.0.4.0"),sQuery(id+"F1.wireOp",EDGE,"E30.0.4.1"),sQuery(id+"F1.wireOp",EDGE,"E30.0.4.2"),sQuery(id+"F1.wireOp",EDGE,"E30.0.4.3"),sQuery(id+"F1.wireOp",EDGE,"E30.0.5.0"),sQuery(id+"F1.wireOp",EDGE,"E30.0.5.1"),sQuery(id+"F1.wireOp",EDGE,"E30.0.5.2"),sQuery(id+"F1.wireOp",EDGE,"E30.0.5.3"),sQuery(id+"F1.wireOp",EDGE,"E30.0.6.0"),sQuery(id+"F1.wireOp",EDGE,"E30.0.6.1"),sQuery(id+"F1.wireOp",EDGE,"E30.0.6.2"),sQuery(id+"F1.wireOp",EDGE,"E30.0.6.3"),sQuery(id+"F1.wireOp",EDGE,"E30.0.7.0"),sQuery(id+"F1.wireOp",EDGE,"E30.0.7.1"),sQuery(id+"F1.wireOp",EDGE,"E30.0.7.2"),sQuery(id+"F1.wireOp",EDGE,"E30.0.7.3"),sQuery(id+"F1.wireOp",EDGE,"E30.0.8.0"),sQuery(id+"F1.wireOp",EDGE,"E30.0.8.1"),sQuery(id+"F1.wireOp",EDGE,"E30.0.8.2"),sQuery(id+"F1.wireOp",EDGE,"E30.0.8.3"),sQuery(id+"F1.wireOp",EDGE,"E30.0.9.0"),sQuery(id+"F1.wireOp",EDGE,"E30.0.9.1"),sQuery(id+"F1.wireOp",EDGE,"E30.0.9.2"),sQuery(id+"F1.wireOp",EDGE,"E30.0.9.3"),sQuery(id+"F1.wireOp",EDGE,"E30.0.10.0"),sQuery(id+"F1.wireOp",EDGE,"E30.0.10.1"),sQuery(id+"F1.wireOp",EDGE,"E30.0.10.2"),sQuery(id+"F1.wireOp",EDGE,"E30.0.10.3"),sQuery(id+"F1.wireOp",EDGE,"E30.0.11.0"),sQuery(id+"F1.wireOp",EDGE,"E30.0.11.1"),sQuery(id+"F1.wireOp",EDGE,"E30.0.11.2"),sQuery(id+"F1.wireOp",EDGE,"E30.0.11.3"),sQuery(id+"F1.wireOp",EDGE,"E30.0.12.0"),sQuery(id+"F1.wireOp",EDGE,"E30.0.12.1"),sQuery(id+"F1.wireOp",EDGE,"E30.0.12.2"),sQuery(id+"F1.wireOp",EDGE,"E30.0.12.3"),sQuery(id+"F1.wireOp",EDGE,"E30.0.13.0"),sQuery(id+"F1.wireOp",EDGE,"E30.0.13.1"),sQuery(id+"F1.wireOp",EDGE,"E30.0.13.2"),sQuery(id+"F1.wireOp",EDGE,"E30.0.13.3"),sQuery(id+"F1.wireOp",EDGE,"E30.0.14.0"),sQuery(id+"F1.wireOp",EDGE,"E30.0.14.1"),sQuery(id+"F1.wireOp",EDGE,"E30.0.14.2"),sQuery(id+"F1.wireOp",EDGE,"E30.0.14.3"),sQuery(id+"F1.wireOp",EDGE,"E30.0.15.0"),sQuery(id+"F1.wireOp",EDGE,"E30.0.15.1"),sQuery(id+"F1.wireOp",EDGE,"E30.0.15.2"),sQuery(id+"F1.wireOp",EDGE,"E30.0.15.3"),sQuery(id+"F1.wireOp",EDGE,"E30.0.16.0"),sQuery(id+"F1.wireOp",EDGE,"E30.0.16.1"),sQuery(id+"F1.wireOp",EDGE,"E30.0.16.2"),sQuery(id+"F1.wireOp",EDGE,"E30.0.16.3"),sQuery(id+"F1.wireOp",EDGE,"E30.0.17.0"),sQuery(id+"F1.wireOp",EDGE,"E30.0.17.1"),sQuery(id+"F1.wireOp",EDGE,"E30.0.17.2"),sQuery(id+"F1.wireOp",EDGE,"E30.0.17.3"),sQuery(id+"F1.wireOp",EDGE,"E30.0.18.0"),sQuery(id+"F1.wireOp",EDGE,"E30.0.18.1"),sQuery(id+"F1.wireOp",EDGE,"E30.0.18.2"),sQuery(id+"F1.wireOp",EDGE,"E30.0.18.3"),sQuery(id+"F1.wireOp",EDGE,"E30.0.19.0"),sQuery(id+"F1.wireOp",EDGE,"E30.0.19.1"),sQuery(id+"F1.wireOp",EDGE,"E30.0.19.2"),sQuery(id+"F1.wireOp",EDGE,"E30.0.19.3"),sQuery(id+"F1.wireOp",EDGE,"E30.0.20.0"),sQuery(id+"F1.wireOp",EDGE,"E30.0.20.1"),sQuery(id+"F1.wireOp",EDGE,"E30.0.20.2"),sQuery(id+"F1.wireOp",EDGE,"E30.0.20.3"),sQuery(id+"F1.wireOp",EDGE,"E30.0.21.0"),sQuery(id+"F1.wireOp",EDGE,"E30.0.21.1"),sQuery(id+"F1.wireOp",EDGE,"E30.0.21.2"),sQuery(id+"F1.wireOp",EDGE,"E30.0.21.3"),sQuery(id+"F1.wireOp",EDGE,"E30.0.22.0"),sQuery(id+"F1.wireOp",EDGE,"E30.0.22.1"),sQuery(id+"F1.wireOp",EDGE,"E30.0.22.2"),sQuery(id+"F1.wireOp",EDGE,"E30.0.22.3"),sQuery(id+"F1.wireOp",EDGE,"E30.0.23.0"),sQuery(id+"F1.wireOp",EDGE,"E30.0.23.1"),sQuery(id+"F1.wireOp",EDGE,"E30.0.23.2"),sQuery(id+"F1.wireOp",EDGE,"E30.0.23.3"),sQuery(id+"F1.wireOp",EDGE,"E30.0.24.0"),sQuery(id+"F1.wireOp",EDGE,"E30.0.24.1"),sQuery(id+"F1.wireOp",EDGE,"E30.0.24.2"),sQuery(id+"F1.wireOp",EDGE,"E30.0.24.3"),sQuery(id+"F1.wireOp",EDGE,"E30.0.25.0"),sQuery(id+"F1.wireOp",EDGE,"E30.0.25.1"),sQuery(id+"F1.wireOp",EDGE,"E30.0.25.2"),sQuery(id+"F1.wireOp",EDGE,"E30.0.25.3"),sQuery(id+"F1.wireOp",EDGE,"E30.0.26.0"),sQuery(id+"F1.wireOp",EDGE,"E30.0.26.1"),sQuery(id+"F1.wireOp",EDGE,"E30.0.26.2"),sQuery(id+"F1.wireOp",EDGE,"E30.0.26.3"),sQuery(id+"F1.wireOp",EDGE,"E30.0.27.0"),sQuery(id+"F1.wireOp",EDGE,"E30.0.27.1"),sQuery(id+"F1.wireOp",EDGE,"E30.0.27.2"),sQuery(id+"F1.wireOp",EDGE,"E30.0.27.3"),sQuery(id+"F1.wireOp",EDGE,"E30.0.28.0"),sQuery(id+"F1.wireOp",EDGE,"E30.0.28.1"),sQuery(id+"F1.wireOp",EDGE,"E30.0.28.2"),sQuery(id+"F1.wireOp",EDGE,"E30.0.28.3"),sQuery(id+"F1.wireOp",EDGE,"E30.0.29.0"),sQuery(id+"F1.wireOp",EDGE,"E30.0.29.1"),sQuery(id+"F1.wireOp",EDGE,"E30.0.29.2"),sQuery(id+"F1.wireOp",EDGE,"E30.0.29.3"),sQuery(id+"F1.wireOp",EDGE,"E30.0.30.0"),sQuery(id+"F1.wireOp",EDGE,"E30.0.30.1"),sQuery(id+"F1.wireOp",EDGE,"E30.0.30.2"),sQuery(id+"F1.wireOp",EDGE,"E30.0.30.3"),sQuery(id+"F1.wireOp",EDGE,"E30.0.31.0"),sQuery(id+"F1.wireOp",EDGE,"E30.0.31.1"),sQuery(id+"F1.wireOp",EDGE,"E30.0.31.2"),sQuery(id+"F1.wireOp",EDGE,"E30.0.31.3"),sQuery(id+"F1.wireOp",EDGE,"E30.0.32.0"),sQuery(id+"F1.wireOp",EDGE,"E30.0.32.1"),sQuery(id+"F1.wireOp",EDGE,"E30.0.32.2"),sQuery(id+"F1.wireOp",EDGE,"E30.0.32.3"),sQuery(id+"F1.wireOp",EDGE,"E30.0.33.0"),sQuery(id+"F1.wireOp",EDGE,"E30.0.33.1"),sQuery(id+"F1.wireOp",EDGE,"E30.0.33.2"),sQuery(id+"F1.wireOp",EDGE,"E30.0.33.3"),sQuery(id+"F1.wireOp",EDGE,"E30.0.34.0"),sQuery(id+"F1.wireOp",EDGE,"E30.0.34.1"),sQuery(id+"F1.wireOp",EDGE,"E30.0.34.2"),sQuery(id+"F1.wireOp",EDGE,"E30.0.34.3"),sQuery(id+"F1.wireOp",EDGE,"E30.0.35.0"),sQuery(id+"F1.wireOp",EDGE,"E30.0.35.1"),sQuery(id+"F1.wireOp",EDGE,"E30.0.35.2"),sQuery(id+"F1.wireOp",EDGE,"E30.0.35.3"),sQuery(id+"F1.wireOp",EDGE,"E30.0.36.0"),sQuery(id+"F1.wireOp",EDGE,"E30.0.36.1"),sQuery(id+"F1.wireOp",EDGE,"E30.0.36.2"),sQuery(id+"F1.wireOp",EDGE,"E30.0.36.3"),sQuery(id+"F1.wireOp",EDGE,"E30.0.37.0"),sQuery(id+"F1.wireOp",EDGE,"E30.0.37.1"),sQuery(id+"F1.wireOp",EDGE,"E30.0.37.2"),sQuery(id+"F1.wireOp",EDGE,"E30.0.37.3"),sQuery(id+"F1.wireOp",EDGE,"E30.0.38.0"),sQuery(id+"F1.wireOp",EDGE,"E30.0.38.1"),sQuery(id+"F1.wireOp",EDGE,"E30.0.38.2"),sQuery(id+"F1.wireOp",EDGE,"E30.0.38.3"),sQuery(id+"F1.wireOp",EDGE,"E30.0.39.0"),sQuery(id+"F1.wireOp",EDGE,"E30.0.39.1"),sQuery(id+"F1.wireOp",EDGE,"E30.0.39.2"),sQuery(id+"F1.wireOp",EDGE,"E30.0.39.3"),sQuery(id+"F1.wireOp",EDGE,"E30.0.40.0"),sQuery(id+"F1.wireOp",EDGE,"E30.0.40.1"),sQuery(id+"F1.wireOp",EDGE,"E30.0.40.2"),sQuery(id+"F1.wireOp",EDGE,"E30.0.40.3"),sQuery(id+"F1.wireOp",EDGE,"E30.0.41.0"),sQuery(id+"F1.wireOp",EDGE,"E30.0.41.1"),sQuery(id+"F1.wireOp",EDGE,"E30.0.41.2"),sQuery(id+"F1.wireOp",EDGE,"E30.0.41.3"),sQuery(id+"F1.wireOp",EDGE,"E30.0.42.0"),sQuery(id+"F1.wireOp",EDGE,"E30.0.42.1"),sQuery(id+"F1.wireOp",EDGE,"E30.0.42.2"),sQuery(id+"F1.wireOp",EDGE,"E30.0.42.3"),sQuery(id+"F1.wireOp",EDGE,"E30.0.43.0"),sQuery(id+"F1.wireOp",EDGE,"E30.0.43.1"),sQuery(id+"F1.wireOp",EDGE,"E30.0.43.2"),sQuery(id+"F1.wireOp",EDGE,"E30.0.43.3"),sQuery(id+"F1.wireOp",EDGE,"E30.0.44.0"),sQuery(id+"F1.wireOp",EDGE,"E30.0.44.1"),sQuery(id+"F1.wireOp",EDGE,"E30.0.44.2"),sQuery(id+"F1.wireOp",EDGE,"E30.0.44.3"),sQuery(id+"F1.wireOp",EDGE,"E30.0.45.0"),sQuery(id+"F1.wireOp",EDGE,"E30.0.45.1"),sQuery(id+"F1.wireOp",EDGE,"E30.0.45.2"),sQuery(id+"F1.wireOp",EDGE,"E30.0.45.3"),sQuery(id+"F1.wireOp",EDGE,"E30.0.46.0"),sQuery(id+"F1.wireOp",EDGE,"E30.0.46.1"),sQuery(id+"F1.wireOp",EDGE,"E30.0.46.2"),sQuery(id+"F1.wireOp",EDGE,"E30.0.46.3"),sQuery(id+"F1.wireOp",EDGE,"E30.0.47.0"),sQuery(id+"F1.wireOp",EDGE,"E30.0.47.1"),sQuery(id+"F1.wireOp",EDGE,"E30.0.47.2"),sQuery(id+"F1.wireOp",EDGE,"E30.0.47.3"),sQuery(id+"F1.wireOp",EDGE,"E30.0.48.0"),sQuery(id+"F1.wireOp",EDGE,"E30.0.48.1"),sQuery(id+"F1.wireOp",EDGE,"E30.0.48.2"),sQuery(id+"F1.wireOp",EDGE,"E30.0.48.3"),sQuery(id+"F1.wireOp",EDGE,"E30.0.49.0"),sQuery(id+"F1.wireOp",EDGE,"E30.0.49.1"),sQuery(id+"F1.wireOp",EDGE,"E30.0.49.2"),sQuery(id+"F1.wireOp",EDGE,"E30.0.49.3"),sQuery(id+"F1.wireOp",EDGE,"E30.0.50.0"),sQuery(id+"F1.wireOp",EDGE,"E30.0.50.1"),sQuery(id+"F1.wireOp",EDGE,"E30.0.50.2"),sQuery(id+"F1.wireOp",EDGE,"E30.0.50.3"),sQuery(id+"F1.wireOp",EDGE,"E30.0.51.0"),sQuery(id+"F1.wireOp",EDGE,"E30.0.51.1"),sQuery(id+"F1.wireOp",EDGE,"E30.0.51.2"),sQuery(id+"F1.wireOp",EDGE,"E30.0.51.3"),sQuery(id+"F1.wireOp",EDGE,"E30.0.52.0"),sQuery(id+"F1.wireOp",EDGE,"E30.0.52.1"),sQuery(id+"F1.wireOp",EDGE,"E30.0.52.2"),sQuery(id+"F1.wireOp",EDGE,"E30.0.52.3"),sQuery(id+"F1.wireOp",EDGE,"E30.0.53.0"),sQuery(id+"F1.wireOp",EDGE,"E30.0.53.1"),sQuery(id+"F1.wireOp",EDGE,"E30.0.53.2"),sQuery(id+"F1.wireOp",EDGE,"E30.0.53.3"),sQuery(id+"F1.wireOp",EDGE,"E30.0.54.0"),sQuery(id+"F1.wireOp",EDGE,"E30.0.54.1"),sQuery(id+"F1.wireOp",EDGE,"E30.0.54.2"),sQuery(id+"F1.wireOp",EDGE,"E30.0.54.3"),sQuery(id+"F1.wireOp",EDGE,"E30.0.55.0"),sQuery(id+"F1.wireOp",EDGE,"E30.0.55.1"),sQuery(id+"F1.wireOp",EDGE,"E30.0.55.2"),sQuery(id+"F1.wireOp",EDGE,"E30.0.55.3"),sQuery(id+"F1.wireOp",EDGE,"E30.0.56.0"),sQuery(id+"F1.wireOp",EDGE,"E30.0.56.1"),sQuery(id+"F1.wireOp",EDGE,"E30.0.56.2"),sQuery(id+"F1.wireOp",EDGE,"E30.0.56.3"),sQuery(id+"F1.wireOp",EDGE,"E30.0.57.0"),sQuery(id+"F1.wireOp",EDGE,"E30.0.57.1"),sQuery(id+"F1.wireOp",EDGE,"E30.0.57.2"),sQuery(id+"F1.wireOp",EDGE,"E30.0.57.3"),sQuery(id+"F1.wireOp",EDGE,"E30.0.58.0"),sQuery(id+"F1.wireOp",EDGE,"E30.0.58.1"),sQuery(id+"F1.wireOp",EDGE,"E30.0.58.2"),sQuery(id+"F1.wireOp",EDGE,"E30.0.58.3"),sQuery(id+"F1.wireOp",EDGE,"E30.0.59.0"),sQuery(id+"F1.wireOp",EDGE,"E30.0.59.1"),sQuery(id+"F1.wireOp",EDGE,"E30.0.59.2"),sQuery(id+"F1.wireOp",EDGE,"E30.0.59.3"),sQuery(id+"F1.wireOp",EDGE,"E30.0.60.0"),sQuery(id+"F1.wireOp",EDGE,"E30.0.60.1"),sQuery(id+"F1.wireOp",EDGE,"E30.0.60.2"),sQuery(id+"F1.wireOp",EDGE,"E30.0.60.3"),sQuery(id+"F1.wireOp",EDGE,"E30.0.61.0"),sQuery(id+"F1.wireOp",EDGE,"E30.0.61.1"),sQuery(id+"F1.wireOp",EDGE,"E30.0.61.2"),sQuery(id+"F1.wireOp",EDGE,"E30.0.61.3"),sQuery(id+"F1.wireOp",EDGE,"E30.0.62.0"),sQuery(id+"F1.wireOp",EDGE,"E30.0.62.1"),sQuery(id+"F1.wireOp",EDGE,"E30.0.62.2"),sQuery(id+"F1.wireOp",EDGE,"E30.0.62.3"),sQuery(id+"F1.wireOp",EDGE,"E30.0.63.0"),sQuery(id+"F1.wireOp",EDGE,"E30.0.63.1"),sQuery(id+"F1.wireOp",EDGE,"E30.0.63.2"),sQuery(id+"F1.wireOp",EDGE,"E30.0.63.3"),sQuery(id+"F1.wireOp",EDGE,"E30.0.64.0"),sQuery(id+"F1.wireOp",EDGE,"E30.0.64.1"),sQuery(id+"F1.wireOp",EDGE,"E30.0.64.2"),sQuery(id+"F1.wireOp",EDGE,"E30.0.64.3"),sQuery(id+"F1.wireOp",EDGE,"E30.0.65.0"),sQuery(id+"F1.wireOp",EDGE,"E30.0.65.1"),sQuery(id+"F1.wireOp",EDGE,"E30.0.65.2"),sQuery(id+"F1.wireOp",EDGE,"E30.0.65.3"),sQuery(id+"F1.wireOp",EDGE,"E30.0.65.0"),sQuery(id+"F1.wireOp",EDGE,"E32.3.0.66"),sQuery(id+"F1.wireOp",EDGE,"E32.6.0.66"),sQuery(id+"F1.wireOp",EDGE,"E33.9.0.66"),sQuery(id+"F1.wireOp",EDGE,"E35")])]});
            var Q2;
            Q2=qCreatedBy(id+"F3.planeOp",FACE);
            mirror(context, id + "F4", {"entities" : qUnion([Q0, Q1]), "mirrorPlane" : qUnion([Q2])});
        }
    });
